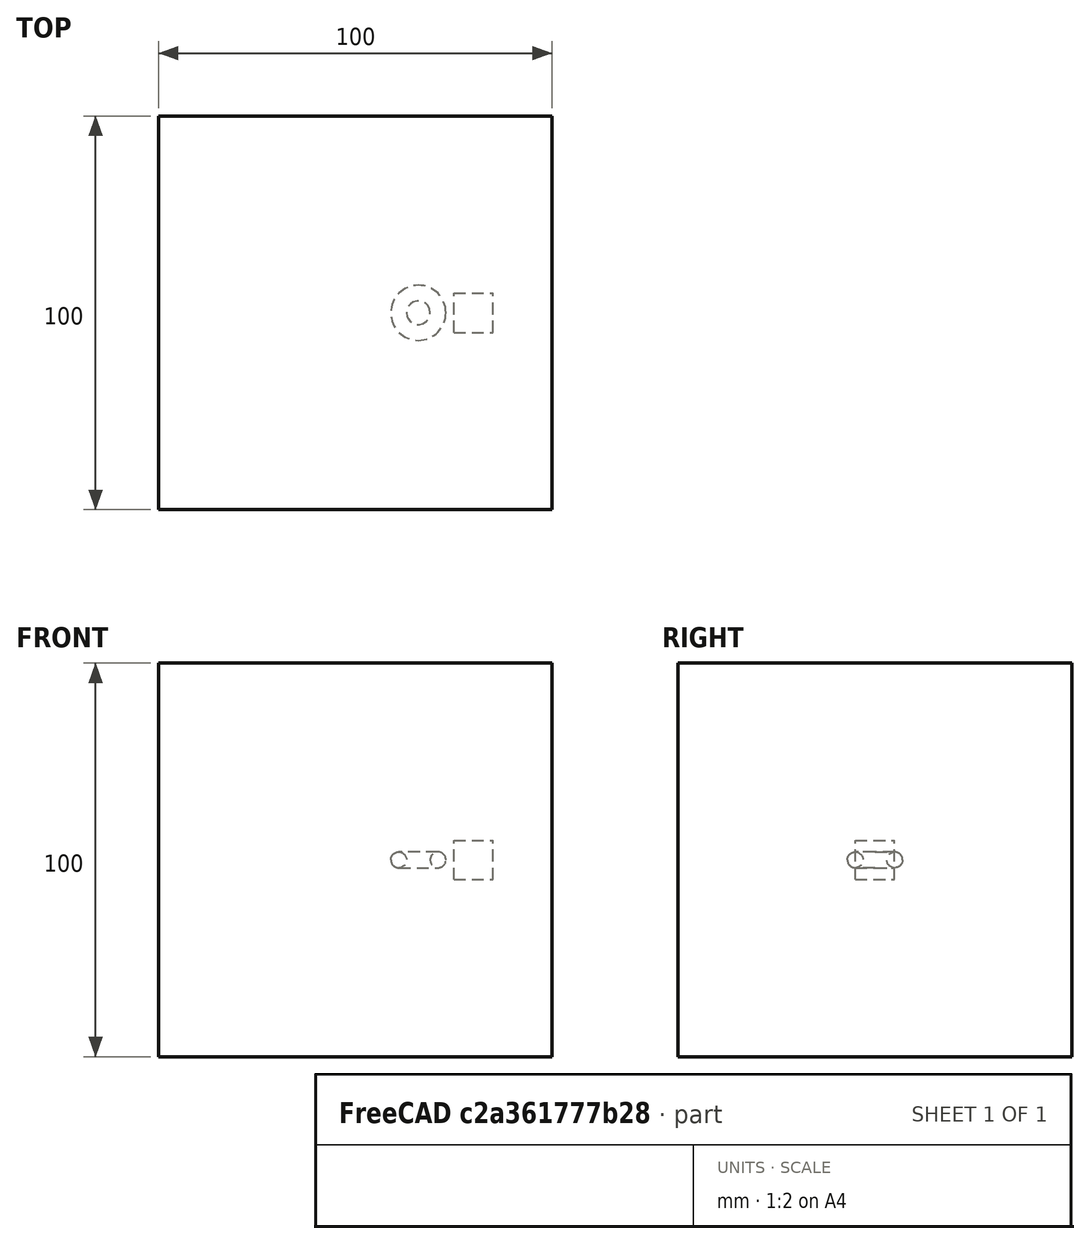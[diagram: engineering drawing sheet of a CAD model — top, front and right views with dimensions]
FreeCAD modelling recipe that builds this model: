
FCSTD DOCUMENT  (FreeCAD 0.20RUnknown)
Label: polarArray-6
License: All rights reserved
objects: App::DocumentObjectGroupPython×1251, App::Part×5, Part::FeaturePython×4
note: 3 computed .brp shape members not serialized (recipe doc carries the construction recipe); baked Part::Feature solids carry a one-line shape summary decoded from their .brp

FEATURE [App::DocumentObjectGroupPython] HALFPI  # scripted group (container) (typed FeaturePython)
  name = HALFPI
  value = pi/2.
FEATURE [App::DocumentObjectGroupPython] PI  # scripted group (container) (typed FeaturePython)
  name = PI
  value = 1.*pi
FEATURE [App::DocumentObjectGroupPython] TWOPI  # scripted group (container) (typed FeaturePython)
  name = TWOPI
  value = 2.*pi
FEATURE [App::DocumentObjectGroupPython] Constants  # scripted group (container) (typed FeaturePython)
  Group = -> [HALFPI,PI,TWOPI]
FEATURE [App::DocumentObjectGroupPython] Variables  # scripted group (container) (typed FeaturePython)
FEATURE [App::DocumentObjectGroupPython] Quantities  # scripted group (container) (typed FeaturePython)
FEATURE [App::DocumentObjectGroupPython] Isotopes  # scripted group (container) (typed FeaturePython)
FEATURE [App::DocumentObjectGroupPython] Elements  # scripted group (container) (typed FeaturePython)
FEATURE [App::DocumentObjectGroupPython] Matrix  # scripted group (container) (typed FeaturePython)
FEATURE [App::DocumentObjectGroupPython] Surfaces  # scripted group (container) (typed FeaturePython)
FEATURE [App::DocumentObjectGroupPython] Opticals  # scripted group (container) (typed FeaturePython)
  Group = -> [Matrix,Surfaces]
FEATURE [App::DocumentObjectGroupPython] G4Isotopes  # scripted group (container) (typed FeaturePython)
FEATURE [App::DocumentObjectGroupPython] H_element  # scripted group (container) (typed FeaturePython)
  Z = 1
  atom_value = 1.008
  formula = H
  name = H_element
FEATURE [App::DocumentObjectGroupPython] He_element  # scripted group (container) (typed FeaturePython)
  Z = 2
  atom_value = 4.0026
  formula = He
  name = He_element
FEATURE [App::DocumentObjectGroupPython] Li_element  # scripted group (container) (typed FeaturePython)
  Z = 3
  atom_value = 6.94
  formula = Li
  name = Li_element
FEATURE [App::DocumentObjectGroupPython] Be_element  # scripted group (container) (typed FeaturePython)
  Z = 4
  atom_value = 9.01218
  formula = Be
  name = Be_element
FEATURE [App::DocumentObjectGroupPython] B_element  # scripted group (container) (typed FeaturePython)
  Z = 5
  atom_value = 10.81
  formula = B
  name = B_element
FEATURE [App::DocumentObjectGroupPython] C_element  # scripted group (container) (typed FeaturePython)
  Z = 6
  atom_value = 12.011
  formula = C
  name = C_element
FEATURE [App::DocumentObjectGroupPython] N_element  # scripted group (container) (typed FeaturePython)
  Z = 7
  atom_value = 14.007
  formula = N
  name = N_element
FEATURE [App::DocumentObjectGroupPython] O_element  # scripted group (container) (typed FeaturePython)
  Z = 8
  atom_value = 15.999
  formula = O
  name = O_element
FEATURE [App::DocumentObjectGroupPython] F_element  # scripted group (container) (typed FeaturePython)
  Z = 9
  atom_value = 18.9984
  formula = F
  name = F_element
FEATURE [App::DocumentObjectGroupPython] Ne_element  # scripted group (container) (typed FeaturePython)
  Z = 10
  atom_value = 20.1797
  formula = Ne
  name = Ne_element
FEATURE [App::DocumentObjectGroupPython] Na_element  # scripted group (container) (typed FeaturePython)
  Z = 11
  atom_value = 22.9898
  formula = Na
  name = Na_element
FEATURE [App::DocumentObjectGroupPython] Mg_element  # scripted group (container) (typed FeaturePython)
  Z = 12
  atom_value = 24.305
  formula = Mg
  name = Mg_element
FEATURE [App::DocumentObjectGroupPython] Al_element  # scripted group (container) (typed FeaturePython)
  Z = 13
  atom_value = 26.9815
  formula = Al
  name = Al_element
FEATURE [App::DocumentObjectGroupPython] Si_element  # scripted group (container) (typed FeaturePython)
  Z = 14
  atom_value = 28.085
  formula = Si
  name = Si_element
FEATURE [App::DocumentObjectGroupPython] P_element  # scripted group (container) (typed FeaturePython)
  Z = 15
  atom_value = 30.9738
  formula = P
  name = P_element
FEATURE [App::DocumentObjectGroupPython] S_element  # scripted group (container) (typed FeaturePython)
  Z = 16
  atom_value = 32.06
  formula = S
  name = S_element
FEATURE [App::DocumentObjectGroupPython] Cl_element  # scripted group (container) (typed FeaturePython)
  Z = 17
  atom_value = 35.45
  formula = Cl
  name = Cl_element
FEATURE [App::DocumentObjectGroupPython] Ar_element  # scripted group (container) (typed FeaturePython)
  Z = 18
  atom_value = 39.95
  formula = Ar
  name = Ar_element
FEATURE [App::DocumentObjectGroupPython] K_element  # scripted group (container) (typed FeaturePython)
  Z = 19
  atom_value = 39.0983
  formula = K
  name = K_element
FEATURE [App::DocumentObjectGroupPython] Ca_element  # scripted group (container) (typed FeaturePython)
  Z = 20
  atom_value = 40.078
  formula = Ca
  name = Ca_element
FEATURE [App::DocumentObjectGroupPython] Sc_element  # scripted group (container) (typed FeaturePython)
  Z = 21
  atom_value = 44.9559
  formula = Sc
  name = Sc_element
FEATURE [App::DocumentObjectGroupPython] Ti_element  # scripted group (container) (typed FeaturePython)
  Z = 22
  atom_value = 47.867
  formula = Ti
  name = Ti_element
FEATURE [App::DocumentObjectGroupPython] V_element  # scripted group (container) (typed FeaturePython)
  Z = 23
  atom_value = 50.9415
  formula = V
  name = V_element
FEATURE [App::DocumentObjectGroupPython] Cr_element  # scripted group (container) (typed FeaturePython)
  Z = 24
  atom_value = 51.9961
  formula = Cr
  name = Cr_element
FEATURE [App::DocumentObjectGroupPython] Mn_element  # scripted group (container) (typed FeaturePython)
  Z = 25
  atom_value = 54.938
  formula = Mn
  name = Mn_element
FEATURE [App::DocumentObjectGroupPython] Fe_element  # scripted group (container) (typed FeaturePython)
  Z = 26
  atom_value = 55.845
  formula = Fe
  name = Fe_element
FEATURE [App::DocumentObjectGroupPython] Co_element  # scripted group (container) (typed FeaturePython)
  Z = 27
  atom_value = 58.9332
  formula = Co
  name = Co_element
FEATURE [App::DocumentObjectGroupPython] Ni_element  # scripted group (container) (typed FeaturePython)
  Z = 28
  atom_value = 58.6934
  formula = Ni
  name = Ni_element
FEATURE [App::DocumentObjectGroupPython] Cu_element  # scripted group (container) (typed FeaturePython)
  Z = 29
  atom_value = 63.546
  formula = Cu
  name = Cu_element
FEATURE [App::DocumentObjectGroupPython] Zn_element  # scripted group (container) (typed FeaturePython)
  Z = 30
  atom_value = 65.38
  formula = Zn
  name = Zn_element
FEATURE [App::DocumentObjectGroupPython] Ga_element  # scripted group (container) (typed FeaturePython)
  Z = 31
  atom_value = 69.723
  formula = Ga
  name = Ga_element
FEATURE [App::DocumentObjectGroupPython] Ge_element  # scripted group (container) (typed FeaturePython)
  Z = 32
  atom_value = 72.63
  formula = Ge
  name = Ge_element
FEATURE [App::DocumentObjectGroupPython] As_element  # scripted group (container) (typed FeaturePython)
  Z = 33
  atom_value = 74.9216
  formula = As
  name = As_element
FEATURE [App::DocumentObjectGroupPython] Se_element  # scripted group (container) (typed FeaturePython)
  Z = 34
  atom_value = 78.971
  formula = Se
  name = Se_element
FEATURE [App::DocumentObjectGroupPython] Br_element  # scripted group (container) (typed FeaturePython)
  Z = 35
  atom_value = 79.904
  formula = Br
  name = Br_element
FEATURE [App::DocumentObjectGroupPython] Kr_element  # scripted group (container) (typed FeaturePython)
  Z = 36
  atom_value = 83.798
  formula = Kr
  name = Kr_element
FEATURE [App::DocumentObjectGroupPython] Rb_element  # scripted group (container) (typed FeaturePython)
  Z = 37
  atom_value = 85.4678
  formula = Rb
  name = Rb_element
FEATURE [App::DocumentObjectGroupPython] Sr_element  # scripted group (container) (typed FeaturePython)
  Z = 38
  atom_value = 87.62
  formula = Sr
  name = Sr_element
FEATURE [App::DocumentObjectGroupPython] Y_element  # scripted group (container) (typed FeaturePython)
  Z = 39
  atom_value = 88.9058
  formula = Y
  name = Y_element
FEATURE [App::DocumentObjectGroupPython] Zr_element  # scripted group (container) (typed FeaturePython)
  Z = 40
  atom_value = 91.224
  formula = Zr
  name = Zr_element
FEATURE [App::DocumentObjectGroupPython] Nb_element  # scripted group (container) (typed FeaturePython)
  Z = 41
  atom_value = 92.9064
  formula = Nb
  name = Nb_element
FEATURE [App::DocumentObjectGroupPython] Mo_element  # scripted group (container) (typed FeaturePython)
  Z = 42
  atom_value = 95.95
  formula = Mo
  name = Mo_element
FEATURE [App::DocumentObjectGroupPython] Tc_element  # scripted group (container) (typed FeaturePython)
  Z = 43
  atom_value = 97
  formula = Tc
  name = Tc_element
FEATURE [App::DocumentObjectGroupPython] Ru_element  # scripted group (container) (typed FeaturePython)
  Z = 44
  atom_value = 101.07
  formula = Ru
  name = Ru_element
FEATURE [App::DocumentObjectGroupPython] Rh_element  # scripted group (container) (typed FeaturePython)
  Z = 45
  atom_value = 102.905
  formula = Rh
  name = Rh_element
FEATURE [App::DocumentObjectGroupPython] Pd_element  # scripted group (container) (typed FeaturePython)
  Z = 46
  atom_value = 106.42
  formula = Pd
  name = Pd_element
FEATURE [App::DocumentObjectGroupPython] Ag_element  # scripted group (container) (typed FeaturePython)
  Z = 47
  atom_value = 107.868
  formula = Ag
  name = Ag_element
FEATURE [App::DocumentObjectGroupPython] Cd_element  # scripted group (container) (typed FeaturePython)
  Z = 48
  atom_value = 112.414
  formula = Cd
  name = Cd_element
FEATURE [App::DocumentObjectGroupPython] In_element  # scripted group (container) (typed FeaturePython)
  Z = 49
  atom_value = 114.818
  formula = In
  name = In_element
FEATURE [App::DocumentObjectGroupPython] Sn_element  # scripted group (container) (typed FeaturePython)
  Z = 50
  atom_value = 118.71
  formula = Sn
  name = Sn_element
FEATURE [App::DocumentObjectGroupPython] Sb_element  # scripted group (container) (typed FeaturePython)
  Z = 51
  atom_value = 121.76
  formula = Sb
  name = Sb_element
FEATURE [App::DocumentObjectGroupPython] Te_element  # scripted group (container) (typed FeaturePython)
  Z = 52
  atom_value = 127.6
  formula = Te
  name = Te_element
FEATURE [App::DocumentObjectGroupPython] I_element  # scripted group (container) (typed FeaturePython)
  Z = 53
  atom_value = 126.904
  formula = I
  name = I_element
FEATURE [App::DocumentObjectGroupPython] Xe_element  # scripted group (container) (typed FeaturePython)
  Z = 54
  atom_value = 131.293
  formula = Xe
  name = Xe_element
FEATURE [App::DocumentObjectGroupPython] Cs_element  # scripted group (container) (typed FeaturePython)
  Z = 55
  atom_value = 132.905
  formula = Cs
  name = Cs_element
FEATURE [App::DocumentObjectGroupPython] Ba_element  # scripted group (container) (typed FeaturePython)
  Z = 56
  atom_value = 137.327
  formula = Ba
  name = Ba_element
FEATURE [App::DocumentObjectGroupPython] La_element  # scripted group (container) (typed FeaturePython)
  Z = 57
  atom_value = 138.905
  formula = La
  name = La_element
FEATURE [App::DocumentObjectGroupPython] Ce_element  # scripted group (container) (typed FeaturePython)
  Z = 58
  atom_value = 140.116
  formula = Ce
  name = Ce_element
FEATURE [App::DocumentObjectGroupPython] Pr_element  # scripted group (container) (typed FeaturePython)
  Z = 59
  atom_value = 140.908
  formula = Pr
  name = Pr_element
FEATURE [App::DocumentObjectGroupPython] Nd_element  # scripted group (container) (typed FeaturePython)
  Z = 60
  atom_value = 144.242
  formula = Nd
  name = Nd_element
FEATURE [App::DocumentObjectGroupPython] Pm_element  # scripted group (container) (typed FeaturePython)
  Z = 61
  atom_value = 145
  formula = Pm
  name = Pm_element
FEATURE [App::DocumentObjectGroupPython] Sm_element  # scripted group (container) (typed FeaturePython)
  Z = 62
  atom_value = 150.36
  formula = Sm
  name = Sm_element
FEATURE [App::DocumentObjectGroupPython] Eu_element  # scripted group (container) (typed FeaturePython)
  Z = 63
  atom_value = 151.964
  formula = Eu
  name = Eu_element
FEATURE [App::DocumentObjectGroupPython] Gd_element  # scripted group (container) (typed FeaturePython)
  Z = 64
  atom_value = 157.25
  formula = Gd
  name = Gd_element
FEATURE [App::DocumentObjectGroupPython] Tb_element  # scripted group (container) (typed FeaturePython)
  Z = 65
  atom_value = 158.925
  formula = Tb
  name = Tb_element
FEATURE [App::DocumentObjectGroupPython] Dy_element  # scripted group (container) (typed FeaturePython)
  Z = 66
  atom_value = 162.5
  formula = Dy
  name = Dy_element
FEATURE [App::DocumentObjectGroupPython] Ho_element  # scripted group (container) (typed FeaturePython)
  Z = 67
  atom_value = 164.93
  formula = Ho
  name = Ho_element
FEATURE [App::DocumentObjectGroupPython] Er_element  # scripted group (container) (typed FeaturePython)
  Z = 68
  atom_value = 167.259
  formula = Er
  name = Er_element
FEATURE [App::DocumentObjectGroupPython] Tm_element  # scripted group (container) (typed FeaturePython)
  Z = 69
  atom_value = 168.934
  formula = Tm
  name = Tm_element
FEATURE [App::DocumentObjectGroupPython] Yb_element  # scripted group (container) (typed FeaturePython)
  Z = 70
  atom_value = 173.045
  formula = Yb
  name = Yb_element
FEATURE [App::DocumentObjectGroupPython] Lu_element  # scripted group (container) (typed FeaturePython)
  Z = 71
  atom_value = 174.967
  formula = Lu
  name = Lu_element
FEATURE [App::DocumentObjectGroupPython] Hf_element  # scripted group (container) (typed FeaturePython)
  Z = 72
  atom_value = 178.49
  formula = Hf
  name = Hf_element
FEATURE [App::DocumentObjectGroupPython] Ta_element  # scripted group (container) (typed FeaturePython)
  Z = 73
  atom_value = 180.948
  formula = Ta
  name = Ta_element
FEATURE [App::DocumentObjectGroupPython] W_element  # scripted group (container) (typed FeaturePython)
  Z = 74
  atom_value = 183.84
  formula = W
  name = W_element
FEATURE [App::DocumentObjectGroupPython] Re_element  # scripted group (container) (typed FeaturePython)
  Z = 75
  atom_value = 186.207
  formula = Re
  name = Re_element
FEATURE [App::DocumentObjectGroupPython] Os_element  # scripted group (container) (typed FeaturePython)
  Z = 76
  atom_value = 190.23
  formula = Os
  name = Os_element
FEATURE [App::DocumentObjectGroupPython] Ir_element  # scripted group (container) (typed FeaturePython)
  Z = 77
  atom_value = 192.217
  formula = Ir
  name = Ir_element
FEATURE [App::DocumentObjectGroupPython] Pt_element  # scripted group (container) (typed FeaturePython)
  Z = 78
  atom_value = 195.084
  formula = Pt
  name = Pt_element
FEATURE [App::DocumentObjectGroupPython] Au_element  # scripted group (container) (typed FeaturePython)
  Z = 79
  atom_value = 196.967
  formula = Au
  name = Au_element
FEATURE [App::DocumentObjectGroupPython] Hg_element  # scripted group (container) (typed FeaturePython)
  Z = 80
  atom_value = 200.592
  formula = Hg
  name = Hg_element
FEATURE [App::DocumentObjectGroupPython] Tl_element  # scripted group (container) (typed FeaturePython)
  Z = 81
  atom_value = 204.38
  formula = Tl
  name = Tl_element
FEATURE [App::DocumentObjectGroupPython] Pb_element  # scripted group (container) (typed FeaturePython)
  Z = 82
  atom_value = 207.2
  formula = Pb
  name = Pb_element
FEATURE [App::DocumentObjectGroupPython] Bi_element  # scripted group (container) (typed FeaturePython)
  Z = 83
  atom_value = 208.98
  formula = Bi
  name = Bi_element
FEATURE [App::DocumentObjectGroupPython] Po_element  # scripted group (container) (typed FeaturePython)
  Z = 84
  atom_value = 209
  formula = Po
  name = Po_element
FEATURE [App::DocumentObjectGroupPython] At_element  # scripted group (container) (typed FeaturePython)
  Z = 85
  atom_value = 210
  formula = At
  name = At_element
FEATURE [App::DocumentObjectGroupPython] Rn_element  # scripted group (container) (typed FeaturePython)
  Z = 86
  atom_value = 222
  formula = Rn
  name = Rn_element
FEATURE [App::DocumentObjectGroupPython] Fr_element  # scripted group (container) (typed FeaturePython)
  Z = 87
  atom_value = 223
  formula = Fr
  name = Fr_element
FEATURE [App::DocumentObjectGroupPython] Ra_element  # scripted group (container) (typed FeaturePython)
  Z = 88
  atom_value = 226
  formula = Ra
  name = Ra_element
FEATURE [App::DocumentObjectGroupPython] Ac_element  # scripted group (container) (typed FeaturePython)
  Z = 89
  atom_value = 227
  formula = Ac
  name = Ac_element
FEATURE [App::DocumentObjectGroupPython] Th_element  # scripted group (container) (typed FeaturePython)
  Z = 90
  atom_value = 232.038
  formula = Th
  name = Th_element
FEATURE [App::DocumentObjectGroupPython] Pa_element  # scripted group (container) (typed FeaturePython)
  Z = 91
  atom_value = 231.036
  formula = Pa
  name = Pa_element
FEATURE [App::DocumentObjectGroupPython] U_element  # scripted group (container) (typed FeaturePython)
  Z = 92
  atom_value = 238.029
  formula = U
  name = U_element
FEATURE [App::DocumentObjectGroupPython] Np_element  # scripted group (container) (typed FeaturePython)
  Z = 93
  atom_value = 237
  formula = Np
  name = Np_element
FEATURE [App::DocumentObjectGroupPython] Pu_element  # scripted group (container) (typed FeaturePython)
  Z = 94
  atom_value = 244
  formula = Pu
  name = Pu_element
FEATURE [App::DocumentObjectGroupPython] Am_element  # scripted group (container) (typed FeaturePython)
  Z = 95
  atom_value = 243
  formula = Am
  name = Am_element
FEATURE [App::DocumentObjectGroupPython] Cm_element  # scripted group (container) (typed FeaturePython)
  Z = 96
  atom_value = 247
  formula = Cm
  name = Cm_element
FEATURE [App::DocumentObjectGroupPython] Bk_element  # scripted group (container) (typed FeaturePython)
  Z = 97
  atom_value = 247
  formula = Bk
  name = Bk_element
FEATURE [App::DocumentObjectGroupPython] Cf_element  # scripted group (container) (typed FeaturePython)
  Z = 98
  atom_value = 251
  formula = Cf
  name = Cf_element
FEATURE [App::DocumentObjectGroupPython] G4Elements  # scripted group (container) (typed FeaturePython)
  Group = -> [H_element,He_element,Li_element,Be_element,B_element,C_element,N_element,O_element,F_element,Ne_element,Na_element,Mg_element,Al_element,Si_element,P_element,S_element,Cl_element,Ar_element,K_element,Ca_element,Sc_element,Ti_element,V_element,Cr_element,Mn_element,Fe_element,Co_element,Ni_element,Cu_element,Zn_element,Ga_element,Ge_element,As_element,Se_element,Br_element,Kr_element,Rb_element,+61 more]
FEATURE [App::DocumentObjectGroupPython] H_element001  label="H_element : 0.101"  # scripted group (container) (typed FeaturePython)
  n = 0.101327
FEATURE [App::DocumentObjectGroupPython] C_element001  label="C_element : 0.775"  # scripted group (container) (typed FeaturePython)
  n = 0.7755
FEATURE [App::DocumentObjectGroupPython] N_element001  label="N_element : 0.035"  # scripted group (container) (typed FeaturePython)
  n = 0.035057
FEATURE [App::DocumentObjectGroupPython] O_element001  label="O_element : 0.052"  # scripted group (container) (typed FeaturePython)
  n = 0.0523159
FEATURE [App::DocumentObjectGroupPython] F_element001  label="F_element : 0.017"  # scripted group (container) (typed FeaturePython)
  n = 0.017422
FEATURE [App::DocumentObjectGroupPython] Ca_element001  label="Ca_element : 0.018"  # scripted group (container) (typed FeaturePython)
  n = 0.018378
FEATURE [App::DocumentObjectGroupPython] G4_A_150_TISSUE  label="G4_A-150_TISSUE"  # scripted group (container) (typed FeaturePython)
  Dunit = g/cm3
  Dvalue = 1.127
  Group = -> [H_element001,C_element001,N_element001,O_element001,F_element001,Ca_element001]
  conduct = 2
  density = 1
  expand = 3
  formula = G4_A-150_TISSUE
  name = G4_A-150_TISSUE
  specific = 4
FEATURE [App::DocumentObjectGroupPython] C_element002  label="C_element : 3"  # scripted group (container) (typed FeaturePython)
  n = 3
  ref = C_element
FEATURE [App::DocumentObjectGroupPython] H_element002  label="H_element : 6"  # scripted group (container) (typed FeaturePython)
  n = 6
  ref = H_element
FEATURE [App::DocumentObjectGroupPython] O_element002  label="O_element : 1"  # scripted group (container) (typed FeaturePython)
  n = 1
  ref = O_element
FEATURE [App::DocumentObjectGroupPython] G4_ACETONE  # scripted group (container) (typed FeaturePython)
  Dunit = g/cm3
  Dvalue = 0.7899
  Group = -> [C_element002,H_element002,O_element002]
  conduct = 2
  density = 1
  expand = 3
  formula = G4_ACETONE
  name = G4_ACETONE
  specific = 4
FEATURE [App::DocumentObjectGroupPython] C_element003  label="C_element : 2"  # scripted group (container) (typed FeaturePython)
  n = 2
  ref = C_element
FEATURE [App::DocumentObjectGroupPython] H_element003  label="H_element : 2"  # scripted group (container) (typed FeaturePython)
  n = 2
  ref = H_element
FEATURE [App::DocumentObjectGroupPython] G4_ACETYLENE  # scripted group (container) (typed FeaturePython)
  Dunit = g/cm3
  Dvalue = 0.0010967
  Group = -> [C_element003,H_element003]
  conduct = 2
  density = 1
  expand = 3
  formula = G4_ACETYLENE
  name = G4_ACETYLENE
  specific = 4
FEATURE [App::DocumentObjectGroupPython] C_element004  label="C_element : 5"  # scripted group (container) (typed FeaturePython)
  n = 5
  ref = C_element
FEATURE [App::DocumentObjectGroupPython] H_element004  label="H_element : 5"  # scripted group (container) (typed FeaturePython)
  n = 5
  ref = H_element
FEATURE [App::DocumentObjectGroupPython] N_element002  label="N_element : 5"  # scripted group (container) (typed FeaturePython)
  n = 5
  ref = N_element
FEATURE [App::DocumentObjectGroupPython] G4_ADENINE  # scripted group (container) (typed FeaturePython)
  Dunit = g/cm3
  Dvalue = 1.6
  Group = -> [C_element004,H_element004,N_element002]
  conduct = 2
  density = 1
  expand = 3
  formula = G4_ADENINE
  name = G4_ADENINE
  specific = 4
FEATURE [App::DocumentObjectGroupPython] H_element005  label="H_element : 0.114"  # scripted group (container) (typed FeaturePython)
  n = 0.114
FEATURE [App::DocumentObjectGroupPython] C_element005  label="C_element : 0.598"  # scripted group (container) (typed FeaturePython)
  n = 0.598
FEATURE [App::DocumentObjectGroupPython] N_element003  label="N_element : 0.007"  # scripted group (container) (typed FeaturePython)
  n = 0.007
FEATURE [App::DocumentObjectGroupPython] O_element003  label="O_element : 0.278"  # scripted group (container) (typed FeaturePython)
  n = 0.278
FEATURE [App::DocumentObjectGroupPython] Na_element001  label="Na_element : 0.001"  # scripted group (container) (typed FeaturePython)
  n = 0.001
FEATURE [App::DocumentObjectGroupPython] S_element001  label="S_element : 0.001"  # scripted group (container) (typed FeaturePython)
  n = 0.001
FEATURE [App::DocumentObjectGroupPython] Cl_element001  label="Cl_element : 0.001"  # scripted group (container) (typed FeaturePython)
  n = 0.001
FEATURE [App::DocumentObjectGroupPython] G4_ADIPOSE_TISSUE_ICRP  # scripted group (container) (typed FeaturePython)
  Dunit = g/cm3
  Dvalue = 0.95
  Group = -> [H_element005,C_element005,N_element003,O_element003,Na_element001,S_element001,Cl_element001]
  conduct = 2
  density = 1
  expand = 3
  formula = G4_ADIPOSE_TISSUE_ICRP
  name = G4_ADIPOSE_TISSUE_ICRP
  specific = 4
FEATURE [App::DocumentObjectGroupPython] C_element006  label="C_element : 0.000"  # scripted group (container) (typed FeaturePython)
  n = 0.000124
FEATURE [App::DocumentObjectGroupPython] N_element004  label="N_element : 0.755"  # scripted group (container) (typed FeaturePython)
  n = 0.755268
FEATURE [App::DocumentObjectGroupPython] O_element004  label="O_element : 0.232"  # scripted group (container) (typed FeaturePython)
  n = 0.231781
FEATURE [App::DocumentObjectGroupPython] Ar_element001  label="Ar_element : 0.013"  # scripted group (container) (typed FeaturePython)
  n = 0.012827
FEATURE [App::DocumentObjectGroupPython] G4_AIR  # scripted group (container) (typed FeaturePython)
  Dunit = g/cm3
  Dvalue = 0.00120479
  Group = -> [C_element006,N_element004,O_element004,Ar_element001]
  conduct = 2
  density = 1
  expand = 3
  formula = G4_AIR
  name = G4_AIR
  specific = 4
FEATURE [App::DocumentObjectGroupPython] C_element007  label="C_element : 006"  # scripted group (container) (typed FeaturePython)
  n = 3
  ref = C_element
FEATURE [App::DocumentObjectGroupPython] H_element006  label="H_element : 7"  # scripted group (container) (typed FeaturePython)
  n = 7
  ref = H_element
FEATURE [App::DocumentObjectGroupPython] N_element005  label="N_element : 1"  # scripted group (container) (typed FeaturePython)
  n = 1
  ref = N_element
FEATURE [App::DocumentObjectGroupPython] O_element005  label="O_element : 2"  # scripted group (container) (typed FeaturePython)
  n = 2
  ref = O_element
FEATURE [App::DocumentObjectGroupPython] G4_ALANINE  # scripted group (container) (typed FeaturePython)
  Dunit = g/cm3
  Dvalue = 1.42
  Group = -> [C_element007,H_element006,N_element005,O_element005]
  conduct = 2
  density = 1
  expand = 3
  formula = G4_ALANINE
  name = G4_ALANINE
  specific = 4
FEATURE [App::DocumentObjectGroupPython] Al_element001  label="Al_element : 2"  # scripted group (container) (typed FeaturePython)
  n = 2
  ref = Al_element
FEATURE [App::DocumentObjectGroupPython] O_element006  label="O_element : 3"  # scripted group (container) (typed FeaturePython)
  n = 3
  ref = O_element
FEATURE [App::DocumentObjectGroupPython] G4_ALUMINUM_OXIDE  # scripted group (container) (typed FeaturePython)
  Dunit = g/cm3
  Dvalue = 3.97
  Group = -> [Al_element001,O_element006]
  conduct = 2
  density = 1
  expand = 3
  formula = G4_ALUMINUM_OXIDE
  name = G4_ALUMINUM_OXIDE
  specific = 4
FEATURE [App::DocumentObjectGroupPython] H_element007  label="H_element : 0.106"  # scripted group (container) (typed FeaturePython)
  n = 0.10593
FEATURE [App::DocumentObjectGroupPython] C_element008  label="C_element : 0.789"  # scripted group (container) (typed FeaturePython)
  n = 0.788974
FEATURE [App::DocumentObjectGroupPython] O_element007  label="O_element : 0.105"  # scripted group (container) (typed FeaturePython)
  n = 0.105096
FEATURE [App::DocumentObjectGroupPython] G4_AMBER  # scripted group (container) (typed FeaturePython)
  Dunit = g/cm3
  Dvalue = 1.1
  Group = -> [H_element007,C_element008,O_element007]
  conduct = 2
  density = 1
  expand = 3
  formula = G4_AMBER
  name = G4_AMBER
  specific = 4
FEATURE [App::DocumentObjectGroupPython] N_element006  label="N_element : 006"  # scripted group (container) (typed FeaturePython)
  n = 1
  ref = N_element
FEATURE [App::DocumentObjectGroupPython] H_element008  label="H_element : 3"  # scripted group (container) (typed FeaturePython)
  n = 3
  ref = H_element
FEATURE [App::DocumentObjectGroupPython] G4_AMMONIA  # scripted group (container) (typed FeaturePython)
  Dunit = g/cm3
  Dvalue = 0.000826019
  Group = -> [N_element006,H_element008]
  conduct = 2
  density = 1
  expand = 3
  formula = G4_AMMONIA
  name = G4_AMMONIA
  specific = 4
FEATURE [App::DocumentObjectGroupPython] C_element009  label="C_element : 6"  # scripted group (container) (typed FeaturePython)
  n = 6
  ref = C_element
FEATURE [App::DocumentObjectGroupPython] H_element009  label="H_element : 008"  # scripted group (container) (typed FeaturePython)
  n = 7
  ref = H_element
FEATURE [App::DocumentObjectGroupPython] N_element007  label="N_element : 007"  # scripted group (container) (typed FeaturePython)
  n = 1
  ref = N_element
FEATURE [App::DocumentObjectGroupPython] G4_ANILINE  # scripted group (container) (typed FeaturePython)
  Dunit = g/cm3
  Dvalue = 1.0235
  Group = -> [C_element009,H_element009,N_element007]
  conduct = 2
  density = 1
  expand = 3
  formula = G4_ANILINE
  name = G4_ANILINE
  specific = 4
FEATURE [App::DocumentObjectGroupPython] C_element010  label="C_element : 14"  # scripted group (container) (typed FeaturePython)
  n = 14
  ref = C_element
FEATURE [App::DocumentObjectGroupPython] H_element010  label="H_element : 10"  # scripted group (container) (typed FeaturePython)
  n = 10
  ref = H_element
FEATURE [App::DocumentObjectGroupPython] G4_ANTHRACENE  # scripted group (container) (typed FeaturePython)
  Dunit = g/cm3
  Dvalue = 1.283
  Group = -> [C_element010,H_element010]
  conduct = 2
  density = 1
  expand = 3
  formula = G4_ANTHRACENE
  name = G4_ANTHRACENE
  specific = 4
FEATURE [App::DocumentObjectGroupPython] H_element011  label="H_element : 0.065"  # scripted group (container) (typed FeaturePython)
  n = 0.0654709
FEATURE [App::DocumentObjectGroupPython] C_element011  label="C_element : 0.537"  # scripted group (container) (typed FeaturePython)
  n = 0.536944
FEATURE [App::DocumentObjectGroupPython] N_element008  label="N_element : 0.021"  # scripted group (container) (typed FeaturePython)
  n = 0.0215
FEATURE [App::DocumentObjectGroupPython] O_element008  label="O_element : 0.032"  # scripted group (container) (typed FeaturePython)
  n = 0.032085
FEATURE [App::DocumentObjectGroupPython] F_element002  label="F_element : 0.167"  # scripted group (container) (typed FeaturePython)
  n = 0.167411
FEATURE [App::DocumentObjectGroupPython] Ca_element002  label="Ca_element : 0.177"  # scripted group (container) (typed FeaturePython)
  n = 0.176589
FEATURE [App::DocumentObjectGroupPython] G4_B_100_BONE  label="G4_B-100_BONE"  # scripted group (container) (typed FeaturePython)
  Dunit = g/cm3
  Dvalue = 1.45
  Group = -> [H_element011,C_element011,N_element008,O_element008,F_element002,Ca_element002]
  conduct = 2
  density = 1
  expand = 3
  formula = G4_B-100_BONE
  name = G4_B-100_BONE
  specific = 4
FEATURE [App::DocumentObjectGroupPython] H_element012  label="H_element : 0.057"  # scripted group (container) (typed FeaturePython)
  n = 0.057441
FEATURE [App::DocumentObjectGroupPython] C_element012  label="C_element : 0.790"  # scripted group (container) (typed FeaturePython)
  n = 0.774591
FEATURE [App::DocumentObjectGroupPython] O_element009  label="O_element : 0.168"  # scripted group (container) (typed FeaturePython)
  n = 0.167968
FEATURE [App::DocumentObjectGroupPython] G4_BAKELITE  # scripted group (container) (typed FeaturePython)
  Dunit = g/cm3
  Dvalue = 1.25
  Group = -> [H_element012,C_element012,O_element009]
  conduct = 2
  density = 1
  expand = 3
  formula = G4_BAKELITE
  name = G4_BAKELITE
  specific = 4
FEATURE [App::DocumentObjectGroupPython] Ba_element001  label="Ba_element : 1"  # scripted group (container) (typed FeaturePython)
  n = 1
  ref = Ba_element
FEATURE [App::DocumentObjectGroupPython] F_element003  label="F_element : 2"  # scripted group (container) (typed FeaturePython)
  n = 2
  ref = F_element
FEATURE [App::DocumentObjectGroupPython] G4_BARIUM_FLUORIDE  # scripted group (container) (typed FeaturePython)
  Dunit = g/cm3
  Dvalue = 4.89
  Group = -> [Ba_element001,F_element003]
  conduct = 2
  density = 1
  expand = 3
  formula = G4_BARIUM_FLUORIDE
  name = G4_BARIUM_FLUORIDE
  specific = 4
FEATURE [App::DocumentObjectGroupPython] Ba_element002  label="Ba_element : 002"  # scripted group (container) (typed FeaturePython)
  n = 1
  ref = Ba_element
FEATURE [App::DocumentObjectGroupPython] S_element002  label="S_element : 1"  # scripted group (container) (typed FeaturePython)
  n = 1
  ref = S_element
FEATURE [App::DocumentObjectGroupPython] O_element010  label="O_element : 4"  # scripted group (container) (typed FeaturePython)
  n = 4
  ref = O_element
FEATURE [App::DocumentObjectGroupPython] G4_BARIUM_SULFATE  # scripted group (container) (typed FeaturePython)
  Dunit = g/cm3
  Dvalue = 4.5
  Group = -> [Ba_element002,S_element002,O_element010]
  conduct = 2
  density = 1
  expand = 3
  formula = G4_BARIUM_SULFATE
  name = G4_BARIUM_SULFATE
  specific = 4
FEATURE [App::DocumentObjectGroupPython] C_element013  label="C_element : 007"  # scripted group (container) (typed FeaturePython)
  n = 6
  ref = C_element
FEATURE [App::DocumentObjectGroupPython] H_element013  label="H_element : 009"  # scripted group (container) (typed FeaturePython)
  n = 6
  ref = H_element
FEATURE [App::DocumentObjectGroupPython] G4_BENZENE  # scripted group (container) (typed FeaturePython)
  Dunit = g/cm3
  Dvalue = 0.87865
  Group = -> [C_element013,H_element013]
  conduct = 2
  density = 1
  expand = 3
  formula = G4_BENZENE
  name = G4_BENZENE
  specific = 4
FEATURE [App::DocumentObjectGroupPython] Be_element001  label="Be_element : 1"  # scripted group (container) (typed FeaturePython)
  n = 1
  ref = Be_element
FEATURE [App::DocumentObjectGroupPython] O_element011  label="O_element : 005"  # scripted group (container) (typed FeaturePython)
  n = 1
  ref = O_element
FEATURE [App::DocumentObjectGroupPython] G4_BERYLLIUM_OXIDE  # scripted group (container) (typed FeaturePython)
  Dunit = g/cm3
  Dvalue = 3.01
  Group = -> [Be_element001,O_element011]
  conduct = 2
  density = 1
  expand = 3
  formula = G4_BERYLLIUM_OXIDE
  name = G4_BERYLLIUM_OXIDE
  specific = 4
FEATURE [App::DocumentObjectGroupPython] Bi_element001  label="Bi_element : 4"  # scripted group (container) (typed FeaturePython)
  n = 4
  ref = Bi_element
FEATURE [App::DocumentObjectGroupPython] Ge_element001  label="Ge_element : 3"  # scripted group (container) (typed FeaturePython)
  n = 3
  ref = Ge_element
FEATURE [App::DocumentObjectGroupPython] O_element012  label="O_element : 12"  # scripted group (container) (typed FeaturePython)
  n = 12
  ref = O_element
FEATURE [App::DocumentObjectGroupPython] G4_BGO  # scripted group (container) (typed FeaturePython)
  Dunit = g/cm3
  Dvalue = 7.13
  Group = -> [Bi_element001,Ge_element001,O_element012]
  conduct = 2
  density = 1
  expand = 3
  formula = G4_BGO
  name = G4_BGO
  specific = 4
FEATURE [App::DocumentObjectGroupPython] H_element014  label="H_element : 0.102"  # scripted group (container) (typed FeaturePython)
  n = 0.102
FEATURE [App::DocumentObjectGroupPython] C_element014  label="C_element : 0.110"  # scripted group (container) (typed FeaturePython)
  n = 0.11
FEATURE [App::DocumentObjectGroupPython] N_element009  label="N_element : 0.033"  # scripted group (container) (typed FeaturePython)
  n = 0.033
FEATURE [App::DocumentObjectGroupPython] O_element013  label="O_element : 0.745"  # scripted group (container) (typed FeaturePython)
  n = 0.745
FEATURE [App::DocumentObjectGroupPython] Na_element002  label="Na_element : 0.002"  # scripted group (container) (typed FeaturePython)
  n = 0.001
FEATURE [App::DocumentObjectGroupPython] P_element001  label="P_element : 0.001"  # scripted group (container) (typed FeaturePython)
  n = 0.001
FEATURE [App::DocumentObjectGroupPython] S_element003  label="S_element : 0.002"  # scripted group (container) (typed FeaturePython)
  n = 0.002
FEATURE [App::DocumentObjectGroupPython] Cl_element002  label="Cl_element : 0.003"  # scripted group (container) (typed FeaturePython)
  n = 0.003
FEATURE [App::DocumentObjectGroupPython] K_element001  label="K_element : 0.002"  # scripted group (container) (typed FeaturePython)
  n = 0.002
FEATURE [App::DocumentObjectGroupPython] Fe_element001  label="Fe_element : 0.001"  # scripted group (container) (typed FeaturePython)
  n = 0.001
FEATURE [App::DocumentObjectGroupPython] G4_BLOOD_ICRP  # scripted group (container) (typed FeaturePython)
  Dunit = g/cm3
  Dvalue = 1.06
  Group = -> [H_element014,C_element014,N_element009,O_element013,Na_element002,P_element001,S_element003,Cl_element002,K_element001,Fe_element001]
  conduct = 2
  density = 1
  expand = 3
  formula = G4_BLOOD_ICRP
  name = G4_BLOOD_ICRP
  specific = 4
FEATURE [App::DocumentObjectGroupPython] H_element015  label="H_element : 0.064"  # scripted group (container) (typed FeaturePython)
  n = 0.064
FEATURE [App::DocumentObjectGroupPython] C_element015  label="C_element : 0.278"  # scripted group (container) (typed FeaturePython)
  n = 0.278
FEATURE [App::DocumentObjectGroupPython] N_element010  label="N_element : 0.027"  # scripted group (container) (typed FeaturePython)
  n = 0.027
FEATURE [App::DocumentObjectGroupPython] O_element014  label="O_element : 0.410"  # scripted group (container) (typed FeaturePython)
  n = 0.41
FEATURE [App::DocumentObjectGroupPython] Mg_element001  label="Mg_element : 0.002"  # scripted group (container) (typed FeaturePython)
  n = 0.002
FEATURE [App::DocumentObjectGroupPython] P_element002  label="P_element : 0.070"  # scripted group (container) (typed FeaturePython)
  n = 0.07
FEATURE [App::DocumentObjectGroupPython] S_element004  label="S_element : 0.003"  # scripted group (container) (typed FeaturePython)
  n = 0.002
FEATURE [App::DocumentObjectGroupPython] Ca_element003  label="Ca_element : 0.147"  # scripted group (container) (typed FeaturePython)
  n = 0.147
FEATURE [App::DocumentObjectGroupPython] G4_BONE_COMPACT_ICRU  # scripted group (container) (typed FeaturePython)
  Dunit = g/cm3
  Dvalue = 1.85
  Group = -> [H_element015,C_element015,N_element010,O_element014,Mg_element001,P_element002,S_element004,Ca_element003]
  conduct = 2
  density = 1
  expand = 3
  formula = G4_BONE_COMPACT_ICRU
  name = G4_BONE_COMPACT_ICRU
  specific = 4
FEATURE [App::DocumentObjectGroupPython] H_element016  label="H_element : 0.034"  # scripted group (container) (typed FeaturePython)
  n = 0.034
FEATURE [App::DocumentObjectGroupPython] C_element016  label="C_element : 0.155"  # scripted group (container) (typed FeaturePython)
  n = 0.155
FEATURE [App::DocumentObjectGroupPython] N_element011  label="N_element : 0.042"  # scripted group (container) (typed FeaturePython)
  n = 0.042
FEATURE [App::DocumentObjectGroupPython] O_element015  label="O_element : 0.435"  # scripted group (container) (typed FeaturePython)
  n = 0.435
FEATURE [App::DocumentObjectGroupPython] Na_element003  label="Na_element : 0.003"  # scripted group (container) (typed FeaturePython)
  n = 0.001
FEATURE [App::DocumentObjectGroupPython] Mg_element002  label="Mg_element : 0.003"  # scripted group (container) (typed FeaturePython)
  n = 0.002
FEATURE [App::DocumentObjectGroupPython] P_element003  label="P_element : 0.103"  # scripted group (container) (typed FeaturePython)
  n = 0.103
FEATURE [App::DocumentObjectGroupPython] S_element005  label="S_element : 0.004"  # scripted group (container) (typed FeaturePython)
  n = 0.003
FEATURE [App::DocumentObjectGroupPython] Ca_element004  label="Ca_element : 0.225"  # scripted group (container) (typed FeaturePython)
  n = 0.225
FEATURE [App::DocumentObjectGroupPython] G4_BONE_CORTICAL_ICRP  # scripted group (container) (typed FeaturePython)
  Dunit = g/cm3
  Dvalue = 1.92
  Group = -> [H_element016,C_element016,N_element011,O_element015,Na_element003,Mg_element002,P_element003,S_element005,Ca_element004]
  conduct = 2
  density = 1
  expand = 3
  formula = G4_BONE_CORTICAL_ICRP
  name = G4_BONE_CORTICAL_ICRP
  specific = 4
FEATURE [App::DocumentObjectGroupPython] B_element001  label="B_element : 4"  # scripted group (container) (typed FeaturePython)
  n = 4
  ref = B_element
FEATURE [App::DocumentObjectGroupPython] C_element017  label="C_element : 1"  # scripted group (container) (typed FeaturePython)
  n = 1
  ref = C_element
FEATURE [App::DocumentObjectGroupPython] G4_BORON_CARBIDE  # scripted group (container) (typed FeaturePython)
  Dunit = g/cm3
  Dvalue = 2.52
  Group = -> [B_element001,C_element017]
  conduct = 2
  density = 1
  expand = 3
  formula = G4_BORON_CARBIDE
  name = G4_BORON_CARBIDE
  specific = 4
FEATURE [App::DocumentObjectGroupPython] B_element002  label="B_element : 2"  # scripted group (container) (typed FeaturePython)
  n = 2
  ref = B_element
FEATURE [App::DocumentObjectGroupPython] O_element016  label="O_element : 006"  # scripted group (container) (typed FeaturePython)
  n = 3
  ref = O_element
FEATURE [App::DocumentObjectGroupPython] G4_BORON_OXIDE  # scripted group (container) (typed FeaturePython)
  Dunit = g/cm3
  Dvalue = 1.812
  Group = -> [B_element002,O_element016]
  conduct = 2
  density = 1
  expand = 3
  formula = G4_BORON_OXIDE
  name = G4_BORON_OXIDE
  specific = 4
FEATURE [App::DocumentObjectGroupPython] H_element017  label="H_element : 0.107"  # scripted group (container) (typed FeaturePython)
  n = 0.107
FEATURE [App::DocumentObjectGroupPython] C_element018  label="C_element : 0.145"  # scripted group (container) (typed FeaturePython)
  n = 0.145
FEATURE [App::DocumentObjectGroupPython] N_element012  label="N_element : 0.022"  # scripted group (container) (typed FeaturePython)
  n = 0.022
FEATURE [App::DocumentObjectGroupPython] O_element017  label="O_element : 0.712"  # scripted group (container) (typed FeaturePython)
  n = 0.712
FEATURE [App::DocumentObjectGroupPython] Na_element004  label="Na_element : 0.004"  # scripted group (container) (typed FeaturePython)
  n = 0.002
FEATURE [App::DocumentObjectGroupPython] P_element004  label="P_element : 0.004"  # scripted group (container) (typed FeaturePython)
  n = 0.004
FEATURE [App::DocumentObjectGroupPython] S_element006  label="S_element : 0.005"  # scripted group (container) (typed FeaturePython)
  n = 0.002
FEATURE [App::DocumentObjectGroupPython] Cl_element003  label="Cl_element : 0.004"  # scripted group (container) (typed FeaturePython)
  n = 0.003
FEATURE [App::DocumentObjectGroupPython] K_element002  label="K_element : 0.003"  # scripted group (container) (typed FeaturePython)
  n = 0.003
FEATURE [App::DocumentObjectGroupPython] G4_BRAIN_ICRP  # scripted group (container) (typed FeaturePython)
  Dunit = g/cm3
  Dvalue = 1.04
  Group = -> [H_element017,C_element018,N_element012,O_element017,Na_element004,P_element004,S_element006,Cl_element003,K_element002]
  conduct = 2
  density = 1
  expand = 3
  formula = G4_BRAIN_ICRP
  name = G4_BRAIN_ICRP
  specific = 4
FEATURE [App::DocumentObjectGroupPython] C_element019  label="C_element : 4"  # scripted group (container) (typed FeaturePython)
  n = 4
  ref = C_element
FEATURE [App::DocumentObjectGroupPython] H_element018  label="H_element : 010"  # scripted group (container) (typed FeaturePython)
  n = 10
  ref = H_element
FEATURE [App::DocumentObjectGroupPython] G4_BUTANE  # scripted group (container) (typed FeaturePython)
  Dunit = g/cm3
  Dvalue = 0.00249343
  Group = -> [C_element019,H_element018]
  conduct = 2
  density = 1
  expand = 3
  formula = G4_BUTANE
  name = G4_BUTANE
  specific = 4
FEATURE [App::DocumentObjectGroupPython] C_element020  label="C_element : 008"  # scripted group (container) (typed FeaturePython)
  n = 4
  ref = C_element
FEATURE [App::DocumentObjectGroupPython] H_element019  label="H_element : 011"  # scripted group (container) (typed FeaturePython)
  n = 10
  ref = H_element
FEATURE [App::DocumentObjectGroupPython] O_element018  label="O_element : 007"  # scripted group (container) (typed FeaturePython)
  n = 1
  ref = O_element
FEATURE [App::DocumentObjectGroupPython] G4_N_BUTYL_ALCOHOL  label="G4_N-BUTYL_ALCOHOL"  # scripted group (container) (typed FeaturePython)
  Dunit = g/cm3
  Dvalue = 0.8098
  Group = -> [C_element020,H_element019,O_element018]
  conduct = 2
  density = 1
  expand = 3
  formula = G4_N-BUTYL_ALCOHOL
  name = G4_N-BUTYL_ALCOHOL
  specific = 4
FEATURE [App::DocumentObjectGroupPython] H_element020  label="H_element : 0.025"  # scripted group (container) (typed FeaturePython)
  n = 0.02468
FEATURE [App::DocumentObjectGroupPython] C_element021  label="C_element : 0.502"  # scripted group (container) (typed FeaturePython)
  n = 0.501611
FEATURE [App::DocumentObjectGroupPython] O_element019  label="O_element : 0.005"  # scripted group (container) (typed FeaturePython)
  n = 0.004527
FEATURE [App::DocumentObjectGroupPython] F_element004  label="F_element : 0.465"  # scripted group (container) (typed FeaturePython)
  n = 0.465209
FEATURE [App::DocumentObjectGroupPython] Si_element001  label="Si_element : 0.004"  # scripted group (container) (typed FeaturePython)
  n = 0.003973
FEATURE [App::DocumentObjectGroupPython] G4_C_552  label="G4_C-552"  # scripted group (container) (typed FeaturePython)
  Dunit = g/cm3
  Dvalue = 1.76
  Group = -> [H_element020,C_element021,O_element019,F_element004,Si_element001]
  conduct = 2
  density = 1
  expand = 3
  formula = G4_C-552
  name = G4_C-552
  specific = 4
FEATURE [App::DocumentObjectGroupPython] Cd_element001  label="Cd_element : 1"  # scripted group (container) (typed FeaturePython)
  n = 1
  ref = Cd_element
FEATURE [App::DocumentObjectGroupPython] Te_element001  label="Te_element : 1"  # scripted group (container) (typed FeaturePython)
  n = 1
  ref = Te_element
FEATURE [App::DocumentObjectGroupPython] G4_CADMIUM_TELLURIDE  # scripted group (container) (typed FeaturePython)
  Dunit = g/cm3
  Dvalue = 6.2
  Group = -> [Cd_element001,Te_element001]
  conduct = 2
  density = 1
  expand = 3
  formula = G4_CADMIUM_TELLURIDE
  name = G4_CADMIUM_TELLURIDE
  specific = 4
FEATURE [App::DocumentObjectGroupPython] Cd_element002  label="Cd_element : 002"  # scripted group (container) (typed FeaturePython)
  n = 1
  ref = Cd_element
FEATURE [App::DocumentObjectGroupPython] W_element001  label="W_element : 1"  # scripted group (container) (typed FeaturePython)
  n = 1
  ref = W_element
FEATURE [App::DocumentObjectGroupPython] O_element020  label="O_element : 008"  # scripted group (container) (typed FeaturePython)
  n = 4
  ref = O_element
FEATURE [App::DocumentObjectGroupPython] G4_CADMIUM_TUNGSTATE  # scripted group (container) (typed FeaturePython)
  Dunit = g/cm3
  Dvalue = 7.9
  Group = -> [Cd_element002,W_element001,O_element020]
  conduct = 2
  density = 1
  expand = 3
  formula = G4_CADMIUM_TUNGSTATE
  name = G4_CADMIUM_TUNGSTATE
  specific = 4
FEATURE [App::DocumentObjectGroupPython] Ca_element005  label="Ca_element : 1"  # scripted group (container) (typed FeaturePython)
  n = 1
  ref = Ca_element
FEATURE [App::DocumentObjectGroupPython] C_element022  label="C_element : 009"  # scripted group (container) (typed FeaturePython)
  n = 1
  ref = C_element
FEATURE [App::DocumentObjectGroupPython] O_element021  label="O_element : 009"  # scripted group (container) (typed FeaturePython)
  n = 3
  ref = O_element
FEATURE [App::DocumentObjectGroupPython] G4_CALCIUM_CARBONATE  # scripted group (container) (typed FeaturePython)
  Dunit = g/cm3
  Dvalue = 2.8
  Group = -> [Ca_element005,C_element022,O_element021]
  conduct = 2
  density = 1
  expand = 3
  formula = G4_CALCIUM_CARBONATE
  name = G4_CALCIUM_CARBONATE
  specific = 4
FEATURE [App::DocumentObjectGroupPython] Ca_element006  label="Ca_element : 002"  # scripted group (container) (typed FeaturePython)
  n = 1
  ref = Ca_element
FEATURE [App::DocumentObjectGroupPython] F_element005  label="F_element : 003"  # scripted group (container) (typed FeaturePython)
  n = 2
  ref = F_element
FEATURE [App::DocumentObjectGroupPython] G4_CALCIUM_FLUORIDE  # scripted group (container) (typed FeaturePython)
  Dunit = g/cm3
  Dvalue = 3.18
  Group = -> [Ca_element006,F_element005]
  conduct = 2
  density = 1
  expand = 3
  formula = G4_CALCIUM_FLUORIDE
  name = G4_CALCIUM_FLUORIDE
  specific = 4
FEATURE [App::DocumentObjectGroupPython] Ca_element007  label="Ca_element : 003"  # scripted group (container) (typed FeaturePython)
  n = 1
  ref = Ca_element
FEATURE [App::DocumentObjectGroupPython] O_element022  label="O_element : 010"  # scripted group (container) (typed FeaturePython)
  n = 1
  ref = O_element
FEATURE [App::DocumentObjectGroupPython] G4_CALCIUM_OXIDE  # scripted group (container) (typed FeaturePython)
  Dunit = g/cm3
  Dvalue = 3.3
  Group = -> [Ca_element007,O_element022]
  conduct = 2
  density = 1
  expand = 3
  formula = G4_CALCIUM_OXIDE
  name = G4_CALCIUM_OXIDE
  specific = 4
FEATURE [App::DocumentObjectGroupPython] Ca_element008  label="Ca_element : 004"  # scripted group (container) (typed FeaturePython)
  n = 1
  ref = Ca_element
FEATURE [App::DocumentObjectGroupPython] S_element007  label="S_element : 002"  # scripted group (container) (typed FeaturePython)
  n = 1
  ref = S_element
FEATURE [App::DocumentObjectGroupPython] O_element023  label="O_element : 011"  # scripted group (container) (typed FeaturePython)
  n = 4
  ref = O_element
FEATURE [App::DocumentObjectGroupPython] G4_CALCIUM_SULFATE  # scripted group (container) (typed FeaturePython)
  Dunit = g/cm3
  Dvalue = 2.96
  Group = -> [Ca_element008,S_element007,O_element023]
  conduct = 2
  density = 1
  expand = 3
  formula = G4_CALCIUM_SULFATE
  name = G4_CALCIUM_SULFATE
  specific = 4
FEATURE [App::DocumentObjectGroupPython] Ca_element009  label="Ca_element : 005"  # scripted group (container) (typed FeaturePython)
  n = 1
  ref = Ca_element
FEATURE [App::DocumentObjectGroupPython] W_element002  label="W_element : 002"  # scripted group (container) (typed FeaturePython)
  n = 1
  ref = W_element
FEATURE [App::DocumentObjectGroupPython] O_element024  label="O_element : 012"  # scripted group (container) (typed FeaturePython)
  n = 4
  ref = O_element
FEATURE [App::DocumentObjectGroupPython] G4_CALCIUM_TUNGSTATE  # scripted group (container) (typed FeaturePython)
  Dunit = g/cm3
  Dvalue = 6.062
  Group = -> [Ca_element009,W_element002,O_element024]
  conduct = 2
  density = 1
  expand = 3
  formula = G4_CALCIUM_TUNGSTATE
  name = G4_CALCIUM_TUNGSTATE
  specific = 4
FEATURE [App::DocumentObjectGroupPython] C_element023  label="C_element : 010"  # scripted group (container) (typed FeaturePython)
  n = 1
  ref = C_element
FEATURE [App::DocumentObjectGroupPython] O_element025  label="O_element : 013"  # scripted group (container) (typed FeaturePython)
  n = 2
  ref = O_element
FEATURE [App::DocumentObjectGroupPython] G4_CARBON_DIOXIDE  # scripted group (container) (typed FeaturePython)
  Dunit = g/cm3
  Dvalue = 0.00184212
  Group = -> [C_element023,O_element025]
  conduct = 2
  density = 1
  expand = 3
  formula = G4_CARBON_DIOXIDE
  name = G4_CARBON_DIOXIDE
  specific = 4
FEATURE [App::DocumentObjectGroupPython] C_element024  label="C_element : 011"  # scripted group (container) (typed FeaturePython)
  n = 1
  ref = C_element
FEATURE [App::DocumentObjectGroupPython] Cl_element004  label="Cl_element : 4"  # scripted group (container) (typed FeaturePython)
  n = 4
  ref = Cl_element
FEATURE [App::DocumentObjectGroupPython] G4_CARBON_TETRACHLORIDE  # scripted group (container) (typed FeaturePython)
  Dunit = g/cm3
  Dvalue = 1.594
  Group = -> [C_element024,Cl_element004]
  conduct = 2
  density = 1
  expand = 3
  formula = G4_CARBON_TETRACHLORIDE
  name = G4_CARBON_TETRACHLORIDE
  specific = 4
FEATURE [App::DocumentObjectGroupPython] C_element025  label="C_element : 012"  # scripted group (container) (typed FeaturePython)
  n = 6
  ref = C_element
FEATURE [App::DocumentObjectGroupPython] H_element021  label="H_element : 012"  # scripted group (container) (typed FeaturePython)
  n = 10
  ref = H_element
FEATURE [App::DocumentObjectGroupPython] O_element026  label="O_element : 5"  # scripted group (container) (typed FeaturePython)
  n = 5
  ref = O_element
FEATURE [App::DocumentObjectGroupPython] G4_CELLULOSE_CELLOPHANE  # scripted group (container) (typed FeaturePython)
  Dunit = g/cm3
  Dvalue = 1.42
  Group = -> [C_element025,H_element021,O_element026]
  conduct = 2
  density = 1
  expand = 3
  formula = G4_CELLULOSE_CELLOPHANE
  name = G4_CELLULOSE_CELLOPHANE
  specific = 4
FEATURE [App::DocumentObjectGroupPython] H_element022  label="H_element : 0.067"  # scripted group (container) (typed FeaturePython)
  n = 0.067125
FEATURE [App::DocumentObjectGroupPython] C_element026  label="C_element : 0.545"  # scripted group (container) (typed FeaturePython)
  n = 0.545403
FEATURE [App::DocumentObjectGroupPython] O_element027  label="O_element : 0.387"  # scripted group (container) (typed FeaturePython)
  n = 0.387472
FEATURE [App::DocumentObjectGroupPython] G4_CELLULOSE_BUTYRATE  # scripted group (container) (typed FeaturePython)
  Dunit = g/cm3
  Dvalue = 1.2
  Group = -> [H_element022,C_element026,O_element027]
  conduct = 2
  density = 1
  expand = 3
  formula = G4_CELLULOSE_BUTYRATE
  name = G4_CELLULOSE_BUTYRATE
  specific = 4
FEATURE [App::DocumentObjectGroupPython] H_element023  label="H_element : 0.029"  # scripted group (container) (typed FeaturePython)
  n = 0.029216
FEATURE [App::DocumentObjectGroupPython] C_element027  label="C_element : 0.271"  # scripted group (container) (typed FeaturePython)
  n = 0.271296
FEATURE [App::DocumentObjectGroupPython] N_element013  label="N_element : 0.121"  # scripted group (container) (typed FeaturePython)
  n = 0.121276
FEATURE [App::DocumentObjectGroupPython] O_element028  label="O_element : 0.578"  # scripted group (container) (typed FeaturePython)
  n = 0.578212
FEATURE [App::DocumentObjectGroupPython] G4_CELLULOSE_NITRATE  # scripted group (container) (typed FeaturePython)
  Dunit = g/cm3
  Dvalue = 1.49
  Group = -> [H_element023,C_element027,N_element013,O_element028]
  conduct = 2
  density = 1
  expand = 3
  formula = G4_CELLULOSE_NITRATE
  name = G4_CELLULOSE_NITRATE
  specific = 4
FEATURE [App::DocumentObjectGroupPython] H_element024  label="H_element : 0.108"  # scripted group (container) (typed FeaturePython)
  n = 0.107596
FEATURE [App::DocumentObjectGroupPython] N_element014  label="N_element : 0.001"  # scripted group (container) (typed FeaturePython)
  n = 0.0008
FEATURE [App::DocumentObjectGroupPython] O_element029  label="O_element : 0.875"  # scripted group (container) (typed FeaturePython)
  n = 0.874976
FEATURE [App::DocumentObjectGroupPython] S_element008  label="S_element : 0.015"  # scripted group (container) (typed FeaturePython)
  n = 0.014627
FEATURE [App::DocumentObjectGroupPython] Ce_element001  label="Ce_element : 0.002"  # scripted group (container) (typed FeaturePython)
  n = 0.002001
FEATURE [App::DocumentObjectGroupPython] G4_CERIC_SULFATE  # scripted group (container) (typed FeaturePython)
  Dunit = g/cm3
  Dvalue = 1.03
  Group = -> [H_element024,N_element014,O_element029,S_element008,Ce_element001]
  conduct = 2
  density = 1
  expand = 3
  formula = G4_CERIC_SULFATE
  name = G4_CERIC_SULFATE
  specific = 4
FEATURE [App::DocumentObjectGroupPython] Cs_element001  label="Cs_element : 1"  # scripted group (container) (typed FeaturePython)
  n = 1
  ref = Cs_element
FEATURE [App::DocumentObjectGroupPython] F_element006  label="F_element : 1"  # scripted group (container) (typed FeaturePython)
  n = 1
  ref = F_element
FEATURE [App::DocumentObjectGroupPython] G4_CESIUM_FLUORIDE  # scripted group (container) (typed FeaturePython)
  Dunit = g/cm3
  Dvalue = 4.115
  Group = -> [Cs_element001,F_element006]
  conduct = 2
  density = 1
  expand = 3
  formula = G4_CESIUM_FLUORIDE
  name = G4_CESIUM_FLUORIDE
  specific = 4
FEATURE [App::DocumentObjectGroupPython] Cs_element002  label="Cs_element : 002"  # scripted group (container) (typed FeaturePython)
  n = 1
  ref = Cs_element
FEATURE [App::DocumentObjectGroupPython] I_element001  label="I_element : 1"  # scripted group (container) (typed FeaturePython)
  n = 1
  ref = I_element
FEATURE [App::DocumentObjectGroupPython] G4_CESIUM_IODIDE  # scripted group (container) (typed FeaturePython)
  Dunit = g/cm3
  Dvalue = 4.51
  Group = -> [Cs_element002,I_element001]
  conduct = 2
  density = 1
  expand = 3
  formula = G4_CESIUM_IODIDE
  name = G4_CESIUM_IODIDE
  specific = 4
FEATURE [App::DocumentObjectGroupPython] C_element028  label="C_element : 013"  # scripted group (container) (typed FeaturePython)
  n = 6
  ref = C_element
FEATURE [App::DocumentObjectGroupPython] H_element025  label="H_element : 013"  # scripted group (container) (typed FeaturePython)
  n = 5
  ref = H_element
FEATURE [App::DocumentObjectGroupPython] Cl_element005  label="Cl_element : 1"  # scripted group (container) (typed FeaturePython)
  n = 1
  ref = Cl_element
FEATURE [App::DocumentObjectGroupPython] G4_CHLOROBENZENE  # scripted group (container) (typed FeaturePython)
  Dunit = g/cm3
  Dvalue = 1.1058
  Group = -> [C_element028,H_element025,Cl_element005]
  conduct = 2
  density = 1
  expand = 3
  formula = G4_CHLOROBENZENE
  name = G4_CHLOROBENZENE
  specific = 4
FEATURE [App::DocumentObjectGroupPython] C_element029  label="C_element : 014"  # scripted group (container) (typed FeaturePython)
  n = 1
  ref = C_element
FEATURE [App::DocumentObjectGroupPython] H_element026  label="H_element : 1"  # scripted group (container) (typed FeaturePython)
  n = 1
  ref = H_element
FEATURE [App::DocumentObjectGroupPython] Cl_element006  label="Cl_element : 3"  # scripted group (container) (typed FeaturePython)
  n = 3
  ref = Cl_element
FEATURE [App::DocumentObjectGroupPython] G4_CHLOROFORM  # scripted group (container) (typed FeaturePython)
  Dunit = g/cm3
  Dvalue = 1.4832
  Group = -> [C_element029,H_element026,Cl_element006]
  conduct = 2
  density = 1
  expand = 3
  formula = G4_CHLOROFORM
  name = G4_CHLOROFORM
  specific = 4
FEATURE [App::DocumentObjectGroupPython] H_element027  label="H_element : 0.010"  # scripted group (container) (typed FeaturePython)
  n = 0.01
FEATURE [App::DocumentObjectGroupPython] C_element030  label="C_element : 0.001"  # scripted group (container) (typed FeaturePython)
  n = 0.001
FEATURE [App::DocumentObjectGroupPython] O_element030  label="O_element : 0.529"  # scripted group (container) (typed FeaturePython)
  n = 0.529107
FEATURE [App::DocumentObjectGroupPython] Na_element005  label="Na_element : 0.016"  # scripted group (container) (typed FeaturePython)
  n = 0.016
FEATURE [App::DocumentObjectGroupPython] Mg_element003  label="Mg_element : 0.004"  # scripted group (container) (typed FeaturePython)
  n = 0.002
FEATURE [App::DocumentObjectGroupPython] Al_element002  label="Al_element : 0.034"  # scripted group (container) (typed FeaturePython)
  n = 0.033872
FEATURE [App::DocumentObjectGroupPython] Si_element002  label="Si_element : 0.337"  # scripted group (container) (typed FeaturePython)
  n = 0.337021
FEATURE [App::DocumentObjectGroupPython] K_element003  label="K_element : 0.013"  # scripted group (container) (typed FeaturePython)
  n = 0.013
FEATURE [App::DocumentObjectGroupPython] Ca_element010  label="Ca_element : 0.044"  # scripted group (container) (typed FeaturePython)
  n = 0.044
FEATURE [App::DocumentObjectGroupPython] Fe_element002  label="Fe_element : 0.014"  # scripted group (container) (typed FeaturePython)
  n = 0.014
FEATURE [App::DocumentObjectGroupPython] G4_CONCRETE  # scripted group (container) (typed FeaturePython)
  Dunit = g/cm3
  Dvalue = 2.3
  Group = -> [H_element027,C_element030,O_element030,Na_element005,Mg_element003,Al_element002,Si_element002,K_element003,Ca_element010,Fe_element002]
  conduct = 2
  density = 1
  expand = 3
  formula = G4_CONCRETE
  name = G4_CONCRETE
  specific = 4
FEATURE [App::DocumentObjectGroupPython] C_element031  label="C_element : 015"  # scripted group (container) (typed FeaturePython)
  n = 6
  ref = C_element
FEATURE [App::DocumentObjectGroupPython] H_element028  label="H_element : 12"  # scripted group (container) (typed FeaturePython)
  n = 12
  ref = H_element
FEATURE [App::DocumentObjectGroupPython] G4_CYCLOHEXANE  # scripted group (container) (typed FeaturePython)
  Dunit = g/cm3
  Dvalue = 0.779
  Group = -> [C_element031,H_element028]
  conduct = 2
  density = 1
  expand = 3
  formula = G4_CYCLOHEXANE
  name = G4_CYCLOHEXANE
  specific = 4
FEATURE [App::DocumentObjectGroupPython] C_element032  label="C_element : 016"  # scripted group (container) (typed FeaturePython)
  n = 6
  ref = C_element
FEATURE [App::DocumentObjectGroupPython] H_element029  label="H_element : 4"  # scripted group (container) (typed FeaturePython)
  n = 4
  ref = H_element
FEATURE [App::DocumentObjectGroupPython] Cl_element007  label="Cl_element : 2"  # scripted group (container) (typed FeaturePython)
  n = 2
  ref = Cl_element
FEATURE [App::DocumentObjectGroupPython] G4_1_2_DICHLOROBENZENE  label="G4_1.2-DICHLOROBENZENE"  # scripted group (container) (typed FeaturePython)
  Dunit = g/cm3
  Dvalue = 1.3048
  Group = -> [C_element032,H_element029,Cl_element007]
  conduct = 2
  density = 1
  expand = 3
  formula = G4_1.2-DICHLOROBENZENE
  name = G4_1.2-DICHLOROBENZENE
  specific = 4
FEATURE [App::DocumentObjectGroupPython] C_element033  label="C_element : 017"  # scripted group (container) (typed FeaturePython)
  n = 4
  ref = C_element
FEATURE [App::DocumentObjectGroupPython] H_element030  label="H_element : 8"  # scripted group (container) (typed FeaturePython)
  n = 8
  ref = H_element
FEATURE [App::DocumentObjectGroupPython] O_element031  label="O_element : 014"  # scripted group (container) (typed FeaturePython)
  n = 1
  ref = O_element
FEATURE [App::DocumentObjectGroupPython] Cl_element008  label="Cl_element : 005"  # scripted group (container) (typed FeaturePython)
  n = 2
  ref = Cl_element
FEATURE [App::DocumentObjectGroupPython] G4_DICHLORODIETHYL_ETHER  # scripted group (container) (typed FeaturePython)
  Dunit = g/cm3
  Dvalue = 1.2199
  Group = -> [C_element033,H_element030,O_element031,Cl_element008]
  conduct = 2
  density = 1
  expand = 3
  formula = G4_DICHLORODIETHYL_ETHER
  name = G4_DICHLORODIETHYL_ETHER
  specific = 4
FEATURE [App::DocumentObjectGroupPython] C_element034  label="C_element : 018"  # scripted group (container) (typed FeaturePython)
  n = 2
  ref = C_element
FEATURE [App::DocumentObjectGroupPython] H_element031  label="H_element : 014"  # scripted group (container) (typed FeaturePython)
  n = 4
  ref = H_element
FEATURE [App::DocumentObjectGroupPython] Cl_element009  label="Cl_element : 006"  # scripted group (container) (typed FeaturePython)
  n = 2
  ref = Cl_element
FEATURE [App::DocumentObjectGroupPython] G4_1_2_DICHLOROETHANE  label="G4_1.2-DICHLOROETHANE"  # scripted group (container) (typed FeaturePython)
  Dunit = g/cm3
  Dvalue = 1.2351
  Group = -> [C_element034,H_element031,Cl_element009]
  conduct = 2
  density = 1
  expand = 3
  formula = G4_1.2-DICHLOROETHANE
  name = G4_1.2-DICHLOROETHANE
  specific = 4
FEATURE [App::DocumentObjectGroupPython] C_element035  label="C_element : 019"  # scripted group (container) (typed FeaturePython)
  n = 4
  ref = C_element
FEATURE [App::DocumentObjectGroupPython] H_element032  label="H_element : 015"  # scripted group (container) (typed FeaturePython)
  n = 10
  ref = H_element
FEATURE [App::DocumentObjectGroupPython] O_element032  label="O_element : 015"  # scripted group (container) (typed FeaturePython)
  n = 1
  ref = O_element
FEATURE [App::DocumentObjectGroupPython] G4_DIETHYL_ETHER  # scripted group (container) (typed FeaturePython)
  Dunit = g/cm3
  Dvalue = 0.71378
  Group = -> [C_element035,H_element032,O_element032]
  conduct = 2
  density = 1
  expand = 3
  formula = G4_DIETHYL_ETHER
  name = G4_DIETHYL_ETHER
  specific = 4
FEATURE [App::DocumentObjectGroupPython] C_element036  label="C_element : 020"  # scripted group (container) (typed FeaturePython)
  n = 3
  ref = C_element
FEATURE [App::DocumentObjectGroupPython] H_element033  label="H_element : 016"  # scripted group (container) (typed FeaturePython)
  n = 7
  ref = H_element
FEATURE [App::DocumentObjectGroupPython] N_element015  label="N_element : 008"  # scripted group (container) (typed FeaturePython)
  n = 1
  ref = N_element
FEATURE [App::DocumentObjectGroupPython] O_element033  label="O_element : 016"  # scripted group (container) (typed FeaturePython)
  n = 1
  ref = O_element
FEATURE [App::DocumentObjectGroupPython] G4_N_N_DIMETHYL_FORMAMIDE  label="G4_N.N-DIMETHYL_FORMAMIDE"  # scripted group (container) (typed FeaturePython)
  Dunit = g/cm3
  Dvalue = 0.9487
  Group = -> [C_element036,H_element033,N_element015,O_element033]
  conduct = 2
  density = 1
  expand = 3
  formula = G4_N.N-DIMETHYL_FORMAMIDE
  name = G4_N.N-DIMETHYL_FORMAMIDE
  specific = 4
FEATURE [App::DocumentObjectGroupPython] C_element037  label="C_element : 021"  # scripted group (container) (typed FeaturePython)
  n = 2
  ref = C_element
FEATURE [App::DocumentObjectGroupPython] H_element034  label="H_element : 017"  # scripted group (container) (typed FeaturePython)
  n = 6
  ref = H_element
FEATURE [App::DocumentObjectGroupPython] O_element034  label="O_element : 017"  # scripted group (container) (typed FeaturePython)
  n = 1
  ref = O_element
FEATURE [App::DocumentObjectGroupPython] S_element009  label="S_element : 003"  # scripted group (container) (typed FeaturePython)
  n = 1
  ref = S_element
FEATURE [App::DocumentObjectGroupPython] G4_DIMETHYL_SULFOXIDE  # scripted group (container) (typed FeaturePython)
  Dunit = g/cm3
  Dvalue = 1.1014
  Group = -> [C_element037,H_element034,O_element034,S_element009]
  conduct = 2
  density = 1
  expand = 3
  formula = G4_DIMETHYL_SULFOXIDE
  name = G4_DIMETHYL_SULFOXIDE
  specific = 4
FEATURE [App::DocumentObjectGroupPython] C_element038  label="C_element : 022"  # scripted group (container) (typed FeaturePython)
  n = 2
  ref = C_element
FEATURE [App::DocumentObjectGroupPython] H_element035  label="H_element : 018"  # scripted group (container) (typed FeaturePython)
  n = 6
  ref = H_element
FEATURE [App::DocumentObjectGroupPython] G4_ETHANE  # scripted group (container) (typed FeaturePython)
  Dunit = g/cm3
  Dvalue = 0.00125324
  Group = -> [C_element038,H_element035]
  conduct = 2
  density = 1
  expand = 3
  formula = G4_ETHANE
  name = G4_ETHANE
  specific = 4
FEATURE [App::DocumentObjectGroupPython] C_element039  label="C_element : 023"  # scripted group (container) (typed FeaturePython)
  n = 2
  ref = C_element
FEATURE [App::DocumentObjectGroupPython] H_element036  label="H_element : 019"  # scripted group (container) (typed FeaturePython)
  n = 6
  ref = H_element
FEATURE [App::DocumentObjectGroupPython] O_element035  label="O_element : 018"  # scripted group (container) (typed FeaturePython)
  n = 1
  ref = O_element
FEATURE [App::DocumentObjectGroupPython] G4_ETHYL_ALCOHOL  # scripted group (container) (typed FeaturePython)
  Dunit = g/cm3
  Dvalue = 0.7893
  Group = -> [C_element039,H_element036,O_element035]
  conduct = 2
  density = 1
  expand = 3
  formula = G4_ETHYL_ALCOHOL
  name = G4_ETHYL_ALCOHOL
  specific = 4
FEATURE [App::DocumentObjectGroupPython] H_element037  label="H_element : 0.090"  # scripted group (container) (typed FeaturePython)
  n = 0.090027
FEATURE [App::DocumentObjectGroupPython] C_element040  label="C_element : 0.585"  # scripted group (container) (typed FeaturePython)
  n = 0.585182
FEATURE [App::DocumentObjectGroupPython] O_element036  label="O_element : 0.325"  # scripted group (container) (typed FeaturePython)
  n = 0.324791
FEATURE [App::DocumentObjectGroupPython] G4_ETHYL_CELLULOSE  # scripted group (container) (typed FeaturePython)
  Dunit = g/cm3
  Dvalue = 1.13
  Group = -> [H_element037,C_element040,O_element036]
  conduct = 2
  density = 1
  expand = 3
  formula = G4_ETHYL_CELLULOSE
  name = G4_ETHYL_CELLULOSE
  specific = 4
FEATURE [App::DocumentObjectGroupPython] C_element041  label="C_element : 024"  # scripted group (container) (typed FeaturePython)
  n = 2
  ref = C_element
FEATURE [App::DocumentObjectGroupPython] H_element038  label="H_element : 020"  # scripted group (container) (typed FeaturePython)
  n = 4
  ref = H_element
FEATURE [App::DocumentObjectGroupPython] G4_ETHYLENE  # scripted group (container) (typed FeaturePython)
  Dunit = g/cm3
  Dvalue = 0.00117497
  Group = -> [C_element041,H_element038]
  conduct = 2
  density = 1
  expand = 3
  formula = G4_ETHYLENE
  name = G4_ETHYLENE
  specific = 4
FEATURE [App::DocumentObjectGroupPython] H_element039  label="H_element : 0.096"  # scripted group (container) (typed FeaturePython)
  n = 0.096
FEATURE [App::DocumentObjectGroupPython] C_element042  label="C_element : 0.195"  # scripted group (container) (typed FeaturePython)
  n = 0.195
FEATURE [App::DocumentObjectGroupPython] N_element016  label="N_element : 0.057"  # scripted group (container) (typed FeaturePython)
  n = 0.057
FEATURE [App::DocumentObjectGroupPython] O_element037  label="O_element : 0.646"  # scripted group (container) (typed FeaturePython)
  n = 0.646
FEATURE [App::DocumentObjectGroupPython] Na_element006  label="Na_element : 0.017"  # scripted group (container) (typed FeaturePython)
  n = 0.001
FEATURE [App::DocumentObjectGroupPython] P_element005  label="P_element : 0.104"  # scripted group (container) (typed FeaturePython)
  n = 0.001
FEATURE [App::DocumentObjectGroupPython] S_element010  label="S_element : 0.016"  # scripted group (container) (typed FeaturePython)
  n = 0.003
FEATURE [App::DocumentObjectGroupPython] Cl_element010  label="Cl_element : 0.005"  # scripted group (container) (typed FeaturePython)
  n = 0.001
FEATURE [App::DocumentObjectGroupPython] G4_EYE_LENS_ICRP  # scripted group (container) (typed FeaturePython)
  Dunit = g/cm3
  Dvalue = 1.07
  Group = -> [H_element039,C_element042,N_element016,O_element037,Na_element006,P_element005,S_element010,Cl_element010]
  conduct = 2
  density = 1
  expand = 3
  formula = G4_EYE_LENS_ICRP
  name = G4_EYE_LENS_ICRP
  specific = 4
FEATURE [App::DocumentObjectGroupPython] Fe_element003  label="Fe_element : 2"  # scripted group (container) (typed FeaturePython)
  n = 2
  ref = Fe_element
FEATURE [App::DocumentObjectGroupPython] O_element038  label="O_element : 019"  # scripted group (container) (typed FeaturePython)
  n = 3
  ref = O_element
FEATURE [App::DocumentObjectGroupPython] G4_FERRIC_OXIDE  # scripted group (container) (typed FeaturePython)
  Dunit = g/cm3
  Dvalue = 5.2
  Group = -> [Fe_element003,O_element038]
  conduct = 2
  density = 1
  expand = 3
  formula = G4_FERRIC_OXIDE
  name = G4_FERRIC_OXIDE
  specific = 4
FEATURE [App::DocumentObjectGroupPython] Fe_element004  label="Fe_element : 1"  # scripted group (container) (typed FeaturePython)
  n = 1
  ref = Fe_element
FEATURE [App::DocumentObjectGroupPython] B_element003  label="B_element : 1"  # scripted group (container) (typed FeaturePython)
  n = 1
  ref = B_element
FEATURE [App::DocumentObjectGroupPython] G4_FERROBORIDE  # scripted group (container) (typed FeaturePython)
  Dunit = g/cm3
  Dvalue = 7.15
  Group = -> [Fe_element004,B_element003]
  conduct = 2
  density = 1
  expand = 3
  formula = G4_FERROBORIDE
  name = G4_FERROBORIDE
  specific = 4
FEATURE [App::DocumentObjectGroupPython] Fe_element005  label="Fe_element : 003"  # scripted group (container) (typed FeaturePython)
  n = 1
  ref = Fe_element
FEATURE [App::DocumentObjectGroupPython] O_element039  label="O_element : 020"  # scripted group (container) (typed FeaturePython)
  n = 1
  ref = O_element
FEATURE [App::DocumentObjectGroupPython] G4_FERROUS_OXIDE  # scripted group (container) (typed FeaturePython)
  Dunit = g/cm3
  Dvalue = 5.7
  Group = -> [Fe_element005,O_element039]
  conduct = 2
  density = 1
  expand = 3
  formula = G4_FERROUS_OXIDE
  name = G4_FERROUS_OXIDE
  specific = 4
FEATURE [App::DocumentObjectGroupPython] H_element040  label="H_element : 0.115"  # scripted group (container) (typed FeaturePython)
  n = 0.108259
FEATURE [App::DocumentObjectGroupPython] N_element017  label="N_element : 0.000"  # scripted group (container) (typed FeaturePython)
  n = 2.7e-05
FEATURE [App::DocumentObjectGroupPython] O_element040  label="O_element : 0.879"  # scripted group (container) (typed FeaturePython)
  n = 0.878636
FEATURE [App::DocumentObjectGroupPython] Na_element007  label="Na_element : 0.000"  # scripted group (container) (typed FeaturePython)
  n = 2.2e-05
FEATURE [App::DocumentObjectGroupPython] S_element011  label="S_element : 0.013"  # scripted group (container) (typed FeaturePython)
  n = 0.012968
FEATURE [App::DocumentObjectGroupPython] Cl_element011  label="Cl_element : 0.000"  # scripted group (container) (typed FeaturePython)
  n = 3.4e-05
FEATURE [App::DocumentObjectGroupPython] Fe_element006  label="Fe_element : 0.000"  # scripted group (container) (typed FeaturePython)
  n = 5.4e-05
FEATURE [App::DocumentObjectGroupPython] G4_FERROUS_SULFATE  # scripted group (container) (typed FeaturePython)
  Dunit = g/cm3
  Dvalue = 1.024
  Group = -> [H_element040,N_element017,O_element040,Na_element007,S_element011,Cl_element011,Fe_element006]
  conduct = 2
  density = 1
  expand = 3
  formula = G4_FERROUS_SULFATE
  name = G4_FERROUS_SULFATE
  specific = 4
FEATURE [App::DocumentObjectGroupPython] C_element043  label="C_element : 0.099"  # scripted group (container) (typed FeaturePython)
  n = 0.099335
FEATURE [App::DocumentObjectGroupPython] F_element007  label="F_element : 0.314"  # scripted group (container) (typed FeaturePython)
  n = 0.314247
FEATURE [App::DocumentObjectGroupPython] Cl_element012  label="Cl_element : 0.586"  # scripted group (container) (typed FeaturePython)
  n = 0.586418
FEATURE [App::DocumentObjectGroupPython] G4_FREON_12  label="G4_FREON-12"  # scripted group (container) (typed FeaturePython)
  Dunit = g/cm3
  Dvalue = 1.12
  Group = -> [C_element043,F_element007,Cl_element012]
  conduct = 2
  density = 1
  expand = 3
  formula = G4_FREON-12
  name = G4_FREON-12
  specific = 4
FEATURE [App::DocumentObjectGroupPython] C_element044  label="C_element : 0.057"  # scripted group (container) (typed FeaturePython)
  n = 0.057245
FEATURE [App::DocumentObjectGroupPython] F_element008  label="F_element : 0.181"  # scripted group (container) (typed FeaturePython)
  n = 0.181096
FEATURE [App::DocumentObjectGroupPython] Br_element001  label="Br_element : 0.762"  # scripted group (container) (typed FeaturePython)
  n = 0.761659
FEATURE [App::DocumentObjectGroupPython] G4_FREON_12B2  label="G4_FREON-12B2"  # scripted group (container) (typed FeaturePython)
  Dunit = g/cm3
  Dvalue = 1.8
  Group = -> [C_element044,F_element008,Br_element001]
  conduct = 2
  density = 1
  expand = 3
  formula = G4_FREON-12B2
  name = G4_FREON-12B2
  specific = 4
FEATURE [App::DocumentObjectGroupPython] C_element045  label="C_element : 0.115"  # scripted group (container) (typed FeaturePython)
  n = 0.114983
FEATURE [App::DocumentObjectGroupPython] F_element009  label="F_element : 0.546"  # scripted group (container) (typed FeaturePython)
  n = 0.545621
FEATURE [App::DocumentObjectGroupPython] Cl_element013  label="Cl_element : 0.339"  # scripted group (container) (typed FeaturePython)
  n = 0.339396
FEATURE [App::DocumentObjectGroupPython] G4_FREON_13  label="G4_FREON-13"  # scripted group (container) (typed FeaturePython)
  Dunit = g/cm3
  Dvalue = 0.95
  Group = -> [C_element045,F_element009,Cl_element013]
  conduct = 2
  density = 1
  expand = 3
  formula = G4_FREON-13
  name = G4_FREON-13
  specific = 4
FEATURE [App::DocumentObjectGroupPython] C_element046  label="C_element : 025"  # scripted group (container) (typed FeaturePython)
  n = 1
  ref = C_element
FEATURE [App::DocumentObjectGroupPython] F_element010  label="F_element : 3"  # scripted group (container) (typed FeaturePython)
  n = 3
  ref = F_element
FEATURE [App::DocumentObjectGroupPython] Br_element002  label="Br_element : 1"  # scripted group (container) (typed FeaturePython)
  n = 1
  ref = Br_element
FEATURE [App::DocumentObjectGroupPython] G4_FREON_13B1  label="G4_FREON-13B1"  # scripted group (container) (typed FeaturePython)
  Dunit = g/cm3
  Dvalue = 1.5
  Group = -> [C_element046,F_element010,Br_element002]
  conduct = 2
  density = 1
  expand = 3
  formula = G4_FREON-13B1
  name = G4_FREON-13B1
  specific = 4
FEATURE [App::DocumentObjectGroupPython] C_element047  label="C_element : 0.061"  # scripted group (container) (typed FeaturePython)
  n = 0.061309
FEATURE [App::DocumentObjectGroupPython] F_element011  label="F_element : 0.291"  # scripted group (container) (typed FeaturePython)
  n = 0.290924
FEATURE [App::DocumentObjectGroupPython] I_element002  label="I_element : 0.648"  # scripted group (container) (typed FeaturePython)
  n = 0.647767
FEATURE [App::DocumentObjectGroupPython] G4_FREON_13I1  label="G4_FREON-13I1"  # scripted group (container) (typed FeaturePython)
  Dunit = g/cm3
  Dvalue = 1.8
  Group = -> [C_element047,F_element011,I_element002]
  conduct = 2
  density = 1
  expand = 3
  formula = G4_FREON-13I1
  name = G4_FREON-13I1
  specific = 4
FEATURE [App::DocumentObjectGroupPython] Gd_element001  label="Gd_element : 2"  # scripted group (container) (typed FeaturePython)
  n = 2
  ref = Gd_element
FEATURE [App::DocumentObjectGroupPython] O_element041  label="O_element : 021"  # scripted group (container) (typed FeaturePython)
  n = 2
  ref = O_element
FEATURE [App::DocumentObjectGroupPython] S_element012  label="S_element : 004"  # scripted group (container) (typed FeaturePython)
  n = 1
  ref = S_element
FEATURE [App::DocumentObjectGroupPython] G4_GADOLINIUM_OXYSULFIDE  # scripted group (container) (typed FeaturePython)
  Dunit = g/cm3
  Dvalue = 7.44
  Group = -> [Gd_element001,O_element041,S_element012]
  conduct = 2
  density = 1
  expand = 3
  formula = G4_GADOLINIUM_OXYSULFIDE
  name = G4_GADOLINIUM_OXYSULFIDE
  specific = 4
FEATURE [App::DocumentObjectGroupPython] Ga_element001  label="Ga_element : 1"  # scripted group (container) (typed FeaturePython)
  n = 1
  ref = Ga_element
FEATURE [App::DocumentObjectGroupPython] As_element001  label="As_element : 1"  # scripted group (container) (typed FeaturePython)
  n = 1
  ref = As_element
FEATURE [App::DocumentObjectGroupPython] G4_GALLIUM_ARSENIDE  # scripted group (container) (typed FeaturePython)
  Dunit = g/cm3
  Dvalue = 5.31
  Group = -> [Ga_element001,As_element001]
  conduct = 2
  density = 1
  expand = 3
  formula = G4_GALLIUM_ARSENIDE
  name = G4_GALLIUM_ARSENIDE
  specific = 4
FEATURE [App::DocumentObjectGroupPython] H_element041  label="H_element : 0.081"  # scripted group (container) (typed FeaturePython)
  n = 0.08118
FEATURE [App::DocumentObjectGroupPython] C_element048  label="C_element : 0.416"  # scripted group (container) (typed FeaturePython)
  n = 0.41606
FEATURE [App::DocumentObjectGroupPython] N_element018  label="N_element : 0.111"  # scripted group (container) (typed FeaturePython)
  n = 0.11124
FEATURE [App::DocumentObjectGroupPython] O_element042  label="O_element : 0.381"  # scripted group (container) (typed FeaturePython)
  n = 0.38064
FEATURE [App::DocumentObjectGroupPython] S_element013  label="S_element : 0.011"  # scripted group (container) (typed FeaturePython)
  n = 0.01088
FEATURE [App::DocumentObjectGroupPython] G4_GEL_PHOTO_EMULSION  # scripted group (container) (typed FeaturePython)
  Dunit = g/cm3
  Dvalue = 1.2914
  Group = -> [H_element041,C_element048,N_element018,O_element042,S_element013]
  conduct = 2
  density = 1
  expand = 3
  formula = G4_GEL_PHOTO_EMULSION
  name = G4_GEL_PHOTO_EMULSION
  specific = 4
FEATURE [App::DocumentObjectGroupPython] B_element004  label="B_element : 0.040"  # scripted group (container) (typed FeaturePython)
  n = 0.0400639
FEATURE [App::DocumentObjectGroupPython] O_element043  label="O_element : 0.540"  # scripted group (container) (typed FeaturePython)
  n = 0.539561
FEATURE [App::DocumentObjectGroupPython] Na_element008  label="Na_element : 0.028"  # scripted group (container) (typed FeaturePython)
  n = 0.0281909
FEATURE [App::DocumentObjectGroupPython] Al_element003  label="Al_element : 0.012"  # scripted group (container) (typed FeaturePython)
  n = 0.011644
FEATURE [App::DocumentObjectGroupPython] Si_element003  label="Si_element : 0.377"  # scripted group (container) (typed FeaturePython)
  n = 0.377219
FEATURE [App::DocumentObjectGroupPython] K_element004  label="K_element : 0.014"  # scripted group (container) (typed FeaturePython)
  n = 0.00332099
FEATURE [App::DocumentObjectGroupPython] G4_Pyrex_Glass  # scripted group (container) (typed FeaturePython)
  Dunit = g/cm3
  Dvalue = 2.23
  Group = -> [B_element004,O_element043,Na_element008,Al_element003,Si_element003,K_element004]
  conduct = 2
  density = 1
  expand = 3
  formula = G4_Pyrex_Glass
  name = G4_Pyrex_Glass
  specific = 4
FEATURE [App::DocumentObjectGroupPython] O_element044  label="O_element : 0.156"  # scripted group (container) (typed FeaturePython)
  n = 0.156453
FEATURE [App::DocumentObjectGroupPython] Si_element004  label="Si_element : 0.081"  # scripted group (container) (typed FeaturePython)
  n = 0.080866
FEATURE [App::DocumentObjectGroupPython] Ti_element001  label="Ti_element : 0.008"  # scripted group (container) (typed FeaturePython)
  n = 0.008092
FEATURE [App::DocumentObjectGroupPython] As_element002  label="As_element : 0.003"  # scripted group (container) (typed FeaturePython)
  n = 0.002651
FEATURE [App::DocumentObjectGroupPython] Pb_element001  label="Pb_element : 0.752"  # scripted group (container) (typed FeaturePython)
  n = 0.751938
FEATURE [App::DocumentObjectGroupPython] G4_GLASS_LEAD  # scripted group (container) (typed FeaturePython)
  Dunit = g/cm3
  Dvalue = 6.22
  Group = -> [O_element044,Si_element004,Ti_element001,As_element002,Pb_element001]
  conduct = 2
  density = 1
  expand = 3
  formula = G4_GLASS_LEAD
  name = G4_GLASS_LEAD
  specific = 4
FEATURE [App::DocumentObjectGroupPython] O_element045  label="O_element : 0.460"  # scripted group (container) (typed FeaturePython)
  n = 0.4598
FEATURE [App::DocumentObjectGroupPython] Na_element009  label="Na_element : 0.096"  # scripted group (container) (typed FeaturePython)
  n = 0.0964411
FEATURE [App::DocumentObjectGroupPython] Si_element005  label="Si_element : 0.378"  # scripted group (container) (typed FeaturePython)
  n = 0.336553
FEATURE [App::DocumentObjectGroupPython] Ca_element011  label="Ca_element : 0.107"  # scripted group (container) (typed FeaturePython)
  n = 0.107205
FEATURE [App::DocumentObjectGroupPython] G4_GLASS_PLATE  # scripted group (container) (typed FeaturePython)
  Dunit = g/cm3
  Dvalue = 2.4
  Group = -> [O_element045,Na_element009,Si_element005,Ca_element011]
  conduct = 2
  density = 1
  expand = 3
  formula = G4_GLASS_PLATE
  name = G4_GLASS_PLATE
  specific = 4
FEATURE [App::DocumentObjectGroupPython] C_element049  label="C_element : 026"  # scripted group (container) (typed FeaturePython)
  n = 5
  ref = C_element
FEATURE [App::DocumentObjectGroupPython] H_element042  label="H_element : 021"  # scripted group (container) (typed FeaturePython)
  n = 10
  ref = H_element
FEATURE [App::DocumentObjectGroupPython] N_element019  label="N_element : 2"  # scripted group (container) (typed FeaturePython)
  n = 2
  ref = N_element
FEATURE [App::DocumentObjectGroupPython] O_element046  label="O_element : 022"  # scripted group (container) (typed FeaturePython)
  n = 3
  ref = O_element
FEATURE [App::DocumentObjectGroupPython] G4_GLUTAMINE  # scripted group (container) (typed FeaturePython)
  Dunit = g/cm3
  Dvalue = 1.46
  Group = -> [C_element049,H_element042,N_element019,O_element046]
  conduct = 2
  density = 1
  expand = 3
  formula = G4_GLUTAMINE
  name = G4_GLUTAMINE
  specific = 4
FEATURE [App::DocumentObjectGroupPython] C_element050  label="C_element : 027"  # scripted group (container) (typed FeaturePython)
  n = 3
  ref = C_element
FEATURE [App::DocumentObjectGroupPython] H_element043  label="H_element : 022"  # scripted group (container) (typed FeaturePython)
  n = 8
  ref = H_element
FEATURE [App::DocumentObjectGroupPython] O_element047  label="O_element : 023"  # scripted group (container) (typed FeaturePython)
  n = 3
  ref = O_element
FEATURE [App::DocumentObjectGroupPython] G4_GLYCEROL  # scripted group (container) (typed FeaturePython)
  Dunit = g/cm3
  Dvalue = 1.2613
  Group = -> [C_element050,H_element043,O_element047]
  conduct = 2
  density = 1
  expand = 3
  formula = G4_GLYCEROL
  name = G4_GLYCEROL
  specific = 4
FEATURE [App::DocumentObjectGroupPython] C_element051  label="C_element : 028"  # scripted group (container) (typed FeaturePython)
  n = 5
  ref = C_element
FEATURE [App::DocumentObjectGroupPython] H_element044  label="H_element : 023"  # scripted group (container) (typed FeaturePython)
  n = 5
  ref = H_element
FEATURE [App::DocumentObjectGroupPython] N_element020  label="N_element : 009"  # scripted group (container) (typed FeaturePython)
  n = 5
  ref = N_element
FEATURE [App::DocumentObjectGroupPython] O_element048  label="O_element : 024"  # scripted group (container) (typed FeaturePython)
  n = 1
  ref = O_element
FEATURE [App::DocumentObjectGroupPython] G4_GUANINE  # scripted group (container) (typed FeaturePython)
  Dunit = g/cm3
  Dvalue = 2.2
  Group = -> [C_element051,H_element044,N_element020,O_element048]
  conduct = 2
  density = 1
  expand = 3
  formula = G4_GUANINE
  name = G4_GUANINE
  specific = 4
FEATURE [App::DocumentObjectGroupPython] Ca_element012  label="Ca_element : 006"  # scripted group (container) (typed FeaturePython)
  n = 1
  ref = Ca_element
FEATURE [App::DocumentObjectGroupPython] S_element014  label="S_element : 005"  # scripted group (container) (typed FeaturePython)
  n = 1
  ref = S_element
FEATURE [App::DocumentObjectGroupPython] O_element049  label="O_element : 6"  # scripted group (container) (typed FeaturePython)
  n = 6
  ref = O_element
FEATURE [App::DocumentObjectGroupPython] H_element045  label="H_element : 024"  # scripted group (container) (typed FeaturePython)
  n = 4
  ref = H_element
FEATURE [App::DocumentObjectGroupPython] G4_GYPSUM  # scripted group (container) (typed FeaturePython)
  Dunit = g/cm3
  Dvalue = 2.32
  Group = -> [Ca_element012,S_element014,O_element049,H_element045]
  conduct = 2
  density = 1
  expand = 3
  formula = G4_GYPSUM
  name = G4_GYPSUM
  specific = 4
FEATURE [App::DocumentObjectGroupPython] C_element052  label="C_element : 7"  # scripted group (container) (typed FeaturePython)
  n = 7
  ref = C_element
FEATURE [App::DocumentObjectGroupPython] H_element046  label="H_element : 16"  # scripted group (container) (typed FeaturePython)
  n = 16
  ref = H_element
FEATURE [App::DocumentObjectGroupPython] G4_N_HEPTANE  label="G4_N-HEPTANE"  # scripted group (container) (typed FeaturePython)
  Dunit = g/cm3
  Dvalue = 0.68376
  Group = -> [C_element052,H_element046]
  conduct = 2
  density = 1
  expand = 3
  formula = G4_N-HEPTANE
  name = G4_N-HEPTANE
  specific = 4
FEATURE [App::DocumentObjectGroupPython] C_element053  label="C_element : 029"  # scripted group (container) (typed FeaturePython)
  n = 6
  ref = C_element
FEATURE [App::DocumentObjectGroupPython] H_element047  label="H_element : 14"  # scripted group (container) (typed FeaturePython)
  n = 14
  ref = H_element
FEATURE [App::DocumentObjectGroupPython] G4_N_HEXANE  label="G4_N-HEXANE"  # scripted group (container) (typed FeaturePython)
  Dunit = g/cm3
  Dvalue = 0.6603
  Group = -> [C_element053,H_element047]
  conduct = 2
  density = 1
  expand = 3
  formula = G4_N-HEXANE
  name = G4_N-HEXANE
  specific = 4
FEATURE [App::DocumentObjectGroupPython] C_element054  label="C_element : 22"  # scripted group (container) (typed FeaturePython)
  n = 22
  ref = C_element
FEATURE [App::DocumentObjectGroupPython] H_element048  label="H_element : 025"  # scripted group (container) (typed FeaturePython)
  n = 10
  ref = H_element
FEATURE [App::DocumentObjectGroupPython] N_element021  label="N_element : 010"  # scripted group (container) (typed FeaturePython)
  n = 2
  ref = N_element
FEATURE [App::DocumentObjectGroupPython] O_element050  label="O_element : 025"  # scripted group (container) (typed FeaturePython)
  n = 5
  ref = O_element
FEATURE [App::DocumentObjectGroupPython] G4_KAPTON  # scripted group (container) (typed FeaturePython)
  Dunit = g/cm3
  Dvalue = 1.42
  Group = -> [C_element054,H_element048,N_element021,O_element050]
  conduct = 2
  density = 1
  expand = 3
  formula = G4_KAPTON
  name = G4_KAPTON
  specific = 4
FEATURE [App::DocumentObjectGroupPython] La_element001  label="La_element : 1"  # scripted group (container) (typed FeaturePython)
  n = 1
  ref = La_element
FEATURE [App::DocumentObjectGroupPython] Br_element003  label="Br_element : 002"  # scripted group (container) (typed FeaturePython)
  n = 1
  ref = Br_element
FEATURE [App::DocumentObjectGroupPython] O_element051  label="O_element : 026"  # scripted group (container) (typed FeaturePython)
  n = 1
  ref = O_element
FEATURE [App::DocumentObjectGroupPython] G4_LANTHANUM_OXYBROMIDE  # scripted group (container) (typed FeaturePython)
  Dunit = g/cm3
  Dvalue = 6.28
  Group = -> [La_element001,Br_element003,O_element051]
  conduct = 2
  density = 1
  expand = 3
  formula = G4_LANTHANUM_OXYBROMIDE
  name = G4_LANTHANUM_OXYBROMIDE
  specific = 4
FEATURE [App::DocumentObjectGroupPython] La_element002  label="La_element : 2"  # scripted group (container) (typed FeaturePython)
  n = 2
  ref = La_element
FEATURE [App::DocumentObjectGroupPython] O_element052  label="O_element : 027"  # scripted group (container) (typed FeaturePython)
  n = 2
  ref = O_element
FEATURE [App::DocumentObjectGroupPython] S_element015  label="S_element : 006"  # scripted group (container) (typed FeaturePython)
  n = 1
  ref = S_element
FEATURE [App::DocumentObjectGroupPython] G4_LANTHANUM_OXYSULFIDE  # scripted group (container) (typed FeaturePython)
  Dunit = g/cm3
  Dvalue = 5.86
  Group = -> [La_element002,O_element052,S_element015]
  conduct = 2
  density = 1
  expand = 3
  formula = G4_LANTHANUM_OXYSULFIDE
  name = G4_LANTHANUM_OXYSULFIDE
  specific = 4
FEATURE [App::DocumentObjectGroupPython] O_element053  label="O_element : 0.072"  # scripted group (container) (typed FeaturePython)
  n = 0.071682
FEATURE [App::DocumentObjectGroupPython] Pb_element002  label="Pb_element : 0.928"  # scripted group (container) (typed FeaturePython)
  n = 0.928318
FEATURE [App::DocumentObjectGroupPython] G4_LEAD_OXIDE  # scripted group (container) (typed FeaturePython)
  Dunit = g/cm3
  Dvalue = 9.53
  Group = -> [O_element053,Pb_element002]
  conduct = 2
  density = 1
  expand = 3
  formula = G4_LEAD_OXIDE
  name = G4_LEAD_OXIDE
  specific = 4
FEATURE [App::DocumentObjectGroupPython] Li_element001  label="Li_element : 1"  # scripted group (container) (typed FeaturePython)
  n = 1
  ref = Li_element
FEATURE [App::DocumentObjectGroupPython] N_element022  label="N_element : 011"  # scripted group (container) (typed FeaturePython)
  n = 1
  ref = N_element
FEATURE [App::DocumentObjectGroupPython] H_element049  label="H_element : 026"  # scripted group (container) (typed FeaturePython)
  n = 2
  ref = H_element
FEATURE [App::DocumentObjectGroupPython] G4_LITHIUM_AMIDE  # scripted group (container) (typed FeaturePython)
  Dunit = g/cm3
  Dvalue = 1.178
  Group = -> [Li_element001,N_element022,H_element049]
  conduct = 2
  density = 1
  expand = 3
  formula = G4_LITHIUM_AMIDE
  name = G4_LITHIUM_AMIDE
  specific = 4
FEATURE [App::DocumentObjectGroupPython] Li_element002  label="Li_element : 2"  # scripted group (container) (typed FeaturePython)
  n = 2
  ref = Li_element
FEATURE [App::DocumentObjectGroupPython] C_element055  label="C_element : 030"  # scripted group (container) (typed FeaturePython)
  n = 1
  ref = C_element
FEATURE [App::DocumentObjectGroupPython] O_element054  label="O_element : 028"  # scripted group (container) (typed FeaturePython)
  n = 3
  ref = O_element
FEATURE [App::DocumentObjectGroupPython] G4_LITHIUM_CARBONATE  # scripted group (container) (typed FeaturePython)
  Dunit = g/cm3
  Dvalue = 2.11
  Group = -> [Li_element002,C_element055,O_element054]
  conduct = 2
  density = 1
  expand = 3
  formula = G4_LITHIUM_CARBONATE
  name = G4_LITHIUM_CARBONATE
  specific = 4
FEATURE [App::DocumentObjectGroupPython] Li_element003  label="Li_element : 003"  # scripted group (container) (typed FeaturePython)
  n = 1
  ref = Li_element
FEATURE [App::DocumentObjectGroupPython] F_element012  label="F_element : 004"  # scripted group (container) (typed FeaturePython)
  n = 1
  ref = F_element
FEATURE [App::DocumentObjectGroupPython] G4_LITHIUM_FLUORIDE  # scripted group (container) (typed FeaturePython)
  Dunit = g/cm3
  Dvalue = 2.635
  Group = -> [Li_element003,F_element012]
  conduct = 2
  density = 1
  expand = 3
  formula = G4_LITHIUM_FLUORIDE
  name = G4_LITHIUM_FLUORIDE
  specific = 4
FEATURE [App::DocumentObjectGroupPython] Li_element004  label="Li_element : 004"  # scripted group (container) (typed FeaturePython)
  n = 1
  ref = Li_element
FEATURE [App::DocumentObjectGroupPython] H_element050  label="H_element : 027"  # scripted group (container) (typed FeaturePython)
  n = 1
  ref = H_element
FEATURE [App::DocumentObjectGroupPython] G4_LITHIUM_HYDRIDE  # scripted group (container) (typed FeaturePython)
  Dunit = g/cm3
  Dvalue = 0.82
  Group = -> [Li_element004,H_element050]
  conduct = 2
  density = 1
  expand = 3
  formula = G4_LITHIUM_HYDRIDE
  name = G4_LITHIUM_HYDRIDE
  specific = 4
FEATURE [App::DocumentObjectGroupPython] Li_element005  label="Li_element : 005"  # scripted group (container) (typed FeaturePython)
  n = 1
  ref = Li_element
FEATURE [App::DocumentObjectGroupPython] I_element003  label="I_element : 002"  # scripted group (container) (typed FeaturePython)
  n = 1
  ref = I_element
FEATURE [App::DocumentObjectGroupPython] G4_LITHIUM_IODIDE  # scripted group (container) (typed FeaturePython)
  Dunit = g/cm3
  Dvalue = 3.494
  Group = -> [Li_element005,I_element003]
  conduct = 2
  density = 1
  expand = 3
  formula = G4_LITHIUM_IODIDE
  name = G4_LITHIUM_IODIDE
  specific = 4
FEATURE [App::DocumentObjectGroupPython] Li_element006  label="Li_element : 006"  # scripted group (container) (typed FeaturePython)
  n = 2
  ref = Li_element
FEATURE [App::DocumentObjectGroupPython] O_element055  label="O_element : 029"  # scripted group (container) (typed FeaturePython)
  n = 1
  ref = O_element
FEATURE [App::DocumentObjectGroupPython] G4_LITHIUM_OXIDE  # scripted group (container) (typed FeaturePython)
  Dunit = g/cm3
  Dvalue = 2.013
  Group = -> [Li_element006,O_element055]
  conduct = 2
  density = 1
  expand = 3
  formula = G4_LITHIUM_OXIDE
  name = G4_LITHIUM_OXIDE
  specific = 4
FEATURE [App::DocumentObjectGroupPython] Li_element007  label="Li_element : 007"  # scripted group (container) (typed FeaturePython)
  n = 2
  ref = Li_element
FEATURE [App::DocumentObjectGroupPython] B_element005  label="B_element : 005"  # scripted group (container) (typed FeaturePython)
  n = 4
  ref = B_element
FEATURE [App::DocumentObjectGroupPython] O_element056  label="O_element : 7"  # scripted group (container) (typed FeaturePython)
  n = 7
  ref = O_element
FEATURE [App::DocumentObjectGroupPython] G4_LITHIUM_TETRABORATE  # scripted group (container) (typed FeaturePython)
  Dunit = g/cm3
  Dvalue = 2.44
  Group = -> [Li_element007,B_element005,O_element056]
  conduct = 2
  density = 1
  expand = 3
  formula = G4_LITHIUM_TETRABORATE
  name = G4_LITHIUM_TETRABORATE
  specific = 4
FEATURE [App::DocumentObjectGroupPython] H_element051  label="H_element : 0.105"  # scripted group (container) (typed FeaturePython)
  n = 0.105
FEATURE [App::DocumentObjectGroupPython] C_element056  label="C_element : 0.083"  # scripted group (container) (typed FeaturePython)
  n = 0.083
FEATURE [App::DocumentObjectGroupPython] N_element023  label="N_element : 0.023"  # scripted group (container) (typed FeaturePython)
  n = 0.023
FEATURE [App::DocumentObjectGroupPython] O_element057  label="O_element : 0.779"  # scripted group (container) (typed FeaturePython)
  n = 0.779
FEATURE [App::DocumentObjectGroupPython] Na_element010  label="Na_element : 0.097"  # scripted group (container) (typed FeaturePython)
  n = 0.002
FEATURE [App::DocumentObjectGroupPython] P_element006  label="P_element : 0.105"  # scripted group (container) (typed FeaturePython)
  n = 0.001
FEATURE [App::DocumentObjectGroupPython] S_element016  label="S_element : 0.017"  # scripted group (container) (typed FeaturePython)
  n = 0.002
FEATURE [App::DocumentObjectGroupPython] Cl_element014  label="Cl_element : 0.587"  # scripted group (container) (typed FeaturePython)
  n = 0.003
FEATURE [App::DocumentObjectGroupPython] K_element005  label="K_element : 0.015"  # scripted group (container) (typed FeaturePython)
  n = 0.002
FEATURE [App::DocumentObjectGroupPython] G4_LUNG_ICRP  # scripted group (container) (typed FeaturePython)
  Dunit = g/cm3
  Dvalue = 1.04
  Group = -> [H_element051,C_element056,N_element023,O_element057,Na_element010,P_element006,S_element016,Cl_element014,K_element005]
  conduct = 2
  density = 1
  expand = 3
  formula = G4_LUNG_ICRP
  name = G4_LUNG_ICRP
  specific = 4
FEATURE [App::DocumentObjectGroupPython] H_element052  label="H_element : 0.116"  # scripted group (container) (typed FeaturePython)
  n = 0.114318
FEATURE [App::DocumentObjectGroupPython] C_element057  label="C_element : 0.656"  # scripted group (container) (typed FeaturePython)
  n = 0.655824
FEATURE [App::DocumentObjectGroupPython] O_element058  label="O_element : 0.092"  # scripted group (container) (typed FeaturePython)
  n = 0.0921831
FEATURE [App::DocumentObjectGroupPython] Mg_element004  label="Mg_element : 0.135"  # scripted group (container) (typed FeaturePython)
  n = 0.134792
FEATURE [App::DocumentObjectGroupPython] Ca_element013  label="Ca_element : 0.003"  # scripted group (container) (typed FeaturePython)
  n = 0.002883
FEATURE [App::DocumentObjectGroupPython] G4_M3_WAX  # scripted group (container) (typed FeaturePython)
  Dunit = g/cm3
  Dvalue = 1.05
  Group = -> [H_element052,C_element057,O_element058,Mg_element004,Ca_element013]
  conduct = 2
  density = 1
  expand = 3
  formula = G4_M3_WAX
  name = G4_M3_WAX
  specific = 4
FEATURE [App::DocumentObjectGroupPython] Mg_element005  label="Mg_element : 1"  # scripted group (container) (typed FeaturePython)
  n = 1
  ref = Mg_element
FEATURE [App::DocumentObjectGroupPython] C_element058  label="C_element : 031"  # scripted group (container) (typed FeaturePython)
  n = 1
  ref = C_element
FEATURE [App::DocumentObjectGroupPython] O_element059  label="O_element : 030"  # scripted group (container) (typed FeaturePython)
  n = 3
  ref = O_element
FEATURE [App::DocumentObjectGroupPython] G4_MAGNESIUM_CARBONATE  # scripted group (container) (typed FeaturePython)
  Dunit = g/cm3
  Dvalue = 2.958
  Group = -> [Mg_element005,C_element058,O_element059]
  conduct = 2
  density = 1
  expand = 3
  formula = G4_MAGNESIUM_CARBONATE
  name = G4_MAGNESIUM_CARBONATE
  specific = 4
FEATURE [App::DocumentObjectGroupPython] Mg_element006  label="Mg_element : 002"  # scripted group (container) (typed FeaturePython)
  n = 1
  ref = Mg_element
FEATURE [App::DocumentObjectGroupPython] F_element013  label="F_element : 005"  # scripted group (container) (typed FeaturePython)
  n = 2
  ref = F_element
FEATURE [App::DocumentObjectGroupPython] G4_MAGNESIUM_FLUORIDE  # scripted group (container) (typed FeaturePython)
  Dunit = g/cm3
  Dvalue = 3
  Group = -> [Mg_element006,F_element013]
  conduct = 2
  density = 1
  expand = 3
  formula = G4_MAGNESIUM_FLUORIDE
  name = G4_MAGNESIUM_FLUORIDE
  specific = 4
FEATURE [App::DocumentObjectGroupPython] Mg_element007  label="Mg_element : 003"  # scripted group (container) (typed FeaturePython)
  n = 1
  ref = Mg_element
FEATURE [App::DocumentObjectGroupPython] O_element060  label="O_element : 031"  # scripted group (container) (typed FeaturePython)
  n = 1
  ref = O_element
FEATURE [App::DocumentObjectGroupPython] G4_MAGNESIUM_OXIDE  # scripted group (container) (typed FeaturePython)
  Dunit = g/cm3
  Dvalue = 3.58
  Group = -> [Mg_element007,O_element060]
  conduct = 2
  density = 1
  expand = 3
  formula = G4_MAGNESIUM_OXIDE
  name = G4_MAGNESIUM_OXIDE
  specific = 4
FEATURE [App::DocumentObjectGroupPython] Mg_element008  label="Mg_element : 004"  # scripted group (container) (typed FeaturePython)
  n = 1
  ref = Mg_element
FEATURE [App::DocumentObjectGroupPython] B_element006  label="B_element : 006"  # scripted group (container) (typed FeaturePython)
  n = 4
  ref = B_element
FEATURE [App::DocumentObjectGroupPython] O_element061  label="O_element : 032"  # scripted group (container) (typed FeaturePython)
  n = 7
  ref = O_element
FEATURE [App::DocumentObjectGroupPython] G4_MAGNESIUM_TETRABORATE  # scripted group (container) (typed FeaturePython)
  Dunit = g/cm3
  Dvalue = 2.53
  Group = -> [Mg_element008,B_element006,O_element061]
  conduct = 2
  density = 1
  expand = 3
  formula = G4_MAGNESIUM_TETRABORATE
  name = G4_MAGNESIUM_TETRABORATE
  specific = 4
FEATURE [App::DocumentObjectGroupPython] Hg_element001  label="Hg_element : 1"  # scripted group (container) (typed FeaturePython)
  n = 1
  ref = Hg_element
FEATURE [App::DocumentObjectGroupPython] I_element004  label="I_element : 2"  # scripted group (container) (typed FeaturePython)
  n = 2
  ref = I_element
FEATURE [App::DocumentObjectGroupPython] G4_MERCURIC_IODIDE  # scripted group (container) (typed FeaturePython)
  Dunit = g/cm3
  Dvalue = 6.36
  Group = -> [Hg_element001,I_element004]
  conduct = 2
  density = 1
  expand = 3
  formula = G4_MERCURIC_IODIDE
  name = G4_MERCURIC_IODIDE
  specific = 4
FEATURE [App::DocumentObjectGroupPython] C_element059  label="C_element : 032"  # scripted group (container) (typed FeaturePython)
  n = 1
  ref = C_element
FEATURE [App::DocumentObjectGroupPython] H_element053  label="H_element : 028"  # scripted group (container) (typed FeaturePython)
  n = 4
  ref = H_element
FEATURE [App::DocumentObjectGroupPython] G4_METHANE  # scripted group (container) (typed FeaturePython)
  Dunit = g/cm3
  Dvalue = 0.000667151
  Group = -> [C_element059,H_element053]
  conduct = 2
  density = 1
  expand = 3
  formula = G4_METHANE
  name = G4_METHANE
  specific = 4
FEATURE [App::DocumentObjectGroupPython] C_element060  label="C_element : 033"  # scripted group (container) (typed FeaturePython)
  n = 1
  ref = C_element
FEATURE [App::DocumentObjectGroupPython] H_element054  label="H_element : 029"  # scripted group (container) (typed FeaturePython)
  n = 4
  ref = H_element
FEATURE [App::DocumentObjectGroupPython] O_element062  label="O_element : 033"  # scripted group (container) (typed FeaturePython)
  n = 1
  ref = O_element
FEATURE [App::DocumentObjectGroupPython] G4_METHANOL  # scripted group (container) (typed FeaturePython)
  Dunit = g/cm3
  Dvalue = 0.7914
  Group = -> [C_element060,H_element054,O_element062]
  conduct = 2
  density = 1
  expand = 3
  formula = G4_METHANOL
  name = G4_METHANOL
  specific = 4
FEATURE [App::DocumentObjectGroupPython] H_element055  label="H_element : 0.134"  # scripted group (container) (typed FeaturePython)
  n = 0.13404
FEATURE [App::DocumentObjectGroupPython] C_element061  label="C_element : 0.778"  # scripted group (container) (typed FeaturePython)
  n = 0.77796
FEATURE [App::DocumentObjectGroupPython] O_element063  label="O_element : 0.035"  # scripted group (container) (typed FeaturePython)
  n = 0.03502
FEATURE [App::DocumentObjectGroupPython] Mg_element009  label="Mg_element : 0.039"  # scripted group (container) (typed FeaturePython)
  n = 0.038594
FEATURE [App::DocumentObjectGroupPython] Ti_element002  label="Ti_element : 0.014"  # scripted group (container) (typed FeaturePython)
  n = 0.014386
FEATURE [App::DocumentObjectGroupPython] G4_MIX_D_WAX  # scripted group (container) (typed FeaturePython)
  Dunit = g/cm3
  Dvalue = 0.99
  Group = -> [H_element055,C_element061,O_element063,Mg_element009,Ti_element002]
  conduct = 2
  density = 1
  expand = 3
  formula = G4_MIX_D_WAX
  name = G4_MIX_D_WAX
  specific = 4
FEATURE [App::DocumentObjectGroupPython] H_element056  label="H_element : 0.135"  # scripted group (container) (typed FeaturePython)
  n = 0.081192
FEATURE [App::DocumentObjectGroupPython] C_element062  label="C_element : 0.583"  # scripted group (container) (typed FeaturePython)
  n = 0.583442
FEATURE [App::DocumentObjectGroupPython] N_element024  label="N_element : 0.018"  # scripted group (container) (typed FeaturePython)
  n = 0.017798
FEATURE [App::DocumentObjectGroupPython] O_element064  label="O_element : 0.186"  # scripted group (container) (typed FeaturePython)
  n = 0.186381
FEATURE [App::DocumentObjectGroupPython] Mg_element010  label="Mg_element : 0.130"  # scripted group (container) (typed FeaturePython)
  n = 0.130287
FEATURE [App::DocumentObjectGroupPython] Cl_element015  label="Cl_element : 0.588"  # scripted group (container) (typed FeaturePython)
  n = 0.0009
FEATURE [App::DocumentObjectGroupPython] G4_MS20_TISSUE  # scripted group (container) (typed FeaturePython)
  Dunit = g/cm3
  Dvalue = 1
  Group = -> [H_element056,C_element062,N_element024,O_element064,Mg_element010,Cl_element015]
  conduct = 2
  density = 1
  expand = 3
  formula = G4_MS20_TISSUE
  name = G4_MS20_TISSUE
  specific = 4
FEATURE [App::DocumentObjectGroupPython] H_element057  label="H_element : 0.136"  # scripted group (container) (typed FeaturePython)
  n = 0.102
FEATURE [App::DocumentObjectGroupPython] C_element063  label="C_element : 0.143"  # scripted group (container) (typed FeaturePython)
  n = 0.143
FEATURE [App::DocumentObjectGroupPython] N_element025  label="N_element : 0.034"  # scripted group (container) (typed FeaturePython)
  n = 0.034
FEATURE [App::DocumentObjectGroupPython] O_element065  label="O_element : 0.710"  # scripted group (container) (typed FeaturePython)
  n = 0.71
FEATURE [App::DocumentObjectGroupPython] Na_element011  label="Na_element : 0.098"  # scripted group (container) (typed FeaturePython)
  n = 0.001
FEATURE [App::DocumentObjectGroupPython] P_element007  label="P_element : 0.002"  # scripted group (container) (typed FeaturePython)
  n = 0.002
FEATURE [App::DocumentObjectGroupPython] S_element017  label="S_element : 0.018"  # scripted group (container) (typed FeaturePython)
  n = 0.003
FEATURE [App::DocumentObjectGroupPython] Cl_element016  label="Cl_element : 0.589"  # scripted group (container) (typed FeaturePython)
  n = 0.001
FEATURE [App::DocumentObjectGroupPython] K_element006  label="K_element : 0.004"  # scripted group (container) (typed FeaturePython)
  n = 0.004
FEATURE [App::DocumentObjectGroupPython] G4_MUSCLE_SKELETAL_ICRP  # scripted group (container) (typed FeaturePython)
  Dunit = g/cm3
  Dvalue = 1.05
  Group = -> [H_element057,C_element063,N_element025,O_element065,Na_element011,P_element007,S_element017,Cl_element016,K_element006]
  conduct = 2
  density = 1
  expand = 3
  formula = G4_MUSCLE_SKELETAL_ICRP
  name = G4_MUSCLE_SKELETAL_ICRP
  specific = 4
FEATURE [App::DocumentObjectGroupPython] H_element058  label="H_element : 0.137"  # scripted group (container) (typed FeaturePython)
  n = 0.102102
FEATURE [App::DocumentObjectGroupPython] C_element064  label="C_element : 0.123"  # scripted group (container) (typed FeaturePython)
  n = 0.123123
FEATURE [App::DocumentObjectGroupPython] N_element026  label="N_element : 0.756"  # scripted group (container) (typed FeaturePython)
  n = 0.035035
FEATURE [App::DocumentObjectGroupPython] O_element066  label="O_element : 0.730"  # scripted group (container) (typed FeaturePython)
  n = 0.72973
FEATURE [App::DocumentObjectGroupPython] Na_element012  label="Na_element : 0.099"  # scripted group (container) (typed FeaturePython)
  n = 0.001001
FEATURE [App::DocumentObjectGroupPython] P_element008  label="P_element : 0.106"  # scripted group (container) (typed FeaturePython)
  n = 0.002002
FEATURE [App::DocumentObjectGroupPython] S_element018  label="S_element : 0.019"  # scripted group (container) (typed FeaturePython)
  n = 0.004004
FEATURE [App::DocumentObjectGroupPython] K_element007  label="K_element : 0.016"  # scripted group (container) (typed FeaturePython)
  n = 0.003003
FEATURE [App::DocumentObjectGroupPython] G4_MUSCLE_STRIATED_ICRU  # scripted group (container) (typed FeaturePython)
  Dunit = g/cm3
  Dvalue = 1.04
  Group = -> [H_element058,C_element064,N_element026,O_element066,Na_element012,P_element008,S_element018,K_element007]
  conduct = 2
  density = 1
  expand = 3
  formula = G4_MUSCLE_STRIATED_ICRU
  name = G4_MUSCLE_STRIATED_ICRU
  specific = 4
FEATURE [App::DocumentObjectGroupPython] H_element059  label="H_element : 0.098"  # scripted group (container) (typed FeaturePython)
  n = 0.0982341
FEATURE [App::DocumentObjectGroupPython] C_element065  label="C_element : 0.156"  # scripted group (container) (typed FeaturePython)
  n = 0.156214
FEATURE [App::DocumentObjectGroupPython] N_element027  label="N_element : 0.757"  # scripted group (container) (typed FeaturePython)
  n = 0.035451
FEATURE [App::DocumentObjectGroupPython] O_element067  label="O_element : 0.880"  # scripted group (container) (typed FeaturePython)
  n = 0.710101
FEATURE [App::DocumentObjectGroupPython] G4_MUSCLE_WITH_SUCROSE  # scripted group (container) (typed FeaturePython)
  Dunit = g/cm3
  Dvalue = 1.11
  Group = -> [H_element059,C_element065,N_element027,O_element067]
  conduct = 2
  density = 1
  expand = 3
  formula = G4_MUSCLE_WITH_SUCROSE
  name = G4_MUSCLE_WITH_SUCROSE
  specific = 4
FEATURE [App::DocumentObjectGroupPython] H_element060  label="H_element : 0.138"  # scripted group (container) (typed FeaturePython)
  n = 0.101969
FEATURE [App::DocumentObjectGroupPython] C_element066  label="C_element : 0.120"  # scripted group (container) (typed FeaturePython)
  n = 0.120058
FEATURE [App::DocumentObjectGroupPython] N_element028  label="N_element : 0.758"  # scripted group (container) (typed FeaturePython)
  n = 0.035451
FEATURE [App::DocumentObjectGroupPython] O_element068  label="O_element : 0.743"  # scripted group (container) (typed FeaturePython)
  n = 0.742522
FEATURE [App::DocumentObjectGroupPython] G4_MUSCLE_WITHOUT_SUCROSE  # scripted group (container) (typed FeaturePython)
  Dunit = g/cm3
  Dvalue = 1.07
  Group = -> [H_element060,C_element066,N_element028,O_element068]
  conduct = 2
  density = 1
  expand = 3
  formula = G4_MUSCLE_WITHOUT_SUCROSE
  name = G4_MUSCLE_WITHOUT_SUCROSE
  specific = 4
FEATURE [App::DocumentObjectGroupPython] C_element067  label="C_element : 10"  # scripted group (container) (typed FeaturePython)
  n = 10
  ref = C_element
FEATURE [App::DocumentObjectGroupPython] H_element061  label="H_element : 030"  # scripted group (container) (typed FeaturePython)
  n = 8
  ref = H_element
FEATURE [App::DocumentObjectGroupPython] G4_NAPHTHALENE  # scripted group (container) (typed FeaturePython)
  Dunit = g/cm3
  Dvalue = 1.145
  Group = -> [C_element067,H_element061]
  conduct = 2
  density = 1
  expand = 3
  formula = G4_NAPHTHALENE
  name = G4_NAPHTHALENE
  specific = 4
FEATURE [App::DocumentObjectGroupPython] C_element068  label="C_element : 034"  # scripted group (container) (typed FeaturePython)
  n = 6
  ref = C_element
FEATURE [App::DocumentObjectGroupPython] H_element062  label="H_element : 031"  # scripted group (container) (typed FeaturePython)
  n = 5
  ref = H_element
FEATURE [App::DocumentObjectGroupPython] N_element029  label="N_element : 012"  # scripted group (container) (typed FeaturePython)
  n = 1
  ref = N_element
FEATURE [App::DocumentObjectGroupPython] O_element069  label="O_element : 034"  # scripted group (container) (typed FeaturePython)
  n = 2
  ref = O_element
FEATURE [App::DocumentObjectGroupPython] G4_NITROBENZENE  # scripted group (container) (typed FeaturePython)
  Dunit = g/cm3
  Dvalue = 1.19867
  Group = -> [C_element068,H_element062,N_element029,O_element069]
  conduct = 2
  density = 1
  expand = 3
  formula = G4_NITROBENZENE
  name = G4_NITROBENZENE
  specific = 4
FEATURE [App::DocumentObjectGroupPython] N_element030  label="N_element : 013"  # scripted group (container) (typed FeaturePython)
  n = 2
  ref = N_element
FEATURE [App::DocumentObjectGroupPython] O_element070  label="O_element : 035"  # scripted group (container) (typed FeaturePython)
  n = 1
  ref = O_element
FEATURE [App::DocumentObjectGroupPython] G4_NITROUS_OXIDE  # scripted group (container) (typed FeaturePython)
  Dunit = g/cm3
  Dvalue = 0.00183094
  Group = -> [N_element030,O_element070]
  conduct = 2
  density = 1
  expand = 3
  formula = G4_NITROUS_OXIDE
  name = G4_NITROUS_OXIDE
  specific = 4
FEATURE [App::DocumentObjectGroupPython] H_element063  label="H_element : 0.104"  # scripted group (container) (typed FeaturePython)
  n = 0.103509
FEATURE [App::DocumentObjectGroupPython] C_element069  label="C_element : 0.648"  # scripted group (container) (typed FeaturePython)
  n = 0.648416
FEATURE [App::DocumentObjectGroupPython] N_element031  label="N_element : 0.100"  # scripted group (container) (typed FeaturePython)
  n = 0.0995361
FEATURE [App::DocumentObjectGroupPython] O_element071  label="O_element : 0.149"  # scripted group (container) (typed FeaturePython)
  n = 0.148539
FEATURE [App::DocumentObjectGroupPython] G4_NYLON_8062  label="G4_NYLON-8062"  # scripted group (container) (typed FeaturePython)
  Dunit = g/cm3
  Dvalue = 1.08
  Group = -> [H_element063,C_element069,N_element031,O_element071]
  conduct = 2
  density = 1
  expand = 3
  formula = G4_NYLON-8062
  name = G4_NYLON-8062
  specific = 4
FEATURE [App::DocumentObjectGroupPython] C_element070  label="C_element : 035"  # scripted group (container) (typed FeaturePython)
  n = 6
  ref = C_element
FEATURE [App::DocumentObjectGroupPython] H_element064  label="H_element : 11"  # scripted group (container) (typed FeaturePython)
  n = 11
  ref = H_element
FEATURE [App::DocumentObjectGroupPython] N_element032  label="N_element : 014"  # scripted group (container) (typed FeaturePython)
  n = 1
  ref = N_element
FEATURE [App::DocumentObjectGroupPython] O_element072  label="O_element : 036"  # scripted group (container) (typed FeaturePython)
  n = 1
  ref = O_element
FEATURE [App::DocumentObjectGroupPython] G4_NYLON_6_6  label="G4_NYLON-6-6"  # scripted group (container) (typed FeaturePython)
  Dunit = g/cm3
  Dvalue = 1.14
  Group = -> [C_element070,H_element064,N_element032,O_element072]
  conduct = 2
  density = 1
  expand = 3
  formula = G4_NYLON-6-6
  name = G4_NYLON-6-6
  specific = 4
FEATURE [App::DocumentObjectGroupPython] H_element065  label="H_element : 0.139"  # scripted group (container) (typed FeaturePython)
  n = 0.107062
FEATURE [App::DocumentObjectGroupPython] C_element071  label="C_element : 0.680"  # scripted group (container) (typed FeaturePython)
  n = 0.680449
FEATURE [App::DocumentObjectGroupPython] N_element033  label="N_element : 0.099"  # scripted group (container) (typed FeaturePython)
  n = 0.099189
FEATURE [App::DocumentObjectGroupPython] O_element073  label="O_element : 0.113"  # scripted group (container) (typed FeaturePython)
  n = 0.1133
FEATURE [App::DocumentObjectGroupPython] G4_NYLON_6_10  label="G4_NYLON-6-10"  # scripted group (container) (typed FeaturePython)
  Dunit = g/cm3
  Dvalue = 1.14
  Group = -> [H_element065,C_element071,N_element033,O_element073]
  conduct = 2
  density = 1
  expand = 3
  formula = G4_NYLON-6-10
  name = G4_NYLON-6-10
  specific = 4
FEATURE [App::DocumentObjectGroupPython] H_element066  label="H_element : 0.140"  # scripted group (container) (typed FeaturePython)
  n = 0.115476
FEATURE [App::DocumentObjectGroupPython] C_element072  label="C_element : 0.721"  # scripted group (container) (typed FeaturePython)
  n = 0.720818
FEATURE [App::DocumentObjectGroupPython] N_element034  label="N_element : 0.076"  # scripted group (container) (typed FeaturePython)
  n = 0.0764169
FEATURE [App::DocumentObjectGroupPython] O_element074  label="O_element : 0.087"  # scripted group (container) (typed FeaturePython)
  n = 0.0872889
FEATURE [App::DocumentObjectGroupPython] G4_NYLON_11_RILSAN  label="G4_NYLON-11_RILSAN"  # scripted group (container) (typed FeaturePython)
  Dunit = g/cm3
  Dvalue = 1.425
  Group = -> [H_element066,C_element072,N_element034,O_element074]
  conduct = 2
  density = 1
  expand = 3
  formula = G4_NYLON-11_RILSAN
  name = G4_NYLON-11_RILSAN
  specific = 4
FEATURE [App::DocumentObjectGroupPython] C_element073  label="C_element : 8"  # scripted group (container) (typed FeaturePython)
  n = 8
  ref = C_element
FEATURE [App::DocumentObjectGroupPython] H_element067  label="H_element : 18"  # scripted group (container) (typed FeaturePython)
  n = 18
  ref = H_element
FEATURE [App::DocumentObjectGroupPython] G4_OCTANE  # scripted group (container) (typed FeaturePython)
  Dunit = g/cm3
  Dvalue = 0.7026
  Group = -> [C_element073,H_element067]
  conduct = 2
  density = 1
  expand = 3
  formula = G4_OCTANE
  name = G4_OCTANE
  specific = 4
FEATURE [App::DocumentObjectGroupPython] C_element074  label="C_element : 25"  # scripted group (container) (typed FeaturePython)
  n = 25
  ref = C_element
FEATURE [App::DocumentObjectGroupPython] H_element068  label="H_element : 52"  # scripted group (container) (typed FeaturePython)
  n = 52
  ref = H_element
FEATURE [App::DocumentObjectGroupPython] G4_PARAFFIN  # scripted group (container) (typed FeaturePython)
  Dunit = g/cm3
  Dvalue = 0.93
  Group = -> [C_element074,H_element068]
  conduct = 2
  density = 1
  expand = 3
  formula = G4_PARAFFIN
  name = G4_PARAFFIN
  specific = 4
FEATURE [App::DocumentObjectGroupPython] C_element075  label="C_element : 036"  # scripted group (container) (typed FeaturePython)
  n = 5
  ref = C_element
FEATURE [App::DocumentObjectGroupPython] H_element069  label="H_element : 032"  # scripted group (container) (typed FeaturePython)
  n = 12
  ref = H_element
FEATURE [App::DocumentObjectGroupPython] G4_N_PENTANE  label="G4_N-PENTANE"  # scripted group (container) (typed FeaturePython)
  Dunit = g/cm3
  Dvalue = 0.6262
  Group = -> [C_element075,H_element069]
  conduct = 2
  density = 1
  expand = 3
  formula = G4_N-PENTANE
  name = G4_N-PENTANE
  specific = 4
FEATURE [App::DocumentObjectGroupPython] H_element070  label="H_element : 0.014"  # scripted group (container) (typed FeaturePython)
  n = 0.0141
FEATURE [App::DocumentObjectGroupPython] C_element076  label="C_element : 0.072"  # scripted group (container) (typed FeaturePython)
  n = 0.072261
FEATURE [App::DocumentObjectGroupPython] N_element035  label="N_element : 0.019"  # scripted group (container) (typed FeaturePython)
  n = 0.01932
FEATURE [App::DocumentObjectGroupPython] O_element075  label="O_element : 0.066"  # scripted group (container) (typed FeaturePython)
  n = 0.066101
FEATURE [App::DocumentObjectGroupPython] S_element019  label="S_element : 0.020"  # scripted group (container) (typed FeaturePython)
  n = 0.00189
FEATURE [App::DocumentObjectGroupPython] Br_element004  label="Br_element : 0.349"  # scripted group (container) (typed FeaturePython)
  n = 0.349103
FEATURE [App::DocumentObjectGroupPython] Ag_element001  label="Ag_element : 0.474"  # scripted group (container) (typed FeaturePython)
  n = 0.474105
FEATURE [App::DocumentObjectGroupPython] I_element005  label="I_element : 0.003"  # scripted group (container) (typed FeaturePython)
  n = 0.00312
FEATURE [App::DocumentObjectGroupPython] G4_PHOTO_EMULSION  # scripted group (container) (typed FeaturePython)
  Dunit = g/cm3
  Dvalue = 3.815
  Group = -> [H_element070,C_element076,N_element035,O_element075,S_element019,Br_element004,Ag_element001,I_element005]
  conduct = 2
  density = 1
  expand = 3
  formula = G4_PHOTO_EMULSION
  name = G4_PHOTO_EMULSION
  specific = 4
FEATURE [App::DocumentObjectGroupPython] C_element077  label="C_element : 9"  # scripted group (container) (typed FeaturePython)
  n = 9
  ref = C_element
FEATURE [App::DocumentObjectGroupPython] H_element071  label="H_element : 033"  # scripted group (container) (typed FeaturePython)
  n = 10
  ref = H_element
FEATURE [App::DocumentObjectGroupPython] G4_PLASTIC_SC_VINYLTOLUENE  # scripted group (container) (typed FeaturePython)
  Dunit = g/cm3
  Dvalue = 1.032
  Group = -> [C_element077,H_element071]
  conduct = 2
  density = 1
  expand = 3
  formula = G4_PLASTIC_SC_VINYLTOLUENE
  name = G4_PLASTIC_SC_VINYLTOLUENE
  specific = 4
FEATURE [App::DocumentObjectGroupPython] Pu_element001  label="Pu_element : 1"  # scripted group (container) (typed FeaturePython)
  n = 1
  ref = Pu_element
FEATURE [App::DocumentObjectGroupPython] O_element076  label="O_element : 037"  # scripted group (container) (typed FeaturePython)
  n = 2
  ref = O_element
FEATURE [App::DocumentObjectGroupPython] G4_PLUTONIUM_DIOXIDE  # scripted group (container) (typed FeaturePython)
  Dunit = g/cm3
  Dvalue = 11.46
  Group = -> [Pu_element001,O_element076]
  conduct = 2
  density = 1
  expand = 3
  formula = G4_PLUTONIUM_DIOXIDE
  name = G4_PLUTONIUM_DIOXIDE
  specific = 4
FEATURE [App::DocumentObjectGroupPython] C_element078  label="C_element : 037"  # scripted group (container) (typed FeaturePython)
  n = 3
  ref = C_element
FEATURE [App::DocumentObjectGroupPython] H_element072  label="H_element : 034"  # scripted group (container) (typed FeaturePython)
  n = 3
  ref = H_element
FEATURE [App::DocumentObjectGroupPython] N_element036  label="N_element : 015"  # scripted group (container) (typed FeaturePython)
  n = 1
  ref = N_element
FEATURE [App::DocumentObjectGroupPython] G4_POLYACRYLONITRILE  # scripted group (container) (typed FeaturePython)
  Dunit = g/cm3
  Dvalue = 1.17
  Group = -> [C_element078,H_element072,N_element036]
  conduct = 2
  density = 1
  expand = 3
  formula = G4_POLYACRYLONITRILE
  name = G4_POLYACRYLONITRILE
  specific = 4
FEATURE [App::DocumentObjectGroupPython] C_element079  label="C_element : 16"  # scripted group (container) (typed FeaturePython)
  n = 16
  ref = C_element
FEATURE [App::DocumentObjectGroupPython] H_element073  label="H_element : 035"  # scripted group (container) (typed FeaturePython)
  n = 14
  ref = H_element
FEATURE [App::DocumentObjectGroupPython] O_element077  label="O_element : 038"  # scripted group (container) (typed FeaturePython)
  n = 3
  ref = O_element
FEATURE [App::DocumentObjectGroupPython] G4_POLYCARBONATE  # scripted group (container) (typed FeaturePython)
  Dunit = g/cm3
  Dvalue = 1.2
  Group = -> [C_element079,H_element073,O_element077]
  conduct = 2
  density = 1
  expand = 3
  formula = G4_POLYCARBONATE
  name = G4_POLYCARBONATE
  specific = 4
FEATURE [App::DocumentObjectGroupPython] C_element080  label="C_element : 038"  # scripted group (container) (typed FeaturePython)
  n = 8
  ref = C_element
FEATURE [App::DocumentObjectGroupPython] H_element074  label="H_element : 036"  # scripted group (container) (typed FeaturePython)
  n = 7
  ref = H_element
FEATURE [App::DocumentObjectGroupPython] Cl_element017  label="Cl_element : 007"  # scripted group (container) (typed FeaturePython)
  n = 1
  ref = Cl_element
FEATURE [App::DocumentObjectGroupPython] G4_POLYCHLOROSTYRENE  # scripted group (container) (typed FeaturePython)
  Dunit = g/cm3
  Dvalue = 1.3
  Group = -> [C_element080,H_element074,Cl_element017]
  conduct = 2
  density = 1
  expand = 3
  formula = G4_POLYCHLOROSTYRENE
  name = G4_POLYCHLOROSTYRENE
  specific = 4
FEATURE [App::DocumentObjectGroupPython] C_element081  label="C_element : 039"  # scripted group (container) (typed FeaturePython)
  n = 1
  ref = C_element
FEATURE [App::DocumentObjectGroupPython] H_element075  label="H_element : 037"  # scripted group (container) (typed FeaturePython)
  n = 2
  ref = H_element
FEATURE [App::DocumentObjectGroupPython] G4_POLYETHYLENE  # scripted group (container) (typed FeaturePython)
  Dunit = g/cm3
  Dvalue = 0.94
  Group = -> [C_element081,H_element075]
  conduct = 2
  density = 1
  expand = 3
  formula = G4_POLYETHYLENE
  name = G4_POLYETHYLENE
  specific = 4
FEATURE [App::DocumentObjectGroupPython] C_element082  label="C_element : 040"  # scripted group (container) (typed FeaturePython)
  n = 10
  ref = C_element
FEATURE [App::DocumentObjectGroupPython] H_element076  label="H_element : 038"  # scripted group (container) (typed FeaturePython)
  n = 8
  ref = H_element
FEATURE [App::DocumentObjectGroupPython] O_element078  label="O_element : 039"  # scripted group (container) (typed FeaturePython)
  n = 4
  ref = O_element
FEATURE [App::DocumentObjectGroupPython] G4_MYLAR  # scripted group (container) (typed FeaturePython)
  Dunit = g/cm3
  Dvalue = 1.4
  Group = -> [C_element082,H_element076,O_element078]
  conduct = 2
  density = 1
  expand = 3
  formula = G4_MYLAR
  name = G4_MYLAR
  specific = 4
FEATURE [App::DocumentObjectGroupPython] C_element083  label="C_element : 041"  # scripted group (container) (typed FeaturePython)
  n = 5
  ref = C_element
FEATURE [App::DocumentObjectGroupPython] H_element077  label="H_element : 039"  # scripted group (container) (typed FeaturePython)
  n = 8
  ref = H_element
FEATURE [App::DocumentObjectGroupPython] O_element079  label="O_element : 040"  # scripted group (container) (typed FeaturePython)
  n = 2
  ref = O_element
FEATURE [App::DocumentObjectGroupPython] G4_PLEXIGLASS  # scripted group (container) (typed FeaturePython)
  Dunit = g/cm3
  Dvalue = 1.19
  Group = -> [C_element083,H_element077,O_element079]
  conduct = 2
  density = 1
  expand = 3
  formula = G4_PLEXIGLASS
  name = G4_PLEXIGLASS
  specific = 4
FEATURE [App::DocumentObjectGroupPython] C_element084  label="C_element : 042"  # scripted group (container) (typed FeaturePython)
  n = 1
  ref = C_element
FEATURE [App::DocumentObjectGroupPython] H_element078  label="H_element : 040"  # scripted group (container) (typed FeaturePython)
  n = 2
  ref = H_element
FEATURE [App::DocumentObjectGroupPython] O_element080  label="O_element : 041"  # scripted group (container) (typed FeaturePython)
  n = 1
  ref = O_element
FEATURE [App::DocumentObjectGroupPython] G4_POLYOXYMETHYLENE  # scripted group (container) (typed FeaturePython)
  Dunit = g/cm3
  Dvalue = 1.425
  Group = -> [C_element084,H_element078,O_element080]
  conduct = 2
  density = 1
  expand = 3
  formula = G4_POLYOXYMETHYLENE
  name = G4_POLYOXYMETHYLENE
  specific = 4
FEATURE [App::DocumentObjectGroupPython] C_element085  label="C_element : 043"  # scripted group (container) (typed FeaturePython)
  n = 2
  ref = C_element
FEATURE [App::DocumentObjectGroupPython] H_element079  label="H_element : 041"  # scripted group (container) (typed FeaturePython)
  n = 4
  ref = H_element
FEATURE [App::DocumentObjectGroupPython] G4_POLYPROPYLENE  # scripted group (container) (typed FeaturePython)
  Dunit = g/cm3
  Dvalue = 0.9
  Group = -> [C_element085,H_element079]
  conduct = 2
  density = 1
  expand = 3
  formula = G4_POLYPROPYLENE
  name = G4_POLYPROPYLENE
  specific = 4
FEATURE [App::DocumentObjectGroupPython] C_element086  label="C_element : 044"  # scripted group (container) (typed FeaturePython)
  n = 8
  ref = C_element
FEATURE [App::DocumentObjectGroupPython] H_element080  label="H_element : 042"  # scripted group (container) (typed FeaturePython)
  n = 8
  ref = H_element
FEATURE [App::DocumentObjectGroupPython] G4_POLYSTYRENE  # scripted group (container) (typed FeaturePython)
  Dunit = g/cm3
  Dvalue = 1.06
  Group = -> [C_element086,H_element080]
  conduct = 2
  density = 1
  expand = 3
  formula = G4_POLYSTYRENE
  name = G4_POLYSTYRENE
  specific = 4
FEATURE [App::DocumentObjectGroupPython] C_element087  label="C_element : 045"  # scripted group (container) (typed FeaturePython)
  n = 2
  ref = C_element
FEATURE [App::DocumentObjectGroupPython] F_element014  label="F_element : 4"  # scripted group (container) (typed FeaturePython)
  n = 4
  ref = F_element
FEATURE [App::DocumentObjectGroupPython] G4_TEFLON  # scripted group (container) (typed FeaturePython)
  Dunit = g/cm3
  Dvalue = 2.2
  Group = -> [C_element087,F_element014]
  conduct = 2
  density = 1
  expand = 3
  formula = G4_TEFLON
  name = G4_TEFLON
  specific = 4
FEATURE [App::DocumentObjectGroupPython] C_element088  label="C_element : 046"  # scripted group (container) (typed FeaturePython)
  n = 2
  ref = C_element
FEATURE [App::DocumentObjectGroupPython] F_element015  label="F_element : 006"  # scripted group (container) (typed FeaturePython)
  n = 3
  ref = F_element
FEATURE [App::DocumentObjectGroupPython] Cl_element018  label="Cl_element : 008"  # scripted group (container) (typed FeaturePython)
  n = 1
  ref = Cl_element
FEATURE [App::DocumentObjectGroupPython] G4_POLYTRIFLUOROCHLOROETHYLENE  # scripted group (container) (typed FeaturePython)
  Dunit = g/cm3
  Dvalue = 2.1
  Group = -> [C_element088,F_element015,Cl_element018]
  conduct = 2
  density = 1
  expand = 3
  formula = G4_POLYTRIFLUOROCHLOROETHYLENE
  name = G4_POLYTRIFLUOROCHLOROETHYLENE
  specific = 4
FEATURE [App::DocumentObjectGroupPython] C_element089  label="C_element : 047"  # scripted group (container) (typed FeaturePython)
  n = 4
  ref = C_element
FEATURE [App::DocumentObjectGroupPython] H_element081  label="H_element : 043"  # scripted group (container) (typed FeaturePython)
  n = 6
  ref = H_element
FEATURE [App::DocumentObjectGroupPython] O_element081  label="O_element : 042"  # scripted group (container) (typed FeaturePython)
  n = 2
  ref = O_element
FEATURE [App::DocumentObjectGroupPython] G4_POLYVINYL_ACETATE  # scripted group (container) (typed FeaturePython)
  Dunit = g/cm3
  Dvalue = 1.19
  Group = -> [C_element089,H_element081,O_element081]
  conduct = 2
  density = 1
  expand = 3
  formula = G4_POLYVINYL_ACETATE
  name = G4_POLYVINYL_ACETATE
  specific = 4
FEATURE [App::DocumentObjectGroupPython] C_element090  label="C_element : 048"  # scripted group (container) (typed FeaturePython)
  n = 2
  ref = C_element
FEATURE [App::DocumentObjectGroupPython] H_element082  label="H_element : 044"  # scripted group (container) (typed FeaturePython)
  n = 4
  ref = H_element
FEATURE [App::DocumentObjectGroupPython] O_element082  label="O_element : 043"  # scripted group (container) (typed FeaturePython)
  n = 1
  ref = O_element
FEATURE [App::DocumentObjectGroupPython] G4_POLYVINYL_ALCOHOL  # scripted group (container) (typed FeaturePython)
  Dunit = g/cm3
  Dvalue = 1.3
  Group = -> [C_element090,H_element082,O_element082]
  conduct = 2
  density = 1
  expand = 3
  formula = G4_POLYVINYL_ALCOHOL
  name = G4_POLYVINYL_ALCOHOL
  specific = 4
FEATURE [App::DocumentObjectGroupPython] C_element091  label="C_element : 049"  # scripted group (container) (typed FeaturePython)
  n = 8
  ref = C_element
FEATURE [App::DocumentObjectGroupPython] H_element083  label="H_element : 045"  # scripted group (container) (typed FeaturePython)
  n = 14
  ref = H_element
FEATURE [App::DocumentObjectGroupPython] O_element083  label="O_element : 044"  # scripted group (container) (typed FeaturePython)
  n = 2
  ref = O_element
FEATURE [App::DocumentObjectGroupPython] G4_POLYVINYL_BUTYRAL  # scripted group (container) (typed FeaturePython)
  Dunit = g/cm3
  Dvalue = 1.12
  Group = -> [C_element091,H_element083,O_element083]
  conduct = 2
  density = 1
  expand = 3
  formula = G4_POLYVINYL_BUTYRAL
  name = G4_POLYVINYL_BUTYRAL
  specific = 4
FEATURE [App::DocumentObjectGroupPython] C_element092  label="C_element : 050"  # scripted group (container) (typed FeaturePython)
  n = 2
  ref = C_element
FEATURE [App::DocumentObjectGroupPython] H_element084  label="H_element : 046"  # scripted group (container) (typed FeaturePython)
  n = 3
  ref = H_element
FEATURE [App::DocumentObjectGroupPython] Cl_element019  label="Cl_element : 009"  # scripted group (container) (typed FeaturePython)
  n = 1
  ref = Cl_element
FEATURE [App::DocumentObjectGroupPython] G4_POLYVINYL_CHLORIDE  # scripted group (container) (typed FeaturePython)
  Dunit = g/cm3
  Dvalue = 1.3
  Group = -> [C_element092,H_element084,Cl_element019]
  conduct = 2
  density = 1
  expand = 3
  formula = G4_POLYVINYL_CHLORIDE
  name = G4_POLYVINYL_CHLORIDE
  specific = 4
FEATURE [App::DocumentObjectGroupPython] C_element093  label="C_element : 051"  # scripted group (container) (typed FeaturePython)
  n = 2
  ref = C_element
FEATURE [App::DocumentObjectGroupPython] H_element085  label="H_element : 047"  # scripted group (container) (typed FeaturePython)
  n = 2
  ref = H_element
FEATURE [App::DocumentObjectGroupPython] Cl_element020  label="Cl_element : 010"  # scripted group (container) (typed FeaturePython)
  n = 2
  ref = Cl_element
FEATURE [App::DocumentObjectGroupPython] G4_POLYVINYLIDENE_CHLORIDE  # scripted group (container) (typed FeaturePython)
  Dunit = g/cm3
  Dvalue = 1.7
  Group = -> [C_element093,H_element085,Cl_element020]
  conduct = 2
  density = 1
  expand = 3
  formula = G4_POLYVINYLIDENE_CHLORIDE
  name = G4_POLYVINYLIDENE_CHLORIDE
  specific = 4
FEATURE [App::DocumentObjectGroupPython] C_element094  label="C_element : 052"  # scripted group (container) (typed FeaturePython)
  n = 2
  ref = C_element
FEATURE [App::DocumentObjectGroupPython] H_element086  label="H_element : 048"  # scripted group (container) (typed FeaturePython)
  n = 2
  ref = H_element
FEATURE [App::DocumentObjectGroupPython] F_element016  label="F_element : 007"  # scripted group (container) (typed FeaturePython)
  n = 2
  ref = F_element
FEATURE [App::DocumentObjectGroupPython] G4_POLYVINYLIDENE_FLUORIDE  # scripted group (container) (typed FeaturePython)
  Dunit = g/cm3
  Dvalue = 1.76
  Group = -> [C_element094,H_element086,F_element016]
  conduct = 2
  density = 1
  expand = 3
  formula = G4_POLYVINYLIDENE_FLUORIDE
  name = G4_POLYVINYLIDENE_FLUORIDE
  specific = 4
FEATURE [App::DocumentObjectGroupPython] C_element095  label="C_element : 053"  # scripted group (container) (typed FeaturePython)
  n = 6
  ref = C_element
FEATURE [App::DocumentObjectGroupPython] H_element087  label="H_element : 9"  # scripted group (container) (typed FeaturePython)
  n = 9
  ref = H_element
FEATURE [App::DocumentObjectGroupPython] N_element037  label="N_element : 016"  # scripted group (container) (typed FeaturePython)
  n = 1
  ref = N_element
FEATURE [App::DocumentObjectGroupPython] O_element084  label="O_element : 045"  # scripted group (container) (typed FeaturePython)
  n = 1
  ref = O_element
FEATURE [App::DocumentObjectGroupPython] G4_POLYVINYL_PYRROLIDONE  # scripted group (container) (typed FeaturePython)
  Dunit = g/cm3
  Dvalue = 1.25
  Group = -> [C_element095,H_element087,N_element037,O_element084]
  conduct = 2
  density = 1
  expand = 3
  formula = G4_POLYVINYL_PYRROLIDONE
  name = G4_POLYVINYL_PYRROLIDONE
  specific = 4
FEATURE [App::DocumentObjectGroupPython] K_element008  label="K_element : 1"  # scripted group (container) (typed FeaturePython)
  n = 1
  ref = K_element
FEATURE [App::DocumentObjectGroupPython] I_element006  label="I_element : 003"  # scripted group (container) (typed FeaturePython)
  n = 1
  ref = I_element
FEATURE [App::DocumentObjectGroupPython] G4_POTASSIUM_IODIDE  # scripted group (container) (typed FeaturePython)
  Dunit = g/cm3
  Dvalue = 3.13
  Group = -> [K_element008,I_element006]
  conduct = 2
  density = 1
  expand = 3
  formula = G4_POTASSIUM_IODIDE
  name = G4_POTASSIUM_IODIDE
  specific = 4
FEATURE [App::DocumentObjectGroupPython] K_element009  label="K_element : 2"  # scripted group (container) (typed FeaturePython)
  n = 2
  ref = K_element
FEATURE [App::DocumentObjectGroupPython] O_element085  label="O_element : 046"  # scripted group (container) (typed FeaturePython)
  n = 1
  ref = O_element
FEATURE [App::DocumentObjectGroupPython] G4_POTASSIUM_OXIDE  # scripted group (container) (typed FeaturePython)
  Dunit = g/cm3
  Dvalue = 2.32
  Group = -> [K_element009,O_element085]
  conduct = 2
  density = 1
  expand = 3
  formula = G4_POTASSIUM_OXIDE
  name = G4_POTASSIUM_OXIDE
  specific = 4
FEATURE [App::DocumentObjectGroupPython] C_element096  label="C_element : 054"  # scripted group (container) (typed FeaturePython)
  n = 3
  ref = C_element
FEATURE [App::DocumentObjectGroupPython] H_element088  label="H_element : 049"  # scripted group (container) (typed FeaturePython)
  n = 8
  ref = H_element
FEATURE [App::DocumentObjectGroupPython] G4_PROPANE  # scripted group (container) (typed FeaturePython)
  Dunit = g/cm3
  Dvalue = 0.00187939
  Group = -> [C_element096,H_element088]
  conduct = 2
  density = 1
  expand = 3
  formula = G4_PROPANE
  name = G4_PROPANE
  specific = 4
FEATURE [App::DocumentObjectGroupPython] C_element097  label="C_element : 055"  # scripted group (container) (typed FeaturePython)
  n = 3
  ref = C_element
FEATURE [App::DocumentObjectGroupPython] H_element089  label="H_element : 050"  # scripted group (container) (typed FeaturePython)
  n = 8
  ref = H_element
FEATURE [App::DocumentObjectGroupPython] G4_lPROPANE  # scripted group (container) (typed FeaturePython)
  Dunit = g/cm3
  Dvalue = 0.43
  Group = -> [C_element097,H_element089]
  conduct = 2
  density = 1
  expand = 3
  formula = G4_lPROPANE
  name = G4_lPROPANE
  specific = 4
FEATURE [App::DocumentObjectGroupPython] C_element098  label="C_element : 056"  # scripted group (container) (typed FeaturePython)
  n = 3
  ref = C_element
FEATURE [App::DocumentObjectGroupPython] H_element090  label="H_element : 051"  # scripted group (container) (typed FeaturePython)
  n = 8
  ref = H_element
FEATURE [App::DocumentObjectGroupPython] O_element086  label="O_element : 047"  # scripted group (container) (typed FeaturePython)
  n = 1
  ref = O_element
FEATURE [App::DocumentObjectGroupPython] G4_N_PROPYL_ALCOHOL  label="G4_N-PROPYL_ALCOHOL"  # scripted group (container) (typed FeaturePython)
  Dunit = g/cm3
  Dvalue = 0.8035
  Group = -> [C_element098,H_element090,O_element086]
  conduct = 2
  density = 1
  expand = 3
  formula = G4_N-PROPYL_ALCOHOL
  name = G4_N-PROPYL_ALCOHOL
  specific = 4
FEATURE [App::DocumentObjectGroupPython] C_element099  label="C_element : 057"  # scripted group (container) (typed FeaturePython)
  n = 5
  ref = C_element
FEATURE [App::DocumentObjectGroupPython] H_element091  label="H_element : 052"  # scripted group (container) (typed FeaturePython)
  n = 5
  ref = H_element
FEATURE [App::DocumentObjectGroupPython] N_element038  label="N_element : 017"  # scripted group (container) (typed FeaturePython)
  n = 1
  ref = N_element
FEATURE [App::DocumentObjectGroupPython] G4_PYRIDINE  # scripted group (container) (typed FeaturePython)
  Dunit = g/cm3
  Dvalue = 0.9819
  Group = -> [C_element099,H_element091,N_element038]
  conduct = 2
  density = 1
  expand = 3
  formula = G4_PYRIDINE
  name = G4_PYRIDINE
  specific = 4
FEATURE [App::DocumentObjectGroupPython] H_element092  label="H_element : 0.144"  # scripted group (container) (typed FeaturePython)
  n = 0.143711
FEATURE [App::DocumentObjectGroupPython] C_element100  label="C_element : 0.856"  # scripted group (container) (typed FeaturePython)
  n = 0.856289
FEATURE [App::DocumentObjectGroupPython] G4_RUBBER_BUTYL  # scripted group (container) (typed FeaturePython)
  Dunit = g/cm3
  Dvalue = 0.92
  Group = -> [H_element092,C_element100]
  conduct = 2
  density = 1
  expand = 3
  formula = G4_RUBBER_BUTYL
  name = G4_RUBBER_BUTYL
  specific = 4
FEATURE [App::DocumentObjectGroupPython] H_element093  label="H_element : 0.118"  # scripted group (container) (typed FeaturePython)
  n = 0.118371
FEATURE [App::DocumentObjectGroupPython] C_element101  label="C_element : 0.882"  # scripted group (container) (typed FeaturePython)
  n = 0.881629
FEATURE [App::DocumentObjectGroupPython] G4_RUBBER_NATURAL  # scripted group (container) (typed FeaturePython)
  Dunit = g/cm3
  Dvalue = 0.92
  Group = -> [H_element093,C_element101]
  conduct = 2
  density = 1
  expand = 3
  formula = G4_RUBBER_NATURAL
  name = G4_RUBBER_NATURAL
  specific = 4
FEATURE [App::DocumentObjectGroupPython] H_element094  label="H_element : 0.145"  # scripted group (container) (typed FeaturePython)
  n = 0.05692
FEATURE [App::DocumentObjectGroupPython] C_element102  label="C_element : 0.543"  # scripted group (container) (typed FeaturePython)
  n = 0.542646
FEATURE [App::DocumentObjectGroupPython] Cl_element021  label="Cl_element : 0.400"  # scripted group (container) (typed FeaturePython)
  n = 0.400434
FEATURE [App::DocumentObjectGroupPython] G4_RUBBER_NEOPRENE  # scripted group (container) (typed FeaturePython)
  Dunit = g/cm3
  Dvalue = 1.23
  Group = -> [H_element094,C_element102,Cl_element021]
  conduct = 2
  density = 1
  expand = 3
  formula = G4_RUBBER_NEOPRENE
  name = G4_RUBBER_NEOPRENE
  specific = 4
FEATURE [App::DocumentObjectGroupPython] Si_element006  label="Si_element : 1"  # scripted group (container) (typed FeaturePython)
  n = 1
  ref = Si_element
FEATURE [App::DocumentObjectGroupPython] O_element087  label="O_element : 048"  # scripted group (container) (typed FeaturePython)
  n = 2
  ref = O_element
FEATURE [App::DocumentObjectGroupPython] G4_SILICON_DIOXIDE  # scripted group (container) (typed FeaturePython)
  Dunit = g/cm3
  Dvalue = 2.32
  Group = -> [Si_element006,O_element087]
  conduct = 2
  density = 1
  expand = 3
  formula = G4_SILICON_DIOXIDE
  name = G4_SILICON_DIOXIDE
  specific = 4
FEATURE [App::DocumentObjectGroupPython] Ag_element002  label="Ag_element : 1"  # scripted group (container) (typed FeaturePython)
  n = 1
  ref = Ag_element
FEATURE [App::DocumentObjectGroupPython] Br_element005  label="Br_element : 003"  # scripted group (container) (typed FeaturePython)
  n = 1
  ref = Br_element
FEATURE [App::DocumentObjectGroupPython] G4_SILVER_BROMIDE  # scripted group (container) (typed FeaturePython)
  Dunit = g/cm3
  Dvalue = 6.473
  Group = -> [Ag_element002,Br_element005]
  conduct = 2
  density = 1
  expand = 3
  formula = G4_SILVER_BROMIDE
  name = G4_SILVER_BROMIDE
  specific = 4
FEATURE [App::DocumentObjectGroupPython] Ag_element003  label="Ag_element : 002"  # scripted group (container) (typed FeaturePython)
  n = 1
  ref = Ag_element
FEATURE [App::DocumentObjectGroupPython] Cl_element022  label="Cl_element : 011"  # scripted group (container) (typed FeaturePython)
  n = 1
  ref = Cl_element
FEATURE [App::DocumentObjectGroupPython] G4_SILVER_CHLORIDE  # scripted group (container) (typed FeaturePython)
  Dunit = g/cm3
  Dvalue = 5.56
  Group = -> [Ag_element003,Cl_element022]
  conduct = 2
  density = 1
  expand = 3
  formula = G4_SILVER_CHLORIDE
  name = G4_SILVER_CHLORIDE
  specific = 4
FEATURE [App::DocumentObjectGroupPython] Br_element006  label="Br_element : 0.423"  # scripted group (container) (typed FeaturePython)
  n = 0.422895
FEATURE [App::DocumentObjectGroupPython] Ag_element004  label="Ag_element : 0.574"  # scripted group (container) (typed FeaturePython)
  n = 0.573748
FEATURE [App::DocumentObjectGroupPython] I_element007  label="I_element : 0.649"  # scripted group (container) (typed FeaturePython)
  n = 0.003357
FEATURE [App::DocumentObjectGroupPython] G4_SILVER_HALIDES  # scripted group (container) (typed FeaturePython)
  Dunit = g/cm3
  Dvalue = 6.47
  Group = -> [Br_element006,Ag_element004,I_element007]
  conduct = 2
  density = 1
  expand = 3
  formula = G4_SILVER_HALIDES
  name = G4_SILVER_HALIDES
  specific = 4
FEATURE [App::DocumentObjectGroupPython] Ag_element005  label="Ag_element : 003"  # scripted group (container) (typed FeaturePython)
  n = 1
  ref = Ag_element
FEATURE [App::DocumentObjectGroupPython] I_element008  label="I_element : 004"  # scripted group (container) (typed FeaturePython)
  n = 1
  ref = I_element
FEATURE [App::DocumentObjectGroupPython] G4_SILVER_IODIDE  # scripted group (container) (typed FeaturePython)
  Dunit = g/cm3
  Dvalue = 6.01
  Group = -> [Ag_element005,I_element008]
  conduct = 2
  density = 1
  expand = 3
  formula = G4_SILVER_IODIDE
  name = G4_SILVER_IODIDE
  specific = 4
FEATURE [App::DocumentObjectGroupPython] H_element095  label="H_element : 0.100"  # scripted group (container) (typed FeaturePython)
  n = 0.1
FEATURE [App::DocumentObjectGroupPython] C_element103  label="C_element : 0.204"  # scripted group (container) (typed FeaturePython)
  n = 0.204
FEATURE [App::DocumentObjectGroupPython] N_element039  label="N_element : 0.759"  # scripted group (container) (typed FeaturePython)
  n = 0.042
FEATURE [App::DocumentObjectGroupPython] O_element088  label="O_element : 0.645"  # scripted group (container) (typed FeaturePython)
  n = 0.645
FEATURE [App::DocumentObjectGroupPython] Na_element013  label="Na_element : 0.100"  # scripted group (container) (typed FeaturePython)
  n = 0.002
FEATURE [App::DocumentObjectGroupPython] P_element009  label="P_element : 0.107"  # scripted group (container) (typed FeaturePython)
  n = 0.001
FEATURE [App::DocumentObjectGroupPython] S_element020  label="S_element : 0.021"  # scripted group (container) (typed FeaturePython)
  n = 0.002
FEATURE [App::DocumentObjectGroupPython] Cl_element023  label="Cl_element : 0.590"  # scripted group (container) (typed FeaturePython)
  n = 0.003
FEATURE [App::DocumentObjectGroupPython] K_element010  label="K_element : 0.001"  # scripted group (container) (typed FeaturePython)
  n = 0.001
FEATURE [App::DocumentObjectGroupPython] G4_SKIN_ICRP  # scripted group (container) (typed FeaturePython)
  Dunit = g/cm3
  Dvalue = 1.09
  Group = -> [H_element095,C_element103,N_element039,O_element088,Na_element013,P_element009,S_element020,Cl_element023,K_element010]
  conduct = 2
  density = 1
  expand = 3
  formula = G4_SKIN_ICRP
  name = G4_SKIN_ICRP
  specific = 4
FEATURE [App::DocumentObjectGroupPython] Na_element014  label="Na_element : 2"  # scripted group (container) (typed FeaturePython)
  n = 2
  ref = Na_element
FEATURE [App::DocumentObjectGroupPython] C_element104  label="C_element : 058"  # scripted group (container) (typed FeaturePython)
  n = 1
  ref = C_element
FEATURE [App::DocumentObjectGroupPython] O_element089  label="O_element : 049"  # scripted group (container) (typed FeaturePython)
  n = 3
  ref = O_element
FEATURE [App::DocumentObjectGroupPython] G4_SODIUM_CARBONATE  # scripted group (container) (typed FeaturePython)
  Dunit = g/cm3
  Dvalue = 2.532
  Group = -> [Na_element014,C_element104,O_element089]
  conduct = 2
  density = 1
  expand = 3
  formula = G4_SODIUM_CARBONATE
  name = G4_SODIUM_CARBONATE
  specific = 4
FEATURE [App::DocumentObjectGroupPython] Na_element015  label="Na_element : 1"  # scripted group (container) (typed FeaturePython)
  n = 1
  ref = Na_element
FEATURE [App::DocumentObjectGroupPython] I_element009  label="I_element : 005"  # scripted group (container) (typed FeaturePython)
  n = 1
  ref = I_element
FEATURE [App::DocumentObjectGroupPython] G4_SODIUM_IODIDE  # scripted group (container) (typed FeaturePython)
  Dunit = g/cm3
  Dvalue = 3.667
  Group = -> [Na_element015,I_element009]
  conduct = 2
  density = 1
  expand = 3
  formula = G4_SODIUM_IODIDE
  name = G4_SODIUM_IODIDE
  specific = 4
FEATURE [App::DocumentObjectGroupPython] Na_element016  label="Na_element : 003"  # scripted group (container) (typed FeaturePython)
  n = 2
  ref = Na_element
FEATURE [App::DocumentObjectGroupPython] O_element090  label="O_element : 050"  # scripted group (container) (typed FeaturePython)
  n = 1
  ref = O_element
FEATURE [App::DocumentObjectGroupPython] G4_SODIUM_MONOXIDE  # scripted group (container) (typed FeaturePython)
  Dunit = g/cm3
  Dvalue = 2.27
  Group = -> [Na_element016,O_element090]
  conduct = 2
  density = 1
  expand = 3
  formula = G4_SODIUM_MONOXIDE
  name = G4_SODIUM_MONOXIDE
  specific = 4
FEATURE [App::DocumentObjectGroupPython] Na_element017  label="Na_element : 004"  # scripted group (container) (typed FeaturePython)
  n = 1
  ref = Na_element
FEATURE [App::DocumentObjectGroupPython] N_element040  label="N_element : 018"  # scripted group (container) (typed FeaturePython)
  n = 1
  ref = N_element
FEATURE [App::DocumentObjectGroupPython] O_element091  label="O_element : 051"  # scripted group (container) (typed FeaturePython)
  n = 3
  ref = O_element
FEATURE [App::DocumentObjectGroupPython] G4_SODIUM_NITRATE  # scripted group (container) (typed FeaturePython)
  Dunit = g/cm3
  Dvalue = 2.261
  Group = -> [Na_element017,N_element040,O_element091]
  conduct = 2
  density = 1
  expand = 3
  formula = G4_SODIUM_NITRATE
  name = G4_SODIUM_NITRATE
  specific = 4
FEATURE [App::DocumentObjectGroupPython] C_element105  label="C_element : 059"  # scripted group (container) (typed FeaturePython)
  n = 14
  ref = C_element
FEATURE [App::DocumentObjectGroupPython] H_element096  label="H_element : 053"  # scripted group (container) (typed FeaturePython)
  n = 12
  ref = H_element
FEATURE [App::DocumentObjectGroupPython] G4_STILBENE  # scripted group (container) (typed FeaturePython)
  Dunit = g/cm3
  Dvalue = 0.9707
  Group = -> [C_element105,H_element096]
  conduct = 2
  density = 1
  expand = 3
  formula = G4_STILBENE
  name = G4_STILBENE
  specific = 4
FEATURE [App::DocumentObjectGroupPython] C_element106  label="C_element : 12"  # scripted group (container) (typed FeaturePython)
  n = 12
  ref = C_element
FEATURE [App::DocumentObjectGroupPython] H_element097  label="H_element : 22"  # scripted group (container) (typed FeaturePython)
  n = 22
  ref = H_element
FEATURE [App::DocumentObjectGroupPython] O_element092  label="O_element : 11"  # scripted group (container) (typed FeaturePython)
  n = 11
  ref = O_element
FEATURE [App::DocumentObjectGroupPython] G4_SUCROSE  # scripted group (container) (typed FeaturePython)
  Dunit = g/cm3
  Dvalue = 1.5805
  Group = -> [C_element106,H_element097,O_element092]
  conduct = 2
  density = 1
  expand = 3
  formula = G4_SUCROSE
  name = G4_SUCROSE
  specific = 4
FEATURE [App::DocumentObjectGroupPython] C_element107  label="C_element : 18"  # scripted group (container) (typed FeaturePython)
  n = 18
  ref = C_element
FEATURE [App::DocumentObjectGroupPython] H_element098  label="H_element : 054"  # scripted group (container) (typed FeaturePython)
  n = 14
  ref = H_element
FEATURE [App::DocumentObjectGroupPython] G4_TERPHENYL  # scripted group (container) (typed FeaturePython)
  Dunit = g/cm3
  Dvalue = 1.24
  Group = -> [C_element107,H_element098]
  conduct = 2
  density = 1
  expand = 3
  formula = G4_TERPHENYL
  name = G4_TERPHENYL
  specific = 4
FEATURE [App::DocumentObjectGroupPython] H_element099  label="H_element : 0.146"  # scripted group (container) (typed FeaturePython)
  n = 0.106
FEATURE [App::DocumentObjectGroupPython] C_element108  label="C_element : 0.883"  # scripted group (container) (typed FeaturePython)
  n = 0.099
FEATURE [App::DocumentObjectGroupPython] N_element041  label="N_element : 0.020"  # scripted group (container) (typed FeaturePython)
  n = 0.02
FEATURE [App::DocumentObjectGroupPython] O_element093  label="O_element : 0.766"  # scripted group (container) (typed FeaturePython)
  n = 0.766
FEATURE [App::DocumentObjectGroupPython] Na_element018  label="Na_element : 0.101"  # scripted group (container) (typed FeaturePython)
  n = 0.002
FEATURE [App::DocumentObjectGroupPython] P_element010  label="P_element : 0.108"  # scripted group (container) (typed FeaturePython)
  n = 0.001
FEATURE [App::DocumentObjectGroupPython] S_element021  label="S_element : 0.022"  # scripted group (container) (typed FeaturePython)
  n = 0.002
FEATURE [App::DocumentObjectGroupPython] Cl_element024  label="Cl_element : 0.002"  # scripted group (container) (typed FeaturePython)
  n = 0.002
FEATURE [App::DocumentObjectGroupPython] K_element011  label="K_element : 0.017"  # scripted group (container) (typed FeaturePython)
  n = 0.002
FEATURE [App::DocumentObjectGroupPython] G4_TESTIS_ICRP  # scripted group (container) (typed FeaturePython)
  Dunit = g/cm3
  Dvalue = 1.04
  Group = -> [H_element099,C_element108,N_element041,O_element093,Na_element018,P_element010,S_element021,Cl_element024,K_element011]
  conduct = 2
  density = 1
  expand = 3
  formula = G4_TESTIS_ICRP
  name = G4_TESTIS_ICRP
  specific = 4
FEATURE [App::DocumentObjectGroupPython] C_element109  label="C_element : 060"  # scripted group (container) (typed FeaturePython)
  n = 2
  ref = C_element
FEATURE [App::DocumentObjectGroupPython] Cl_element025  label="Cl_element : 012"  # scripted group (container) (typed FeaturePython)
  n = 4
  ref = Cl_element
FEATURE [App::DocumentObjectGroupPython] G4_TETRACHLOROETHYLENE  # scripted group (container) (typed FeaturePython)
  Dunit = g/cm3
  Dvalue = 1.625
  Group = -> [C_element109,Cl_element025]
  conduct = 2
  density = 1
  expand = 3
  formula = G4_TETRACHLOROETHYLENE
  name = G4_TETRACHLOROETHYLENE
  specific = 4
FEATURE [App::DocumentObjectGroupPython] Tl_element001  label="Tl_element : 1"  # scripted group (container) (typed FeaturePython)
  n = 1
  ref = Tl_element
FEATURE [App::DocumentObjectGroupPython] Cl_element026  label="Cl_element : 013"  # scripted group (container) (typed FeaturePython)
  n = 1
  ref = Cl_element
FEATURE [App::DocumentObjectGroupPython] G4_THALLIUM_CHLORIDE  # scripted group (container) (typed FeaturePython)
  Dunit = g/cm3
  Dvalue = 7.004
  Group = -> [Tl_element001,Cl_element026]
  conduct = 2
  density = 1
  expand = 3
  formula = G4_THALLIUM_CHLORIDE
  name = G4_THALLIUM_CHLORIDE
  specific = 4
FEATURE [App::DocumentObjectGroupPython] H_element100  label="H_element : 0.147"  # scripted group (container) (typed FeaturePython)
  n = 0.105
FEATURE [App::DocumentObjectGroupPython] C_element110  label="C_element : 0.256"  # scripted group (container) (typed FeaturePython)
  n = 0.256
FEATURE [App::DocumentObjectGroupPython] N_element042  label="N_element : 0.760"  # scripted group (container) (typed FeaturePython)
  n = 0.027
FEATURE [App::DocumentObjectGroupPython] O_element094  label="O_element : 0.602"  # scripted group (container) (typed FeaturePython)
  n = 0.602
FEATURE [App::DocumentObjectGroupPython] Na_element019  label="Na_element : 0.102"  # scripted group (container) (typed FeaturePython)
  n = 0.001
FEATURE [App::DocumentObjectGroupPython] P_element011  label="P_element : 0.109"  # scripted group (container) (typed FeaturePython)
  n = 0.002
FEATURE [App::DocumentObjectGroupPython] S_element022  label="S_element : 0.023"  # scripted group (container) (typed FeaturePython)
  n = 0.003
FEATURE [App::DocumentObjectGroupPython] Cl_element027  label="Cl_element : 0.591"  # scripted group (container) (typed FeaturePython)
  n = 0.002
FEATURE [App::DocumentObjectGroupPython] K_element012  label="K_element : 0.018"  # scripted group (container) (typed FeaturePython)
  n = 0.002
FEATURE [App::DocumentObjectGroupPython] G4_TISSUE_SOFT_ICRP  # scripted group (container) (typed FeaturePython)
  Dunit = g/cm3
  Dvalue = 1.03
  Group = -> [H_element100,C_element110,N_element042,O_element094,Na_element019,P_element011,S_element022,Cl_element027,K_element012]
  conduct = 2
  density = 1
  expand = 3
  formula = G4_TISSUE_SOFT_ICRP
  name = G4_TISSUE_SOFT_ICRP
  specific = 4
FEATURE [App::DocumentObjectGroupPython] H_element101  label="H_element : 0.148"  # scripted group (container) (typed FeaturePython)
  n = 0.101
FEATURE [App::DocumentObjectGroupPython] C_element111  label="C_element : 0.111"  # scripted group (container) (typed FeaturePython)
  n = 0.111
FEATURE [App::DocumentObjectGroupPython] N_element043  label="N_element : 0.026"  # scripted group (container) (typed FeaturePython)
  n = 0.026
FEATURE [App::DocumentObjectGroupPython] O_element095  label="O_element : 0.762"  # scripted group (container) (typed FeaturePython)
  n = 0.762
FEATURE [App::DocumentObjectGroupPython] G4_TISSUE_SOFT_ICRU_4  label="G4_TISSUE_SOFT_ICRU-4"  # scripted group (container) (typed FeaturePython)
  Dunit = g/cm3
  Dvalue = 1
  Group = -> [H_element101,C_element111,N_element043,O_element095]
  conduct = 2
  density = 1
  expand = 3
  formula = G4_TISSUE_SOFT_ICRU-4
  name = G4_TISSUE_SOFT_ICRU-4
  specific = 4
FEATURE [App::DocumentObjectGroupPython] H_element102  label="H_element : 0.149"  # scripted group (container) (typed FeaturePython)
  n = 0.101869
FEATURE [App::DocumentObjectGroupPython] C_element112  label="C_element : 0.456"  # scripted group (container) (typed FeaturePython)
  n = 0.456179
FEATURE [App::DocumentObjectGroupPython] N_element044  label="N_element : 0.761"  # scripted group (container) (typed FeaturePython)
  n = 0.035172
FEATURE [App::DocumentObjectGroupPython] O_element096  label="O_element : 0.407"  # scripted group (container) (typed FeaturePython)
  n = 0.40678
FEATURE [App::DocumentObjectGroupPython] G4_TISSUE_METHANE  label="G4_TISSUE-METHANE"  # scripted group (container) (typed FeaturePython)
  Dunit = g/cm3
  Dvalue = 0.00106409
  Group = -> [H_element102,C_element112,N_element044,O_element096]
  conduct = 2
  density = 1
  expand = 3
  formula = G4_TISSUE-METHANE
  name = G4_TISSUE-METHANE
  specific = 4
FEATURE [App::DocumentObjectGroupPython] H_element103  label="H_element : 0.103"  # scripted group (container) (typed FeaturePython)
  n = 0.102672
FEATURE [App::DocumentObjectGroupPython] C_element113  label="C_element : 0.569"  # scripted group (container) (typed FeaturePython)
  n = 0.56894
FEATURE [App::DocumentObjectGroupPython] N_element045  label="N_element : 0.762"  # scripted group (container) (typed FeaturePython)
  n = 0.035022
FEATURE [App::DocumentObjectGroupPython] O_element097  label="O_element : 0.293"  # scripted group (container) (typed FeaturePython)
  n = 0.293366
FEATURE [App::DocumentObjectGroupPython] G4_TISSUE_PROPANE  label="G4_TISSUE-PROPANE"  # scripted group (container) (typed FeaturePython)
  Dunit = g/cm3
  Dvalue = 0.00182628
  Group = -> [H_element103,C_element113,N_element045,O_element097]
  conduct = 2
  density = 1
  expand = 3
  formula = G4_TISSUE-PROPANE
  name = G4_TISSUE-PROPANE
  specific = 4
FEATURE [App::DocumentObjectGroupPython] Ti_element003  label="Ti_element : 1"  # scripted group (container) (typed FeaturePython)
  n = 1
  ref = Ti_element
FEATURE [App::DocumentObjectGroupPython] O_element098  label="O_element : 052"  # scripted group (container) (typed FeaturePython)
  n = 2
  ref = O_element
FEATURE [App::DocumentObjectGroupPython] G4_TITANIUM_DIOXIDE  # scripted group (container) (typed FeaturePython)
  Dunit = g/cm3
  Dvalue = 4.26
  Group = -> [Ti_element003,O_element098]
  conduct = 2
  density = 1
  expand = 3
  formula = G4_TITANIUM_DIOXIDE
  name = G4_TITANIUM_DIOXIDE
  specific = 4
FEATURE [App::DocumentObjectGroupPython] C_element114  label="C_element : 061"  # scripted group (container) (typed FeaturePython)
  n = 7
  ref = C_element
FEATURE [App::DocumentObjectGroupPython] H_element104  label="H_element : 055"  # scripted group (container) (typed FeaturePython)
  n = 8
  ref = H_element
FEATURE [App::DocumentObjectGroupPython] G4_TOLUENE  # scripted group (container) (typed FeaturePython)
  Dunit = g/cm3
  Dvalue = 0.8669
  Group = -> [C_element114,H_element104]
  conduct = 2
  density = 1
  expand = 3
  formula = G4_TOLUENE
  name = G4_TOLUENE
  specific = 4
FEATURE [App::DocumentObjectGroupPython] C_element115  label="C_element : 062"  # scripted group (container) (typed FeaturePython)
  n = 2
  ref = C_element
FEATURE [App::DocumentObjectGroupPython] H_element105  label="H_element : 056"  # scripted group (container) (typed FeaturePython)
  n = 1
  ref = H_element
FEATURE [App::DocumentObjectGroupPython] Cl_element028  label="Cl_element : 014"  # scripted group (container) (typed FeaturePython)
  n = 3
  ref = Cl_element
FEATURE [App::DocumentObjectGroupPython] G4_TRICHLOROETHYLENE  # scripted group (container) (typed FeaturePython)
  Dunit = g/cm3
  Dvalue = 1.46
  Group = -> [C_element115,H_element105,Cl_element028]
  conduct = 2
  density = 1
  expand = 3
  formula = G4_TRICHLOROETHYLENE
  name = G4_TRICHLOROETHYLENE
  specific = 4
FEATURE [App::DocumentObjectGroupPython] C_element116  label="C_element : 063"  # scripted group (container) (typed FeaturePython)
  n = 6
  ref = C_element
FEATURE [App::DocumentObjectGroupPython] H_element106  label="H_element : 15"  # scripted group (container) (typed FeaturePython)
  n = 15
  ref = H_element
FEATURE [App::DocumentObjectGroupPython] O_element099  label="O_element : 053"  # scripted group (container) (typed FeaturePython)
  n = 4
  ref = O_element
FEATURE [App::DocumentObjectGroupPython] P_element012  label="P_element : 1"  # scripted group (container) (typed FeaturePython)
  n = 1
  ref = P_element
FEATURE [App::DocumentObjectGroupPython] G4_TRIETHYL_PHOSPHATE  # scripted group (container) (typed FeaturePython)
  Dunit = g/cm3
  Dvalue = 1.07
  Group = -> [C_element116,H_element106,O_element099,P_element012]
  conduct = 2
  density = 1
  expand = 3
  formula = G4_TRIETHYL_PHOSPHATE
  name = G4_TRIETHYL_PHOSPHATE
  specific = 4
FEATURE [App::DocumentObjectGroupPython] W_element003  label="W_element : 003"  # scripted group (container) (typed FeaturePython)
  n = 1
  ref = W_element
FEATURE [App::DocumentObjectGroupPython] F_element017  label="F_element : 6"  # scripted group (container) (typed FeaturePython)
  n = 6
  ref = F_element
FEATURE [App::DocumentObjectGroupPython] G4_TUNGSTEN_HEXAFLUORIDE  # scripted group (container) (typed FeaturePython)
  Dunit = g/cm3
  Dvalue = 2.4
  Group = -> [W_element003,F_element017]
  conduct = 2
  density = 1
  expand = 3
  formula = G4_TUNGSTEN_HEXAFLUORIDE
  name = G4_TUNGSTEN_HEXAFLUORIDE
  specific = 4
FEATURE [App::DocumentObjectGroupPython] U_element001  label="U_element : 1"  # scripted group (container) (typed FeaturePython)
  n = 1
  ref = U_element
FEATURE [App::DocumentObjectGroupPython] C_element117  label="C_element : 064"  # scripted group (container) (typed FeaturePython)
  n = 2
  ref = C_element
FEATURE [App::DocumentObjectGroupPython] G4_URANIUM_DICARBIDE  # scripted group (container) (typed FeaturePython)
  Dunit = g/cm3
  Dvalue = 11.28
  Group = -> [U_element001,C_element117]
  conduct = 2
  density = 1
  expand = 3
  formula = G4_URANIUM_DICARBIDE
  name = G4_URANIUM_DICARBIDE
  specific = 4
FEATURE [App::DocumentObjectGroupPython] U_element002  label="U_element : 002"  # scripted group (container) (typed FeaturePython)
  n = 1
  ref = U_element
FEATURE [App::DocumentObjectGroupPython] C_element118  label="C_element : 065"  # scripted group (container) (typed FeaturePython)
  n = 1
  ref = C_element
FEATURE [App::DocumentObjectGroupPython] G4_URANIUM_MONOCARBIDE  # scripted group (container) (typed FeaturePython)
  Dunit = g/cm3
  Dvalue = 13.63
  Group = -> [U_element002,C_element118]
  conduct = 2
  density = 1
  expand = 3
  formula = G4_URANIUM_MONOCARBIDE
  name = G4_URANIUM_MONOCARBIDE
  specific = 4
FEATURE [App::DocumentObjectGroupPython] U_element003  label="U_element : 003"  # scripted group (container) (typed FeaturePython)
  n = 1
  ref = U_element
FEATURE [App::DocumentObjectGroupPython] O_element100  label="O_element : 054"  # scripted group (container) (typed FeaturePython)
  n = 2
  ref = O_element
FEATURE [App::DocumentObjectGroupPython] G4_URANIUM_OXIDE  # scripted group (container) (typed FeaturePython)
  Dunit = g/cm3
  Dvalue = 10.96
  Group = -> [U_element003,O_element100]
  conduct = 2
  density = 1
  expand = 3
  formula = G4_URANIUM_OXIDE
  name = G4_URANIUM_OXIDE
  specific = 4
FEATURE [App::DocumentObjectGroupPython] C_element119  label="C_element : 066"  # scripted group (container) (typed FeaturePython)
  n = 1
  ref = C_element
FEATURE [App::DocumentObjectGroupPython] H_element107  label="H_element : 057"  # scripted group (container) (typed FeaturePython)
  n = 4
  ref = H_element
FEATURE [App::DocumentObjectGroupPython] N_element046  label="N_element : 019"  # scripted group (container) (typed FeaturePython)
  n = 2
  ref = N_element
FEATURE [App::DocumentObjectGroupPython] O_element101  label="O_element : 055"  # scripted group (container) (typed FeaturePython)
  n = 1
  ref = O_element
FEATURE [App::DocumentObjectGroupPython] G4_UREA  # scripted group (container) (typed FeaturePython)
  Dunit = g/cm3
  Dvalue = 1.323
  Group = -> [C_element119,H_element107,N_element046,O_element101]
  conduct = 2
  density = 1
  expand = 3
  formula = G4_UREA
  name = G4_UREA
  specific = 4
FEATURE [App::DocumentObjectGroupPython] C_element120  label="C_element : 067"  # scripted group (container) (typed FeaturePython)
  n = 5
  ref = C_element
FEATURE [App::DocumentObjectGroupPython] H_element108  label="H_element : 058"  # scripted group (container) (typed FeaturePython)
  n = 11
  ref = H_element
FEATURE [App::DocumentObjectGroupPython] N_element047  label="N_element : 020"  # scripted group (container) (typed FeaturePython)
  n = 1
  ref = N_element
FEATURE [App::DocumentObjectGroupPython] O_element102  label="O_element : 056"  # scripted group (container) (typed FeaturePython)
  n = 2
  ref = O_element
FEATURE [App::DocumentObjectGroupPython] G4_VALINE  # scripted group (container) (typed FeaturePython)
  Dunit = g/cm3
  Dvalue = 1.23
  Group = -> [C_element120,H_element108,N_element047,O_element102]
  conduct = 2
  density = 1
  expand = 3
  formula = G4_VALINE
  name = G4_VALINE
  specific = 4
FEATURE [App::DocumentObjectGroupPython] H_element109  label="H_element : 0.009"  # scripted group (container) (typed FeaturePython)
  n = 0.009417
FEATURE [App::DocumentObjectGroupPython] C_element121  label="C_element : 0.281"  # scripted group (container) (typed FeaturePython)
  n = 0.280555
FEATURE [App::DocumentObjectGroupPython] F_element018  label="F_element : 0.710"  # scripted group (container) (typed FeaturePython)
  n = 0.710028
FEATURE [App::DocumentObjectGroupPython] G4_VITON  # scripted group (container) (typed FeaturePython)
  Dunit = g/cm3
  Dvalue = 1.8
  Group = -> [H_element109,C_element121,F_element018]
  conduct = 2
  density = 1
  expand = 3
  formula = G4_VITON
  name = G4_VITON
  specific = 4
FEATURE [App::DocumentObjectGroupPython] H_element110  label="H_element : 059"  # scripted group (container) (typed FeaturePython)
  n = 2
  ref = H_element
FEATURE [App::DocumentObjectGroupPython] O_element103  label="O_element : 057"  # scripted group (container) (typed FeaturePython)
  n = 1
  ref = O_element
FEATURE [App::DocumentObjectGroupPython] G4_WATER  # scripted group (container) (typed FeaturePython)
  Dunit = g/cm3
  Dvalue = 1
  Group = -> [H_element110,O_element103]
  conduct = 2
  density = 1
  expand = 3
  formula = G4_WATER
  name = G4_WATER
  specific = 4
FEATURE [App::DocumentObjectGroupPython] H_element111  label="H_element : 060"  # scripted group (container) (typed FeaturePython)
  n = 2
  ref = H_element
FEATURE [App::DocumentObjectGroupPython] O_element104  label="O_element : 058"  # scripted group (container) (typed FeaturePython)
  n = 1
  ref = O_element
FEATURE [App::DocumentObjectGroupPython] G4_WATER_VAPOR  # scripted group (container) (typed FeaturePython)
  Dunit = g/cm3
  Dvalue = 0.000756182
  Group = -> [H_element111,O_element104]
  conduct = 2
  density = 1
  expand = 3
  formula = G4_WATER_VAPOR
  name = G4_WATER_VAPOR
  specific = 4
FEATURE [App::DocumentObjectGroupPython] C_element122  label="C_element : 068"  # scripted group (container) (typed FeaturePython)
  n = 8
  ref = C_element
FEATURE [App::DocumentObjectGroupPython] H_element112  label="H_element : 061"  # scripted group (container) (typed FeaturePython)
  n = 10
  ref = H_element
FEATURE [App::DocumentObjectGroupPython] G4_XYLENE  # scripted group (container) (typed FeaturePython)
  Dunit = g/cm3
  Dvalue = 0.87
  Group = -> [C_element122,H_element112]
  conduct = 2
  density = 1
  expand = 3
  formula = G4_XYLENE
  name = G4_XYLENE
  specific = 4
FEATURE [App::DocumentObjectGroupPython] C_element123  label="C_element : 069"  # scripted group (container) (typed FeaturePython)
  n = 1
  ref = C_element
FEATURE [App::DocumentObjectGroupPython] G4_GRAPHITE  # scripted group (container) (typed FeaturePython)
  Dunit = g/cm3
  Dvalue = 2.21
  Group = -> [C_element123]
  conduct = 2
  density = 1
  expand = 3
  formula = G4_GRAPHITE
  name = G4_GRAPHITE
  specific = 4
FEATURE [App::DocumentObjectGroupPython] NIST  # scripted group (container) (typed FeaturePython)
  Group = -> [G4_A_150_TISSUE,G4_ACETONE,G4_ACETYLENE,G4_ADENINE,G4_ADIPOSE_TISSUE_ICRP,G4_AIR,G4_ALANINE,G4_ALUMINUM_OXIDE,G4_AMBER,G4_AMMONIA,G4_ANILINE,G4_ANTHRACENE,G4_B_100_BONE,G4_BAKELITE,G4_BARIUM_FLUORIDE,G4_BARIUM_SULFATE,G4_BENZENE,G4_BERYLLIUM_OXIDE,G4_BGO,G4_BLOOD_ICRP,G4_BONE_COMPACT_ICRU,G4_BONE_CORTICAL_ICRP,G4_BORON_CARBIDE,G4_BORON_OXIDE,G4_BRAIN_ICRP,G4_BUTANE,G4_N_BUTYL_ALCOHOL,G4_C_552,+152 more]
FEATURE [App::DocumentObjectGroupPython] H_element113  label="H_element : 062"  # scripted group (container) (typed FeaturePython)
  n = 1
  ref = H_element
FEATURE [App::DocumentObjectGroupPython] G4_H  # scripted group (container) (typed FeaturePython)
  Dunit = g/cm3
  Dvalue = 8.3748e-05
  Group = -> [H_element113]
  conduct = 2
  density = 1
  expand = 3
  formula = H
  name = G4_H
  specific = 4
FEATURE [App::DocumentObjectGroupPython] He_element001  label="He_element : 1"  # scripted group (container) (typed FeaturePython)
  n = 1
  ref = He_element
FEATURE [App::DocumentObjectGroupPython] G4_He  # scripted group (container) (typed FeaturePython)
  Dunit = g/cm3
  Dvalue = 0.000166322
  Group = -> [He_element001]
  conduct = 2
  density = 1
  expand = 3
  formula = He
  name = G4_He
  specific = 4
FEATURE [App::DocumentObjectGroupPython] Li_element008  label="Li_element : 008"  # scripted group (container) (typed FeaturePython)
  n = 1
  ref = Li_element
FEATURE [App::DocumentObjectGroupPython] G4_Li  # scripted group (container) (typed FeaturePython)
  Dunit = g/cm3
  Dvalue = 0.534
  Group = -> [Li_element008]
  conduct = 2
  density = 1
  expand = 3
  formula = Li
  name = G4_Li
  specific = 4
FEATURE [App::DocumentObjectGroupPython] Be_element002  label="Be_element : 002"  # scripted group (container) (typed FeaturePython)
  n = 1
  ref = Be_element
FEATURE [App::DocumentObjectGroupPython] G4_Be  # scripted group (container) (typed FeaturePython)
  Dunit = g/cm3
  Dvalue = 1.848
  Group = -> [Be_element002]
  conduct = 2
  density = 1
  expand = 3
  formula = Be
  name = G4_Be
  specific = 4
FEATURE [App::DocumentObjectGroupPython] B_element007  label="B_element : 007"  # scripted group (container) (typed FeaturePython)
  n = 1
  ref = B_element
FEATURE [App::DocumentObjectGroupPython] G4_B  # scripted group (container) (typed FeaturePython)
  Dunit = g/cm3
  Dvalue = 2.37
  Group = -> [B_element007]
  conduct = 2
  density = 1
  expand = 3
  formula = B
  name = G4_B
  specific = 4
FEATURE [App::DocumentObjectGroupPython] C_element124  label="C_element : 070"  # scripted group (container) (typed FeaturePython)
  n = 1
  ref = C_element
FEATURE [App::DocumentObjectGroupPython] G4_C  # scripted group (container) (typed FeaturePython)
  Dunit = g/cm3
  Dvalue = 2
  Group = -> [C_element124]
  conduct = 2
  density = 1
  expand = 3
  formula = C
  name = G4_C
  specific = 4
FEATURE [App::DocumentObjectGroupPython] N_element048  label="N_element : 021"  # scripted group (container) (typed FeaturePython)
  n = 1
  ref = N_element
FEATURE [App::DocumentObjectGroupPython] G4_N  # scripted group (container) (typed FeaturePython)
  Dunit = g/cm3
  Dvalue = 0.0011652
  Group = -> [N_element048]
  conduct = 2
  density = 1
  expand = 3
  formula = N
  name = G4_N
  specific = 4
FEATURE [App::DocumentObjectGroupPython] O_element105  label="O_element : 059"  # scripted group (container) (typed FeaturePython)
  n = 1
  ref = O_element
FEATURE [App::DocumentObjectGroupPython] G4_O  # scripted group (container) (typed FeaturePython)
  Dunit = g/cm3
  Dvalue = 0.00133151
  Group = -> [O_element105]
  conduct = 2
  density = 1
  expand = 3
  formula = O
  name = G4_O
  specific = 4
FEATURE [App::DocumentObjectGroupPython] F_element019  label="F_element : 008"  # scripted group (container) (typed FeaturePython)
  n = 1
  ref = F_element
FEATURE [App::DocumentObjectGroupPython] G4_F  # scripted group (container) (typed FeaturePython)
  Dunit = g/cm3
  Dvalue = 0.00158029
  Group = -> [F_element019]
  conduct = 2
  density = 1
  expand = 3
  formula = F
  name = G4_F
  specific = 4
FEATURE [App::DocumentObjectGroupPython] Ne_element001  label="Ne_element : 1"  # scripted group (container) (typed FeaturePython)
  n = 1
  ref = Ne_element
FEATURE [App::DocumentObjectGroupPython] G4_Ne  # scripted group (container) (typed FeaturePython)
  Dunit = g/cm3
  Dvalue = 0.000838505
  Group = -> [Ne_element001]
  conduct = 2
  density = 1
  expand = 3
  formula = Ne
  name = G4_Ne
  specific = 4
FEATURE [App::DocumentObjectGroupPython] Na_element020  label="Na_element : 005"  # scripted group (container) (typed FeaturePython)
  n = 1
  ref = Na_element
FEATURE [App::DocumentObjectGroupPython] G4_Na  # scripted group (container) (typed FeaturePython)
  Dunit = g/cm3
  Dvalue = 0.971
  Group = -> [Na_element020]
  conduct = 2
  density = 1
  expand = 3
  formula = Na
  name = G4_Na
  specific = 4
FEATURE [App::DocumentObjectGroupPython] Mg_element011  label="Mg_element : 005"  # scripted group (container) (typed FeaturePython)
  n = 1
  ref = Mg_element
FEATURE [App::DocumentObjectGroupPython] G4_Mg  # scripted group (container) (typed FeaturePython)
  Dunit = g/cm3
  Dvalue = 1.74
  Group = -> [Mg_element011]
  conduct = 2
  density = 1
  expand = 3
  formula = Mg
  name = G4_Mg
  specific = 4
FEATURE [App::DocumentObjectGroupPython] Al_element004  label="Al_element : 1"  # scripted group (container) (typed FeaturePython)
  n = 1
  ref = Al_element
FEATURE [App::DocumentObjectGroupPython] G4_Al  # scripted group (container) (typed FeaturePython)
  Dunit = g/cm3
  Dvalue = 2.699
  Group = -> [Al_element004]
  conduct = 2
  density = 1
  expand = 3
  formula = Al
  name = G4_Al
  specific = 4
FEATURE [App::DocumentObjectGroupPython] Si_element007  label="Si_element : 002"  # scripted group (container) (typed FeaturePython)
  n = 1
  ref = Si_element
FEATURE [App::DocumentObjectGroupPython] G4_Si  # scripted group (container) (typed FeaturePython)
  Dunit = g/cm3
  Dvalue = 2.33
  Group = -> [Si_element007]
  conduct = 2
  density = 1
  expand = 3
  formula = Si
  name = G4_Si
  specific = 4
FEATURE [App::DocumentObjectGroupPython] P_element013  label="P_element : 002"  # scripted group (container) (typed FeaturePython)
  n = 1
  ref = P_element
FEATURE [App::DocumentObjectGroupPython] G4_P  # scripted group (container) (typed FeaturePython)
  Dunit = g/cm3
  Dvalue = 2.2
  Group = -> [P_element013]
  conduct = 2
  density = 1
  expand = 3
  formula = P
  name = G4_P
  specific = 4
FEATURE [App::DocumentObjectGroupPython] S_element023  label="S_element : 007"  # scripted group (container) (typed FeaturePython)
  n = 1
  ref = S_element
FEATURE [App::DocumentObjectGroupPython] G4_S  # scripted group (container) (typed FeaturePython)
  Dunit = g/cm3
  Dvalue = 2
  Group = -> [S_element023]
  conduct = 2
  density = 1
  expand = 3
  formula = S
  name = G4_S
  specific = 4
FEATURE [App::DocumentObjectGroupPython] Cl_element029  label="Cl_element : 015"  # scripted group (container) (typed FeaturePython)
  n = 1
  ref = Cl_element
FEATURE [App::DocumentObjectGroupPython] G4_Cl  # scripted group (container) (typed FeaturePython)
  Dunit = g/cm3
  Dvalue = 0.00299473
  Group = -> [Cl_element029]
  conduct = 2
  density = 1
  expand = 3
  formula = Cl
  name = G4_Cl
  specific = 4
FEATURE [App::DocumentObjectGroupPython] Ar_element002  label="Ar_element : 1"  # scripted group (container) (typed FeaturePython)
  n = 1
  ref = Ar_element
FEATURE [App::DocumentObjectGroupPython] G4_Ar  # scripted group (container) (typed FeaturePython)
  Dunit = g/cm3
  Dvalue = 0.00166201
  Group = -> [Ar_element002]
  conduct = 2
  density = 1
  expand = 3
  formula = Ar
  name = G4_Ar
  specific = 4
FEATURE [App::DocumentObjectGroupPython] K_element013  label="K_element : 003"  # scripted group (container) (typed FeaturePython)
  n = 1
  ref = K_element
FEATURE [App::DocumentObjectGroupPython] G4_K  # scripted group (container) (typed FeaturePython)
  Dunit = g/cm3
  Dvalue = 0.862
  Group = -> [K_element013]
  conduct = 2
  density = 1
  expand = 3
  formula = K
  name = G4_K
  specific = 4
FEATURE [App::DocumentObjectGroupPython] Ca_element014  label="Ca_element : 007"  # scripted group (container) (typed FeaturePython)
  n = 1
  ref = Ca_element
FEATURE [App::DocumentObjectGroupPython] G4_Ca  # scripted group (container) (typed FeaturePython)
  Dunit = g/cm3
  Dvalue = 1.55
  Group = -> [Ca_element014]
  conduct = 2
  density = 1
  expand = 3
  formula = Ca
  name = G4_Ca
  specific = 4
FEATURE [App::DocumentObjectGroupPython] Sc_element001  label="Sc_element : 1"  # scripted group (container) (typed FeaturePython)
  n = 1
  ref = Sc_element
FEATURE [App::DocumentObjectGroupPython] G4_Sc  # scripted group (container) (typed FeaturePython)
  Dunit = g/cm3
  Dvalue = 2.989
  Group = -> [Sc_element001]
  conduct = 2
  density = 1
  expand = 3
  formula = Sc
  name = G4_Sc
  specific = 4
FEATURE [App::DocumentObjectGroupPython] Ti_element004  label="Ti_element : 002"  # scripted group (container) (typed FeaturePython)
  n = 1
  ref = Ti_element
FEATURE [App::DocumentObjectGroupPython] G4_Ti  # scripted group (container) (typed FeaturePython)
  Dunit = g/cm3
  Dvalue = 4.54
  Group = -> [Ti_element004]
  conduct = 2
  density = 1
  expand = 3
  formula = Ti
  name = G4_Ti
  specific = 4
FEATURE [App::DocumentObjectGroupPython] V_element001  label="V_element : 1"  # scripted group (container) (typed FeaturePython)
  n = 1
  ref = V_element
FEATURE [App::DocumentObjectGroupPython] G4_V  # scripted group (container) (typed FeaturePython)
  Dunit = g/cm3
  Dvalue = 6.11
  Group = -> [V_element001]
  conduct = 2
  density = 1
  expand = 3
  formula = V
  name = G4_V
  specific = 4
FEATURE [App::DocumentObjectGroupPython] Cr_element001  label="Cr_element : 1"  # scripted group (container) (typed FeaturePython)
  n = 1
  ref = Cr_element
FEATURE [App::DocumentObjectGroupPython] G4_Cr  # scripted group (container) (typed FeaturePython)
  Dunit = g/cm3
  Dvalue = 7.18
  Group = -> [Cr_element001]
  conduct = 2
  density = 1
  expand = 3
  formula = Cr
  name = G4_Cr
  specific = 4
FEATURE [App::DocumentObjectGroupPython] Mn_element001  label="Mn_element : 1"  # scripted group (container) (typed FeaturePython)
  n = 1
  ref = Mn_element
FEATURE [App::DocumentObjectGroupPython] G4_Mn  # scripted group (container) (typed FeaturePython)
  Dunit = g/cm3
  Dvalue = 7.44
  Group = -> [Mn_element001]
  conduct = 2
  density = 1
  expand = 3
  formula = Mn
  name = G4_Mn
  specific = 4
FEATURE [App::DocumentObjectGroupPython] Fe_element007  label="Fe_element : 004"  # scripted group (container) (typed FeaturePython)
  n = 1
  ref = Fe_element
FEATURE [App::DocumentObjectGroupPython] G4_Fe  # scripted group (container) (typed FeaturePython)
  Dunit = g/cm3
  Dvalue = 7.874
  Group = -> [Fe_element007]
  conduct = 2
  density = 1
  expand = 3
  formula = Fe
  name = G4_Fe
  specific = 4
FEATURE [App::DocumentObjectGroupPython] Co_element001  label="Co_element : 1"  # scripted group (container) (typed FeaturePython)
  n = 1
  ref = Co_element
FEATURE [App::DocumentObjectGroupPython] G4_Co  # scripted group (container) (typed FeaturePython)
  Dunit = g/cm3
  Dvalue = 8.9
  Group = -> [Co_element001]
  conduct = 2
  density = 1
  expand = 3
  formula = Co
  name = G4_Co
  specific = 4
FEATURE [App::DocumentObjectGroupPython] Ni_element001  label="Ni_element : 1"  # scripted group (container) (typed FeaturePython)
  n = 1
  ref = Ni_element
FEATURE [App::DocumentObjectGroupPython] G4_Ni  # scripted group (container) (typed FeaturePython)
  Dunit = g/cm3
  Dvalue = 8.902
  Group = -> [Ni_element001]
  conduct = 2
  density = 1
  expand = 3
  formula = Ni
  name = G4_Ni
  specific = 4
FEATURE [App::DocumentObjectGroupPython] Cu_element001  label="Cu_element : 1"  # scripted group (container) (typed FeaturePython)
  n = 1
  ref = Cu_element
FEATURE [App::DocumentObjectGroupPython] G4_Cu  # scripted group (container) (typed FeaturePython)
  Dunit = g/cm3
  Dvalue = 8.96
  Group = -> [Cu_element001]
  conduct = 2
  density = 1
  expand = 3
  formula = Cu
  name = G4_Cu
  specific = 4
FEATURE [App::DocumentObjectGroupPython] Zn_element001  label="Zn_element : 1"  # scripted group (container) (typed FeaturePython)
  n = 1
  ref = Zn_element
FEATURE [App::DocumentObjectGroupPython] G4_Zn  # scripted group (container) (typed FeaturePython)
  Dunit = g/cm3
  Dvalue = 7.133
  Group = -> [Zn_element001]
  conduct = 2
  density = 1
  expand = 3
  formula = Zn
  name = G4_Zn
  specific = 4
FEATURE [App::DocumentObjectGroupPython] Ga_element002  label="Ga_element : 002"  # scripted group (container) (typed FeaturePython)
  n = 1
  ref = Ga_element
FEATURE [App::DocumentObjectGroupPython] G4_Ga  # scripted group (container) (typed FeaturePython)
  Dunit = g/cm3
  Dvalue = 5.904
  Group = -> [Ga_element002]
  conduct = 2
  density = 1
  expand = 3
  formula = Ga
  name = G4_Ga
  specific = 4
FEATURE [App::DocumentObjectGroupPython] Ge_element002  label="Ge_element : 1"  # scripted group (container) (typed FeaturePython)
  n = 1
  ref = Ge_element
FEATURE [App::DocumentObjectGroupPython] G4_Ge  # scripted group (container) (typed FeaturePython)
  Dunit = g/cm3
  Dvalue = 5.323
  Group = -> [Ge_element002]
  conduct = 2
  density = 1
  expand = 3
  formula = Ge
  name = G4_Ge
  specific = 4
FEATURE [App::DocumentObjectGroupPython] As_element003  label="As_element : 002"  # scripted group (container) (typed FeaturePython)
  n = 1
  ref = As_element
FEATURE [App::DocumentObjectGroupPython] G4_As  # scripted group (container) (typed FeaturePython)
  Dunit = g/cm3
  Dvalue = 5.73
  Group = -> [As_element003]
  conduct = 2
  density = 1
  expand = 3
  formula = As
  name = G4_As
  specific = 4
FEATURE [App::DocumentObjectGroupPython] Se_element001  label="Se_element : 1"  # scripted group (container) (typed FeaturePython)
  n = 1
  ref = Se_element
FEATURE [App::DocumentObjectGroupPython] G4_Se  # scripted group (container) (typed FeaturePython)
  Dunit = g/cm3
  Dvalue = 4.5
  Group = -> [Se_element001]
  conduct = 2
  density = 1
  expand = 3
  formula = Se
  name = G4_Se
  specific = 4
FEATURE [App::DocumentObjectGroupPython] Br_element007  label="Br_element : 004"  # scripted group (container) (typed FeaturePython)
  n = 1
  ref = Br_element
FEATURE [App::DocumentObjectGroupPython] G4_Br  # scripted group (container) (typed FeaturePython)
  Dunit = g/cm3
  Dvalue = 0.0070721
  Group = -> [Br_element007]
  conduct = 2
  density = 1
  expand = 3
  formula = Br
  name = G4_Br
  specific = 4
FEATURE [App::DocumentObjectGroupPython] Kr_element001  label="Kr_element : 1"  # scripted group (container) (typed FeaturePython)
  n = 1
  ref = Kr_element
FEATURE [App::DocumentObjectGroupPython] G4_Kr  # scripted group (container) (typed FeaturePython)
  Dunit = g/cm3
  Dvalue = 0.00347832
  Group = -> [Kr_element001]
  conduct = 2
  density = 1
  expand = 3
  formula = Kr
  name = G4_Kr
  specific = 4
FEATURE [App::DocumentObjectGroupPython] Rb_element001  label="Rb_element : 1"  # scripted group (container) (typed FeaturePython)
  n = 1
  ref = Rb_element
FEATURE [App::DocumentObjectGroupPython] G4_Rb  # scripted group (container) (typed FeaturePython)
  Dunit = g/cm3
  Dvalue = 1.532
  Group = -> [Rb_element001]
  conduct = 2
  density = 1
  expand = 3
  formula = Rb
  name = G4_Rb
  specific = 4
FEATURE [App::DocumentObjectGroupPython] Sr_element001  label="Sr_element : 1"  # scripted group (container) (typed FeaturePython)
  n = 1
  ref = Sr_element
FEATURE [App::DocumentObjectGroupPython] G4_Sr  # scripted group (container) (typed FeaturePython)
  Dunit = g/cm3
  Dvalue = 2.54
  Group = -> [Sr_element001]
  conduct = 2
  density = 1
  expand = 3
  formula = Sr
  name = G4_Sr
  specific = 4
FEATURE [App::DocumentObjectGroupPython] Y_element001  label="Y_element : 1"  # scripted group (container) (typed FeaturePython)
  n = 1
  ref = Y_element
FEATURE [App::DocumentObjectGroupPython] G4_Y  # scripted group (container) (typed FeaturePython)
  Dunit = g/cm3
  Dvalue = 4.469
  Group = -> [Y_element001]
  conduct = 2
  density = 1
  expand = 3
  formula = Y
  name = G4_Y
  specific = 4
FEATURE [App::DocumentObjectGroupPython] Zr_element001  label="Zr_element : 1"  # scripted group (container) (typed FeaturePython)
  n = 1
  ref = Zr_element
FEATURE [App::DocumentObjectGroupPython] G4_Zr  # scripted group (container) (typed FeaturePython)
  Dunit = g/cm3
  Dvalue = 6.506
  Group = -> [Zr_element001]
  conduct = 2
  density = 1
  expand = 3
  formula = Zr
  name = G4_Zr
  specific = 4
FEATURE [App::DocumentObjectGroupPython] Nb_element001  label="Nb_element : 1"  # scripted group (container) (typed FeaturePython)
  n = 1
  ref = Nb_element
FEATURE [App::DocumentObjectGroupPython] G4_Nb  # scripted group (container) (typed FeaturePython)
  Dunit = g/cm3
  Dvalue = 8.57
  Group = -> [Nb_element001]
  conduct = 2
  density = 1
  expand = 3
  formula = Nb
  name = G4_Nb
  specific = 4
FEATURE [App::DocumentObjectGroupPython] Mo_element001  label="Mo_element : 1"  # scripted group (container) (typed FeaturePython)
  n = 1
  ref = Mo_element
FEATURE [App::DocumentObjectGroupPython] G4_Mo  # scripted group (container) (typed FeaturePython)
  Dunit = g/cm3
  Dvalue = 10.22
  Group = -> [Mo_element001]
  conduct = 2
  density = 1
  expand = 3
  formula = Mo
  name = G4_Mo
  specific = 4
FEATURE [App::DocumentObjectGroupPython] Tc_element001  label="Tc_element : 1"  # scripted group (container) (typed FeaturePython)
  n = 1
  ref = Tc_element
FEATURE [App::DocumentObjectGroupPython] G4_Tc  # scripted group (container) (typed FeaturePython)
  Dunit = g/cm3
  Dvalue = 11.5
  Group = -> [Tc_element001]
  conduct = 2
  density = 1
  expand = 3
  formula = Tc
  name = G4_Tc
  specific = 4
FEATURE [App::DocumentObjectGroupPython] Ru_element001  label="Ru_element : 1"  # scripted group (container) (typed FeaturePython)
  n = 1
  ref = Ru_element
FEATURE [App::DocumentObjectGroupPython] G4_Ru  # scripted group (container) (typed FeaturePython)
  Dunit = g/cm3
  Dvalue = 12.41
  Group = -> [Ru_element001]
  conduct = 2
  density = 1
  expand = 3
  formula = Ru
  name = G4_Ru
  specific = 4
FEATURE [App::DocumentObjectGroupPython] Rh_element001  label="Rh_element : 1"  # scripted group (container) (typed FeaturePython)
  n = 1
  ref = Rh_element
FEATURE [App::DocumentObjectGroupPython] G4_Rh  # scripted group (container) (typed FeaturePython)
  Dunit = g/cm3
  Dvalue = 12.41
  Group = -> [Rh_element001]
  conduct = 2
  density = 1
  expand = 3
  formula = Rh
  name = G4_Rh
  specific = 4
FEATURE [App::DocumentObjectGroupPython] Pd_element001  label="Pd_element : 1"  # scripted group (container) (typed FeaturePython)
  n = 1
  ref = Pd_element
FEATURE [App::DocumentObjectGroupPython] G4_Pd  # scripted group (container) (typed FeaturePython)
  Dunit = g/cm3
  Dvalue = 12.02
  Group = -> [Pd_element001]
  conduct = 2
  density = 1
  expand = 3
  formula = Pd
  name = G4_Pd
  specific = 4
FEATURE [App::DocumentObjectGroupPython] Ag_element006  label="Ag_element : 004"  # scripted group (container) (typed FeaturePython)
  n = 1
  ref = Ag_element
FEATURE [App::DocumentObjectGroupPython] G4_Ag  # scripted group (container) (typed FeaturePython)
  Dunit = g/cm3
  Dvalue = 10.5
  Group = -> [Ag_element006]
  conduct = 2
  density = 1
  expand = 3
  formula = Ag
  name = G4_Ag
  specific = 4
FEATURE [App::DocumentObjectGroupPython] Cd_element003  label="Cd_element : 003"  # scripted group (container) (typed FeaturePython)
  n = 1
  ref = Cd_element
FEATURE [App::DocumentObjectGroupPython] G4_Cd  # scripted group (container) (typed FeaturePython)
  Dunit = g/cm3
  Dvalue = 8.65
  Group = -> [Cd_element003]
  conduct = 2
  density = 1
  expand = 3
  formula = Cd
  name = G4_Cd
  specific = 4
FEATURE [App::DocumentObjectGroupPython] In_element001  label="In_element : 1"  # scripted group (container) (typed FeaturePython)
  n = 1
  ref = In_element
FEATURE [App::DocumentObjectGroupPython] G4_In  # scripted group (container) (typed FeaturePython)
  Dunit = g/cm3
  Dvalue = 7.31
  Group = -> [In_element001]
  conduct = 2
  density = 1
  expand = 3
  formula = In
  name = G4_In
  specific = 4
FEATURE [App::DocumentObjectGroupPython] Sn_element001  label="Sn_element : 1"  # scripted group (container) (typed FeaturePython)
  n = 1
  ref = Sn_element
FEATURE [App::DocumentObjectGroupPython] G4_Sn  # scripted group (container) (typed FeaturePython)
  Dunit = g/cm3
  Dvalue = 7.31
  Group = -> [Sn_element001]
  conduct = 2
  density = 1
  expand = 3
  formula = Sn
  name = G4_Sn
  specific = 4
FEATURE [App::DocumentObjectGroupPython] Sb_element001  label="Sb_element : 1"  # scripted group (container) (typed FeaturePython)
  n = 1
  ref = Sb_element
FEATURE [App::DocumentObjectGroupPython] G4_Sb  # scripted group (container) (typed FeaturePython)
  Dunit = g/cm3
  Dvalue = 6.691
  Group = -> [Sb_element001]
  conduct = 2
  density = 1
  expand = 3
  formula = Sb
  name = G4_Sb
  specific = 4
FEATURE [App::DocumentObjectGroupPython] Te_element002  label="Te_element : 002"  # scripted group (container) (typed FeaturePython)
  n = 1
  ref = Te_element
FEATURE [App::DocumentObjectGroupPython] G4_Te  # scripted group (container) (typed FeaturePython)
  Dunit = g/cm3
  Dvalue = 6.24
  Group = -> [Te_element002]
  conduct = 2
  density = 1
  expand = 3
  formula = Te
  name = G4_Te
  specific = 4
FEATURE [App::DocumentObjectGroupPython] I_element010  label="I_element : 006"  # scripted group (container) (typed FeaturePython)
  n = 1
  ref = I_element
FEATURE [App::DocumentObjectGroupPython] G4_I  # scripted group (container) (typed FeaturePython)
  Dunit = g/cm3
  Dvalue = 4.93
  Group = -> [I_element010]
  conduct = 2
  density = 1
  expand = 3
  formula = I
  name = G4_I
  specific = 4
FEATURE [App::DocumentObjectGroupPython] Xe_element001  label="Xe_element : 1"  # scripted group (container) (typed FeaturePython)
  n = 1
  ref = Xe_element
FEATURE [App::DocumentObjectGroupPython] G4_Xe  # scripted group (container) (typed FeaturePython)
  Dunit = g/cm3
  Dvalue = 0.00548536
  Group = -> [Xe_element001]
  conduct = 2
  density = 1
  expand = 3
  formula = Xe
  name = G4_Xe
  specific = 4
FEATURE [App::DocumentObjectGroupPython] Cs_element003  label="Cs_element : 003"  # scripted group (container) (typed FeaturePython)
  n = 1
  ref = Cs_element
FEATURE [App::DocumentObjectGroupPython] G4_Cs  # scripted group (container) (typed FeaturePython)
  Dunit = g/cm3
  Dvalue = 1.873
  Group = -> [Cs_element003]
  conduct = 2
  density = 1
  expand = 3
  formula = Cs
  name = G4_Cs
  specific = 4
FEATURE [App::DocumentObjectGroupPython] Ba_element003  label="Ba_element : 003"  # scripted group (container) (typed FeaturePython)
  n = 1
  ref = Ba_element
FEATURE [App::DocumentObjectGroupPython] G4_Ba  # scripted group (container) (typed FeaturePython)
  Dunit = g/cm3
  Dvalue = 3.5
  Group = -> [Ba_element003]
  conduct = 2
  density = 1
  expand = 3
  formula = Ba
  name = G4_Ba
  specific = 4
FEATURE [App::DocumentObjectGroupPython] La_element003  label="La_element : 003"  # scripted group (container) (typed FeaturePython)
  n = 1
  ref = La_element
FEATURE [App::DocumentObjectGroupPython] G4_La  # scripted group (container) (typed FeaturePython)
  Dunit = g/cm3
  Dvalue = 6.154
  Group = -> [La_element003]
  conduct = 2
  density = 1
  expand = 3
  formula = La
  name = G4_La
  specific = 4
FEATURE [App::DocumentObjectGroupPython] Ce_element002  label="Ce_element : 1"  # scripted group (container) (typed FeaturePython)
  n = 1
  ref = Ce_element
FEATURE [App::DocumentObjectGroupPython] G4_Ce  # scripted group (container) (typed FeaturePython)
  Dunit = g/cm3
  Dvalue = 6.657
  Group = -> [Ce_element002]
  conduct = 2
  density = 1
  expand = 3
  formula = Ce
  name = G4_Ce
  specific = 4
FEATURE [App::DocumentObjectGroupPython] Pr_element001  label="Pr_element : 1"  # scripted group (container) (typed FeaturePython)
  n = 1
  ref = Pr_element
FEATURE [App::DocumentObjectGroupPython] G4_Pr  # scripted group (container) (typed FeaturePython)
  Dunit = g/cm3
  Dvalue = 6.71
  Group = -> [Pr_element001]
  conduct = 2
  density = 1
  expand = 3
  formula = Pr
  name = G4_Pr
  specific = 4
FEATURE [App::DocumentObjectGroupPython] Nd_element001  label="Nd_element : 1"  # scripted group (container) (typed FeaturePython)
  n = 1
  ref = Nd_element
FEATURE [App::DocumentObjectGroupPython] G4_Nd  # scripted group (container) (typed FeaturePython)
  Dunit = g/cm3
  Dvalue = 6.9
  Group = -> [Nd_element001]
  conduct = 2
  density = 1
  expand = 3
  formula = Nd
  name = G4_Nd
  specific = 4
FEATURE [App::DocumentObjectGroupPython] Pm_element001  label="Pm_element : 1"  # scripted group (container) (typed FeaturePython)
  n = 1
  ref = Pm_element
FEATURE [App::DocumentObjectGroupPython] G4_Pm  # scripted group (container) (typed FeaturePython)
  Dunit = g/cm3
  Dvalue = 7.22
  Group = -> [Pm_element001]
  conduct = 2
  density = 1
  expand = 3
  formula = Pm
  name = G4_Pm
  specific = 4
FEATURE [App::DocumentObjectGroupPython] Sm_element001  label="Sm_element : 1"  # scripted group (container) (typed FeaturePython)
  n = 1
  ref = Sm_element
FEATURE [App::DocumentObjectGroupPython] G4_Sm  # scripted group (container) (typed FeaturePython)
  Dunit = g/cm3
  Dvalue = 7.46
  Group = -> [Sm_element001]
  conduct = 2
  density = 1
  expand = 3
  formula = Sm
  name = G4_Sm
  specific = 4
FEATURE [App::DocumentObjectGroupPython] Eu_element001  label="Eu_element : 1"  # scripted group (container) (typed FeaturePython)
  n = 1
  ref = Eu_element
FEATURE [App::DocumentObjectGroupPython] G4_Eu  # scripted group (container) (typed FeaturePython)
  Dunit = g/cm3
  Dvalue = 5.243
  Group = -> [Eu_element001]
  conduct = 2
  density = 1
  expand = 3
  formula = Eu
  name = G4_Eu
  specific = 4
FEATURE [App::DocumentObjectGroupPython] Gd_element002  label="Gd_element : 1"  # scripted group (container) (typed FeaturePython)
  n = 1
  ref = Gd_element
FEATURE [App::DocumentObjectGroupPython] G4_Gd  # scripted group (container) (typed FeaturePython)
  Dunit = g/cm3
  Dvalue = 7.9004
  Group = -> [Gd_element002]
  conduct = 2
  density = 1
  expand = 3
  formula = Gd
  name = G4_Gd
  specific = 4
FEATURE [App::DocumentObjectGroupPython] Tb_element001  label="Tb_element : 1"  # scripted group (container) (typed FeaturePython)
  n = 1
  ref = Tb_element
FEATURE [App::DocumentObjectGroupPython] G4_Tb  # scripted group (container) (typed FeaturePython)
  Dunit = g/cm3
  Dvalue = 8.229
  Group = -> [Tb_element001]
  conduct = 2
  density = 1
  expand = 3
  formula = Tb
  name = G4_Tb
  specific = 4
FEATURE [App::DocumentObjectGroupPython] Dy_element001  label="Dy_element : 1"  # scripted group (container) (typed FeaturePython)
  n = 1
  ref = Dy_element
FEATURE [App::DocumentObjectGroupPython] G4_Dy  # scripted group (container) (typed FeaturePython)
  Dunit = g/cm3
  Dvalue = 8.55
  Group = -> [Dy_element001]
  conduct = 2
  density = 1
  expand = 3
  formula = Dy
  name = G4_Dy
  specific = 4
FEATURE [App::DocumentObjectGroupPython] Ho_element001  label="Ho_element : 1"  # scripted group (container) (typed FeaturePython)
  n = 1
  ref = Ho_element
FEATURE [App::DocumentObjectGroupPython] G4_Ho  # scripted group (container) (typed FeaturePython)
  Dunit = g/cm3
  Dvalue = 8.795
  Group = -> [Ho_element001]
  conduct = 2
  density = 1
  expand = 3
  formula = Ho
  name = G4_Ho
  specific = 4
FEATURE [App::DocumentObjectGroupPython] Er_element001  label="Er_element : 1"  # scripted group (container) (typed FeaturePython)
  n = 1
  ref = Er_element
FEATURE [App::DocumentObjectGroupPython] G4_Er  # scripted group (container) (typed FeaturePython)
  Dunit = g/cm3
  Dvalue = 9.066
  Group = -> [Er_element001]
  conduct = 2
  density = 1
  expand = 3
  formula = Er
  name = G4_Er
  specific = 4
FEATURE [App::DocumentObjectGroupPython] Tm_element001  label="Tm_element : 1"  # scripted group (container) (typed FeaturePython)
  n = 1
  ref = Tm_element
FEATURE [App::DocumentObjectGroupPython] G4_Tm  # scripted group (container) (typed FeaturePython)
  Dunit = g/cm3
  Dvalue = 9.321
  Group = -> [Tm_element001]
  conduct = 2
  density = 1
  expand = 3
  formula = Tm
  name = G4_Tm
  specific = 4
FEATURE [App::DocumentObjectGroupPython] Yb_element001  label="Yb_element : 1"  # scripted group (container) (typed FeaturePython)
  n = 1
  ref = Yb_element
FEATURE [App::DocumentObjectGroupPython] G4_Yb  # scripted group (container) (typed FeaturePython)
  Dunit = g/cm3
  Dvalue = 6.73
  Group = -> [Yb_element001]
  conduct = 2
  density = 1
  expand = 3
  formula = Yb
  name = G4_Yb
  specific = 4
FEATURE [App::DocumentObjectGroupPython] Lu_element001  label="Lu_element : 1"  # scripted group (container) (typed FeaturePython)
  n = 1
  ref = Lu_element
FEATURE [App::DocumentObjectGroupPython] G4_Lu  # scripted group (container) (typed FeaturePython)
  Dunit = g/cm3
  Dvalue = 9.84
  Group = -> [Lu_element001]
  conduct = 2
  density = 1
  expand = 3
  formula = Lu
  name = G4_Lu
  specific = 4
FEATURE [App::DocumentObjectGroupPython] Hf_element001  label="Hf_element : 1"  # scripted group (container) (typed FeaturePython)
  n = 1
  ref = Hf_element
FEATURE [App::DocumentObjectGroupPython] G4_Hf  # scripted group (container) (typed FeaturePython)
  Dunit = g/cm3
  Dvalue = 13.31
  Group = -> [Hf_element001]
  conduct = 2
  density = 1
  expand = 3
  formula = Hf
  name = G4_Hf
  specific = 4
FEATURE [App::DocumentObjectGroupPython] Ta_element001  label="Ta_element : 1"  # scripted group (container) (typed FeaturePython)
  n = 1
  ref = Ta_element
FEATURE [App::DocumentObjectGroupPython] G4_Ta  # scripted group (container) (typed FeaturePython)
  Dunit = g/cm3
  Dvalue = 16.654
  Group = -> [Ta_element001]
  conduct = 2
  density = 1
  expand = 3
  formula = Ta
  name = G4_Ta
  specific = 4
FEATURE [App::DocumentObjectGroupPython] W_element004  label="W_element : 004"  # scripted group (container) (typed FeaturePython)
  n = 1
  ref = W_element
FEATURE [App::DocumentObjectGroupPython] G4_W  # scripted group (container) (typed FeaturePython)
  Dunit = g/cm3
  Dvalue = 19.3
  Group = -> [W_element004]
  conduct = 2
  density = 1
  expand = 3
  formula = W
  name = G4_W
  specific = 4
FEATURE [App::DocumentObjectGroupPython] Re_element001  label="Re_element : 1"  # scripted group (container) (typed FeaturePython)
  n = 1
  ref = Re_element
FEATURE [App::DocumentObjectGroupPython] G4_Re  # scripted group (container) (typed FeaturePython)
  Dunit = g/cm3
  Dvalue = 21.02
  Group = -> [Re_element001]
  conduct = 2
  density = 1
  expand = 3
  formula = Re
  name = G4_Re
  specific = 4
FEATURE [App::DocumentObjectGroupPython] Os_element001  label="Os_element : 1"  # scripted group (container) (typed FeaturePython)
  n = 1
  ref = Os_element
FEATURE [App::DocumentObjectGroupPython] G4_Os  # scripted group (container) (typed FeaturePython)
  Dunit = g/cm3
  Dvalue = 22.57
  Group = -> [Os_element001]
  conduct = 2
  density = 1
  expand = 3
  formula = Os
  name = G4_Os
  specific = 4
FEATURE [App::DocumentObjectGroupPython] Ir_element001  label="Ir_element : 1"  # scripted group (container) (typed FeaturePython)
  n = 1
  ref = Ir_element
FEATURE [App::DocumentObjectGroupPython] G4_Ir  # scripted group (container) (typed FeaturePython)
  Dunit = g/cm3
  Dvalue = 22.42
  Group = -> [Ir_element001]
  conduct = 2
  density = 1
  expand = 3
  formula = Ir
  name = G4_Ir
  specific = 4
FEATURE [App::DocumentObjectGroupPython] Pt_element001  label="Pt_element : 1"  # scripted group (container) (typed FeaturePython)
  n = 1
  ref = Pt_element
FEATURE [App::DocumentObjectGroupPython] G4_Pt  # scripted group (container) (typed FeaturePython)
  Dunit = g/cm3
  Dvalue = 21.45
  Group = -> [Pt_element001]
  conduct = 2
  density = 1
  expand = 3
  formula = Pt
  name = G4_Pt
  specific = 4
FEATURE [App::DocumentObjectGroupPython] Au_element001  label="Au_element : 1"  # scripted group (container) (typed FeaturePython)
  n = 1
  ref = Au_element
FEATURE [App::DocumentObjectGroupPython] G4_Au  # scripted group (container) (typed FeaturePython)
  Dunit = g/cm3
  Dvalue = 19.32
  Group = -> [Au_element001]
  conduct = 2
  density = 1
  expand = 3
  formula = Au
  name = G4_Au
  specific = 4
FEATURE [App::DocumentObjectGroupPython] Hg_element002  label="Hg_element : 002"  # scripted group (container) (typed FeaturePython)
  n = 1
  ref = Hg_element
FEATURE [App::DocumentObjectGroupPython] G4_Hg  # scripted group (container) (typed FeaturePython)
  Dunit = g/cm3
  Dvalue = 13.546
  Group = -> [Hg_element002]
  conduct = 2
  density = 1
  expand = 3
  formula = Hg
  name = G4_Hg
  specific = 4
FEATURE [App::DocumentObjectGroupPython] Tl_element002  label="Tl_element : 002"  # scripted group (container) (typed FeaturePython)
  n = 1
  ref = Tl_element
FEATURE [App::DocumentObjectGroupPython] G4_Tl  # scripted group (container) (typed FeaturePython)
  Dunit = g/cm3
  Dvalue = 11.72
  Group = -> [Tl_element002]
  conduct = 2
  density = 1
  expand = 3
  formula = Tl
  name = G4_Tl
  specific = 4
FEATURE [App::DocumentObjectGroupPython] Pb_element003  label="Pb_element : 1"  # scripted group (container) (typed FeaturePython)
  n = 1
  ref = Pb_element
FEATURE [App::DocumentObjectGroupPython] G4_Pb  # scripted group (container) (typed FeaturePython)
  Dunit = g/cm3
  Dvalue = 11.35
  Group = -> [Pb_element003]
  conduct = 2
  density = 1
  expand = 3
  formula = Pb
  name = G4_Pb
  specific = 4
FEATURE [App::DocumentObjectGroupPython] Bi_element002  label="Bi_element : 1"  # scripted group (container) (typed FeaturePython)
  n = 1
  ref = Bi_element
FEATURE [App::DocumentObjectGroupPython] G4_Bi  # scripted group (container) (typed FeaturePython)
  Dunit = g/cm3
  Dvalue = 9.747
  Group = -> [Bi_element002]
  conduct = 2
  density = 1
  expand = 3
  formula = Bi
  name = G4_Bi
  specific = 4
FEATURE [App::DocumentObjectGroupPython] Po_element001  label="Po_element : 1"  # scripted group (container) (typed FeaturePython)
  n = 1
  ref = Po_element
FEATURE [App::DocumentObjectGroupPython] G4_Po  # scripted group (container) (typed FeaturePython)
  Dunit = g/cm3
  Dvalue = 9.32
  Group = -> [Po_element001]
  conduct = 2
  density = 1
  expand = 3
  formula = Po
  name = G4_Po
  specific = 4
FEATURE [App::DocumentObjectGroupPython] At_element001  label="At_element : 1"  # scripted group (container) (typed FeaturePython)
  n = 1
  ref = At_element
FEATURE [App::DocumentObjectGroupPython] G4_At  # scripted group (container) (typed FeaturePython)
  Dunit = g/cm3
  Dvalue = 9.32
  Group = -> [At_element001]
  conduct = 2
  density = 1
  expand = 3
  formula = At
  name = G4_At
  specific = 4
FEATURE [App::DocumentObjectGroupPython] Rn_element001  label="Rn_element : 1"  # scripted group (container) (typed FeaturePython)
  n = 1
  ref = Rn_element
FEATURE [App::DocumentObjectGroupPython] G4_Rn  # scripted group (container) (typed FeaturePython)
  Dunit = g/cm3
  Dvalue = 0.00900662
  Group = -> [Rn_element001]
  conduct = 2
  density = 1
  expand = 3
  formula = Rn
  name = G4_Rn
  specific = 4
FEATURE [App::DocumentObjectGroupPython] Fr_element001  label="Fr_element : 1"  # scripted group (container) (typed FeaturePython)
  n = 1
  ref = Fr_element
FEATURE [App::DocumentObjectGroupPython] G4_Fr  # scripted group (container) (typed FeaturePython)
  Dunit = g/cm3
  Dvalue = 1
  Group = -> [Fr_element001]
  conduct = 2
  density = 1
  expand = 3
  formula = Fr
  name = G4_Fr
  specific = 4
FEATURE [App::DocumentObjectGroupPython] Ra_element001  label="Ra_element : 1"  # scripted group (container) (typed FeaturePython)
  n = 1
  ref = Ra_element
FEATURE [App::DocumentObjectGroupPython] G4_Ra  # scripted group (container) (typed FeaturePython)
  Dunit = g/cm3
  Dvalue = 5
  Group = -> [Ra_element001]
  conduct = 2
  density = 1
  expand = 3
  formula = Ra
  name = G4_Ra
  specific = 4
FEATURE [App::DocumentObjectGroupPython] Ac_element001  label="Ac_element : 1"  # scripted group (container) (typed FeaturePython)
  n = 1
  ref = Ac_element
FEATURE [App::DocumentObjectGroupPython] G4_Ac  # scripted group (container) (typed FeaturePython)
  Dunit = g/cm3
  Dvalue = 10.07
  Group = -> [Ac_element001]
  conduct = 2
  density = 1
  expand = 3
  formula = Ac
  name = G4_Ac
  specific = 4
FEATURE [App::DocumentObjectGroupPython] Th_element001  label="Th_element : 1"  # scripted group (container) (typed FeaturePython)
  n = 1
  ref = Th_element
FEATURE [App::DocumentObjectGroupPython] G4_Th  # scripted group (container) (typed FeaturePython)
  Dunit = g/cm3
  Dvalue = 11.72
  Group = -> [Th_element001]
  conduct = 2
  density = 1
  expand = 3
  formula = Th
  name = G4_Th
  specific = 4
FEATURE [App::DocumentObjectGroupPython] Pa_element001  label="Pa_element : 1"  # scripted group (container) (typed FeaturePython)
  n = 1
  ref = Pa_element
FEATURE [App::DocumentObjectGroupPython] G4_Pa  # scripted group (container) (typed FeaturePython)
  Dunit = g/cm3
  Dvalue = 15.37
  Group = -> [Pa_element001]
  conduct = 2
  density = 1
  expand = 3
  formula = Pa
  name = G4_Pa
  specific = 4
FEATURE [App::DocumentObjectGroupPython] U_element004  label="U_element : 004"  # scripted group (container) (typed FeaturePython)
  n = 1
  ref = U_element
FEATURE [App::DocumentObjectGroupPython] G4_U  # scripted group (container) (typed FeaturePython)
  Dunit = g/cm3
  Dvalue = 18.95
  Group = -> [U_element004]
  conduct = 2
  density = 1
  expand = 3
  formula = U
  name = G4_U
  specific = 4
FEATURE [App::DocumentObjectGroupPython] Np_element001  label="Np_element : 1"  # scripted group (container) (typed FeaturePython)
  n = 1
  ref = Np_element
FEATURE [App::DocumentObjectGroupPython] G4_Np  # scripted group (container) (typed FeaturePython)
  Dunit = g/cm3
  Dvalue = 20.25
  Group = -> [Np_element001]
  conduct = 2
  density = 1
  expand = 3
  formula = Np
  name = G4_Np
  specific = 4
FEATURE [App::DocumentObjectGroupPython] Pu_element002  label="Pu_element : 002"  # scripted group (container) (typed FeaturePython)
  n = 1
  ref = Pu_element
FEATURE [App::DocumentObjectGroupPython] G4_Pu  # scripted group (container) (typed FeaturePython)
  Dunit = g/cm3
  Dvalue = 19.84
  Group = -> [Pu_element002]
  conduct = 2
  density = 1
  expand = 3
  formula = Pu
  name = G4_Pu
  specific = 4
FEATURE [App::DocumentObjectGroupPython] Am_element001  label="Am_element : 1"  # scripted group (container) (typed FeaturePython)
  n = 1
  ref = Am_element
FEATURE [App::DocumentObjectGroupPython] G4_Am  # scripted group (container) (typed FeaturePython)
  Dunit = g/cm3
  Dvalue = 13.67
  Group = -> [Am_element001]
  conduct = 2
  density = 1
  expand = 3
  formula = Am
  name = G4_Am
  specific = 4
FEATURE [App::DocumentObjectGroupPython] Cm_element001  label="Cm_element : 1"  # scripted group (container) (typed FeaturePython)
  n = 1
  ref = Cm_element
FEATURE [App::DocumentObjectGroupPython] G4_Cm  # scripted group (container) (typed FeaturePython)
  Dunit = g/cm3
  Dvalue = 13.51
  Group = -> [Cm_element001]
  conduct = 2
  density = 1
  expand = 3
  formula = Cm
  name = G4_Cm
  specific = 4
FEATURE [App::DocumentObjectGroupPython] Bk_element001  label="Bk_element : 1"  # scripted group (container) (typed FeaturePython)
  n = 1
  ref = Bk_element
FEATURE [App::DocumentObjectGroupPython] G4_Bk  # scripted group (container) (typed FeaturePython)
  Dunit = g/cm3
  Dvalue = 14
  Group = -> [Bk_element001]
  conduct = 2
  density = 1
  expand = 3
  formula = Bk
  name = G4_Bk
  specific = 4
FEATURE [App::DocumentObjectGroupPython] Cf_element001  label="Cf_element : 1"  # scripted group (container) (typed FeaturePython)
  n = 1
  ref = Cf_element
FEATURE [App::DocumentObjectGroupPython] G4_Cf  # scripted group (container) (typed FeaturePython)
  Dunit = g/cm3
  Dvalue = 10
  Group = -> [Cf_element001]
  conduct = 2
  density = 1
  expand = 3
  formula = Cf
  name = G4_Cf
  specific = 4
FEATURE [App::DocumentObjectGroupPython] Element  # scripted group (container) (typed FeaturePython)
  Group = -> [G4_H,G4_He,G4_Li,G4_Be,G4_B,G4_C,G4_N,G4_O,G4_F,G4_Ne,G4_Na,G4_Mg,G4_Al,G4_Si,G4_P,G4_S,G4_Cl,G4_Ar,G4_K,G4_Ca,G4_Sc,G4_Ti,G4_V,G4_Cr,G4_Mn,G4_Fe,G4_Co,G4_Ni,G4_Cu,G4_Zn,G4_Ga,G4_Ge,G4_As,G4_Se,G4_Br,G4_Kr,G4_Rb,G4_Sr,G4_Y,G4_Zr,G4_Nb,G4_Mo,G4_Tc,G4_Ru,G4_Rh,G4_Pd,G4_Ag,G4_Cd,G4_In,G4_Sn,G4_Sb,G4_Te,G4_I,G4_Xe,G4_Cs,G4_Ba,G4_La,G4_Ce,G4_Pr,G4_Nd,G4_Pm,G4_Sm,G4_Eu,G4_Gd,G4_Tb,G4_Dy,G4_Ho,G4_Er,+30 more]
FEATURE [App::DocumentObjectGroupPython] H_element114  label="H_element : 063"  # scripted group (container) (typed FeaturePython)
  n = 2
  ref = H_element
FEATURE [App::DocumentObjectGroupPython] G4_lH2  # scripted group (container) (typed FeaturePython)
  Dunit = g/cm3
  Dvalue = 0.0708
  Group = -> [H_element114]
  conduct = 2
  density = 1
  expand = 3
  formula = G4_lH2
  name = G4_lH2
  specific = 4
FEATURE [App::DocumentObjectGroupPython] N_element049  label="N_element : 022"  # scripted group (container) (typed FeaturePython)
  n = 2
  ref = N_element
FEATURE [App::DocumentObjectGroupPython] G4_lN2  # scripted group (container) (typed FeaturePython)
  Dunit = g/cm3
  Dvalue = 0.807
  Group = -> [N_element049]
  conduct = 2
  density = 1
  expand = 3
  formula = G4_lN2
  name = G4_lN2
  specific = 4
FEATURE [App::DocumentObjectGroupPython] O_element106  label="O_element : 060"  # scripted group (container) (typed FeaturePython)
  n = 2
  ref = O_element
FEATURE [App::DocumentObjectGroupPython] G4_lO2  # scripted group (container) (typed FeaturePython)
  Dunit = g/cm3
  Dvalue = 1.141
  Group = -> [O_element106]
  conduct = 2
  density = 1
  expand = 3
  formula = G4_lO2
  name = G4_lO2
  specific = 4
FEATURE [App::DocumentObjectGroupPython] Ar_element003  label="Ar_element : 002"  # scripted group (container) (typed FeaturePython)
  n = 1
  ref = Ar_element
FEATURE [App::DocumentObjectGroupPython] G4_lAr  # scripted group (container) (typed FeaturePython)
  Dunit = g/cm3
  Dvalue = 1.396
  Group = -> [Ar_element003]
  conduct = 2
  density = 1
  expand = 3
  formula = G4_lAr
  name = G4_lAr
  specific = 4
FEATURE [App::DocumentObjectGroupPython] Br_element008  label="Br_element : 005"  # scripted group (container) (typed FeaturePython)
  n = 1
  ref = Br_element
FEATURE [App::DocumentObjectGroupPython] G4_lBr  # scripted group (container) (typed FeaturePython)
  Dunit = g/cm3
  Dvalue = 3.1028
  Group = -> [Br_element008]
  conduct = 2
  density = 1
  expand = 3
  formula = G4_lBr
  name = G4_lBr
  specific = 4
FEATURE [App::DocumentObjectGroupPython] Kr_element002  label="Kr_element : 002"  # scripted group (container) (typed FeaturePython)
  n = 1
  ref = Kr_element
FEATURE [App::DocumentObjectGroupPython] G4_lKr  # scripted group (container) (typed FeaturePython)
  Dunit = g/cm3
  Dvalue = 2.418
  Group = -> [Kr_element002]
  conduct = 2
  density = 1
  expand = 3
  formula = G4_lKr
  name = G4_lKr
  specific = 4
FEATURE [App::DocumentObjectGroupPython] Xe_element002  label="Xe_element : 002"  # scripted group (container) (typed FeaturePython)
  n = 1
  ref = Xe_element
FEATURE [App::DocumentObjectGroupPython] G4_lXe  # scripted group (container) (typed FeaturePython)
  Dunit = g/cm3
  Dvalue = 2.953
  Group = -> [Xe_element002]
  conduct = 2
  density = 1
  expand = 3
  formula = G4_lXe
  name = G4_lXe
  specific = 4
FEATURE [App::DocumentObjectGroupPython] O_element107  label="O_element : 061"  # scripted group (container) (typed FeaturePython)
  n = 4
  ref = O_element
FEATURE [App::DocumentObjectGroupPython] Pb_element004  label="Pb_element : 002"  # scripted group (container) (typed FeaturePython)
  n = 1
  ref = Pb_element
FEATURE [App::DocumentObjectGroupPython] W_element005  label="W_element : 005"  # scripted group (container) (typed FeaturePython)
  n = 1
  ref = W_element
FEATURE [App::DocumentObjectGroupPython] G4_PbWO4  # scripted group (container) (typed FeaturePython)
  Dunit = g/cm3
  Dvalue = 8.28
  Group = -> [O_element107,Pb_element004,W_element005]
  conduct = 2
  density = 1
  expand = 3
  formula = G4_PbWO4
  name = G4_PbWO4
  specific = 4
FEATURE [App::DocumentObjectGroupPython] H_element115  label="H_element : 064"  # scripted group (container) (typed FeaturePython)
  n = 1
  ref = H_element
FEATURE [App::DocumentObjectGroupPython] G4_Galactic  # scripted group (container) (typed FeaturePython)
  Dunit = g/cm3
  Dvalue = 0
  Group = -> [H_element115]
  conduct = 2
  density = 1
  expand = 3
  formula = G4_Galactic
  name = G4_Galactic
  specific = 4
FEATURE [App::DocumentObjectGroupPython] C_element125  label="C_element : 071"  # scripted group (container) (typed FeaturePython)
  n = 1
  ref = C_element
FEATURE [App::DocumentObjectGroupPython] G4_GRAPHITE_POROUS  # scripted group (container) (typed FeaturePython)
  Dunit = g/cm3
  Dvalue = 1.7
  Group = -> [C_element125]
  conduct = 2
  density = 1
  expand = 3
  formula = G4_GRAPHITE_POROUS
  name = G4_GRAPHITE_POROUS
  specific = 4
FEATURE [App::DocumentObjectGroupPython] H_element116  label="H_element : 0.150"  # scripted group (container) (typed FeaturePython)
  n = 0.080538
FEATURE [App::DocumentObjectGroupPython] C_element126  label="C_element : 0.600"  # scripted group (container) (typed FeaturePython)
  n = 0.599848
FEATURE [App::DocumentObjectGroupPython] O_element108  label="O_element : 0.320"  # scripted group (container) (typed FeaturePython)
  n = 0.319614
FEATURE [App::DocumentObjectGroupPython] G4_LUCITE  # scripted group (container) (typed FeaturePython)
  Dunit = g/cm3
  Dvalue = 1.19
  Group = -> [H_element116,C_element126,O_element108]
  conduct = 2
  density = 1
  expand = 3
  formula = G4_LUCITE
  name = G4_LUCITE
  specific = 4
FEATURE [App::DocumentObjectGroupPython] Cu_element002  label="Cu_element : 62"  # scripted group (container) (typed FeaturePython)
  n = 62
  ref = Cu_element
FEATURE [App::DocumentObjectGroupPython] Zn_element002  label="Zn_element : 35"  # scripted group (container) (typed FeaturePython)
  n = 35
  ref = Zn_element
FEATURE [App::DocumentObjectGroupPython] Pb_element005  label="Pb_element : 3"  # scripted group (container) (typed FeaturePython)
  n = 3
  ref = Pb_element
FEATURE [App::DocumentObjectGroupPython] G4_BRASS  # scripted group (container) (typed FeaturePython)
  Dunit = g/cm3
  Dvalue = 8.52
  Group = -> [Cu_element002,Zn_element002,Pb_element005]
  conduct = 2
  density = 1
  expand = 3
  formula = G4_BRASS
  name = G4_BRASS
  specific = 4
FEATURE [App::DocumentObjectGroupPython] Cu_element003  label="Cu_element : 89"  # scripted group (container) (typed FeaturePython)
  n = 89
  ref = Cu_element
FEATURE [App::DocumentObjectGroupPython] Zn_element003  label="Zn_element : 9"  # scripted group (container) (typed FeaturePython)
  n = 9
  ref = Zn_element
FEATURE [App::DocumentObjectGroupPython] Pb_element006  label="Pb_element : 2"  # scripted group (container) (typed FeaturePython)
  n = 2
  ref = Pb_element
FEATURE [App::DocumentObjectGroupPython] G4_BRONZE  # scripted group (container) (typed FeaturePython)
  Dunit = g/cm3
  Dvalue = 8.82
  Group = -> [Cu_element003,Zn_element003,Pb_element006]
  conduct = 2
  density = 1
  expand = 3
  formula = G4_BRONZE
  name = G4_BRONZE
  specific = 4
FEATURE [App::DocumentObjectGroupPython] Fe_element008  label="Fe_element : 74"  # scripted group (container) (typed FeaturePython)
  n = 74
  ref = Fe_element
FEATURE [App::DocumentObjectGroupPython] Cr_element002  label="Cr_element : 18"  # scripted group (container) (typed FeaturePython)
  n = 18
  ref = Cr_element
FEATURE [App::DocumentObjectGroupPython] Ni_element002  label="Ni_element : 8"  # scripted group (container) (typed FeaturePython)
  n = 8
  ref = Ni_element
FEATURE [App::DocumentObjectGroupPython] G4_STAINLESS_STEEL  label="G4_STAINLESS-STEEL"  # scripted group (container) (typed FeaturePython)
  Dunit = g/cm3
  Dvalue = 8
  Group = -> [Fe_element008,Cr_element002,Ni_element002]
  conduct = 2
  density = 1
  expand = 3
  formula = G4_STAINLESS-STEEL
  name = G4_STAINLESS-STEEL
  specific = 4
FEATURE [App::DocumentObjectGroupPython] H_element117  label="H_element : 065"  # scripted group (container) (typed FeaturePython)
  n = 18
  ref = H_element
FEATURE [App::DocumentObjectGroupPython] C_element127  label="C_element : 072"  # scripted group (container) (typed FeaturePython)
  n = 12
  ref = C_element
FEATURE [App::DocumentObjectGroupPython] O_element109  label="O_element : 062"  # scripted group (container) (typed FeaturePython)
  n = 7
  ref = O_element
FEATURE [App::DocumentObjectGroupPython] G4_CR39  # scripted group (container) (typed FeaturePython)
  Dunit = g/cm3
  Dvalue = 1.32
  Group = -> [H_element117,C_element127,O_element109]
  conduct = 2
  density = 1
  expand = 3
  formula = G4_CR39
  name = G4_CR39
  specific = 4
FEATURE [App::DocumentObjectGroupPython] H_element118  label="H_element : 38"  # scripted group (container) (typed FeaturePython)
  n = 38
  ref = H_element
FEATURE [App::DocumentObjectGroupPython] C_element128  label="C_element : 073"  # scripted group (container) (typed FeaturePython)
  n = 18
  ref = C_element
FEATURE [App::DocumentObjectGroupPython] O_element110  label="O_element : 063"  # scripted group (container) (typed FeaturePython)
  n = 1
  ref = O_element
FEATURE [App::DocumentObjectGroupPython] G4_OCTADECANOL  # scripted group (container) (typed FeaturePython)
  Dunit = g/cm3
  Dvalue = 0.812
  Group = -> [H_element118,C_element128,O_element110]
  conduct = 2
  density = 1
  expand = 3
  formula = G4_OCTADECANOL
  name = G4_OCTADECANOL
  specific = 4
FEATURE [App::DocumentObjectGroupPython] HEP  # scripted group (container) (typed FeaturePython)
  Group = -> [G4_lH2,G4_lN2,G4_lO2,G4_lAr,G4_lBr,G4_lKr,G4_lXe,G4_PbWO4,G4_Galactic,G4_GRAPHITE_POROUS,G4_LUCITE,G4_BRASS,G4_BRONZE,G4_STAINLESS_STEEL,G4_CR39,G4_OCTADECANOL]
FEATURE [App::DocumentObjectGroupPython] C_element129  label="C_element : 074"  # scripted group (container) (typed FeaturePython)
  n = 14
  ref = C_element
FEATURE [App::DocumentObjectGroupPython] H_element119  label="H_element : 066"  # scripted group (container) (typed FeaturePython)
  n = 10
  ref = H_element
FEATURE [App::DocumentObjectGroupPython] O_element111  label="O_element : 064"  # scripted group (container) (typed FeaturePython)
  n = 2
  ref = O_element
FEATURE [App::DocumentObjectGroupPython] N_element050  label="N_element : 023"  # scripted group (container) (typed FeaturePython)
  n = 2
  ref = N_element
FEATURE [App::DocumentObjectGroupPython] G4_KEVLAR  # scripted group (container) (typed FeaturePython)
  Dunit = g/cm3
  Dvalue = 1.44
  Group = -> [C_element129,H_element119,O_element111,N_element050]
  conduct = 2
  density = 1
  expand = 3
  formula = G4_KEVLAR
  name = G4_KEVLAR
  specific = 4
FEATURE [App::DocumentObjectGroupPython] C_element130  label="C_element : 075"  # scripted group (container) (typed FeaturePython)
  n = 10
  ref = C_element
FEATURE [App::DocumentObjectGroupPython] H_element120  label="H_element : 067"  # scripted group (container) (typed FeaturePython)
  n = 8
  ref = H_element
FEATURE [App::DocumentObjectGroupPython] O_element112  label="O_element : 065"  # scripted group (container) (typed FeaturePython)
  n = 4
  ref = O_element
FEATURE [App::DocumentObjectGroupPython] G4_DACRON  # scripted group (container) (typed FeaturePython)
  Dunit = g/cm3
  Dvalue = 1.4
  Group = -> [C_element130,H_element120,O_element112]
  conduct = 2
  density = 1
  expand = 3
  formula = G4_DACRON
  name = G4_DACRON
  specific = 4
FEATURE [App::DocumentObjectGroupPython] C_element131  label="C_element : 076"  # scripted group (container) (typed FeaturePython)
  n = 4
  ref = C_element
FEATURE [App::DocumentObjectGroupPython] H_element121  label="H_element : 068"  # scripted group (container) (typed FeaturePython)
  n = 5
  ref = H_element
FEATURE [App::DocumentObjectGroupPython] Cl_element030  label="Cl_element : 016"  # scripted group (container) (typed FeaturePython)
  n = 1
  ref = Cl_element
FEATURE [App::DocumentObjectGroupPython] G4_NEOPRENE  # scripted group (container) (typed FeaturePython)
  Dunit = g/cm3
  Dvalue = 1.23
  Group = -> [C_element131,H_element121,Cl_element030]
  conduct = 2
  density = 1
  expand = 3
  formula = G4_NEOPRENE
  name = G4_NEOPRENE
  specific = 4
FEATURE [App::DocumentObjectGroupPython] Space  # scripted group (container) (typed FeaturePython)
  Group = -> [G4_KEVLAR,G4_DACRON,G4_NEOPRENE]
FEATURE [App::DocumentObjectGroupPython] H_element122  label="H_element : 069"  # scripted group (container) (typed FeaturePython)
  n = 5
  ref = H_element
FEATURE [App::DocumentObjectGroupPython] C_element132  label="C_element : 077"  # scripted group (container) (typed FeaturePython)
  n = 4
  ref = C_element
FEATURE [App::DocumentObjectGroupPython] N_element051  label="N_element : 3"  # scripted group (container) (typed FeaturePython)
  n = 3
  ref = N_element
FEATURE [App::DocumentObjectGroupPython] O_element113  label="O_element : 066"  # scripted group (container) (typed FeaturePython)
  n = 1
  ref = O_element
FEATURE [App::DocumentObjectGroupPython] G4_CYTOSINE  # scripted group (container) (typed FeaturePython)
  Dunit = g/cm3
  Dvalue = 1.55
  Group = -> [H_element122,C_element132,N_element051,O_element113]
  conduct = 2
  density = 1
  expand = 3
  formula = G4_CYTOSINE
  name = G4_CYTOSINE
  specific = 4
FEATURE [App::DocumentObjectGroupPython] H_element123  label="H_element : 070"  # scripted group (container) (typed FeaturePython)
  n = 6
  ref = H_element
FEATURE [App::DocumentObjectGroupPython] C_element133  label="C_element : 078"  # scripted group (container) (typed FeaturePython)
  n = 5
  ref = C_element
FEATURE [App::DocumentObjectGroupPython] N_element052  label="N_element : 024"  # scripted group (container) (typed FeaturePython)
  n = 2
  ref = N_element
FEATURE [App::DocumentObjectGroupPython] O_element114  label="O_element : 067"  # scripted group (container) (typed FeaturePython)
  n = 2
  ref = O_element
FEATURE [App::DocumentObjectGroupPython] G4_THYMINE  # scripted group (container) (typed FeaturePython)
  Dunit = g/cm3
  Dvalue = 1.23
  Group = -> [H_element123,C_element133,N_element052,O_element114]
  conduct = 2
  density = 1
  expand = 3
  formula = G4_THYMINE
  name = G4_THYMINE
  specific = 4
FEATURE [App::DocumentObjectGroupPython] H_element124  label="H_element : 071"  # scripted group (container) (typed FeaturePython)
  n = 4
  ref = H_element
FEATURE [App::DocumentObjectGroupPython] C_element134  label="C_element : 079"  # scripted group (container) (typed FeaturePython)
  n = 4
  ref = C_element
FEATURE [App::DocumentObjectGroupPython] N_element053  label="N_element : 025"  # scripted group (container) (typed FeaturePython)
  n = 2
  ref = N_element
FEATURE [App::DocumentObjectGroupPython] O_element115  label="O_element : 068"  # scripted group (container) (typed FeaturePython)
  n = 2
  ref = O_element
FEATURE [App::DocumentObjectGroupPython] G4_URACIL  # scripted group (container) (typed FeaturePython)
  Dunit = g/cm3
  Dvalue = 1.32
  Group = -> [H_element124,C_element134,N_element053,O_element115]
  conduct = 2
  density = 1
  expand = 3
  formula = G4_URACIL
  name = G4_URACIL
  specific = 4
FEATURE [App::DocumentObjectGroupPython] H_element125  label="H_element : 072"  # scripted group (container) (typed FeaturePython)
  n = 4
  ref = H_element
FEATURE [App::DocumentObjectGroupPython] C_element135  label="C_element : 080"  # scripted group (container) (typed FeaturePython)
  n = 5
  ref = C_element
FEATURE [App::DocumentObjectGroupPython] N_element054  label="N_element : 026"  # scripted group (container) (typed FeaturePython)
  n = 5
  ref = N_element
FEATURE [App::DocumentObjectGroupPython] G4_DNA_ADENINE  # scripted group (container) (typed FeaturePython)
  Dunit = g/cm3
  Dvalue = 1
  Group = -> [H_element125,C_element135,N_element054]
  conduct = 2
  density = 1
  expand = 3
  formula = G4_DNA_ADENINE
  name = G4_DNA_ADENINE
  specific = 4
FEATURE [App::DocumentObjectGroupPython] H_element126  label="H_element : 073"  # scripted group (container) (typed FeaturePython)
  n = 4
  ref = H_element
FEATURE [App::DocumentObjectGroupPython] C_element136  label="C_element : 081"  # scripted group (container) (typed FeaturePython)
  n = 5
  ref = C_element
FEATURE [App::DocumentObjectGroupPython] N_element055  label="N_element : 027"  # scripted group (container) (typed FeaturePython)
  n = 5
  ref = N_element
FEATURE [App::DocumentObjectGroupPython] O_element116  label="O_element : 069"  # scripted group (container) (typed FeaturePython)
  n = 1
  ref = O_element
FEATURE [App::DocumentObjectGroupPython] G4_DNA_GUANINE  # scripted group (container) (typed FeaturePython)
  Dunit = g/cm3
  Dvalue = 1
  Group = -> [H_element126,C_element136,N_element055,O_element116]
  conduct = 2
  density = 1
  expand = 3
  formula = G4_DNA_GUANINE
  name = G4_DNA_GUANINE
  specific = 4
FEATURE [App::DocumentObjectGroupPython] H_element127  label="H_element : 074"  # scripted group (container) (typed FeaturePython)
  n = 4
  ref = H_element
FEATURE [App::DocumentObjectGroupPython] C_element137  label="C_element : 082"  # scripted group (container) (typed FeaturePython)
  n = 4
  ref = C_element
FEATURE [App::DocumentObjectGroupPython] N_element056  label="N_element : 028"  # scripted group (container) (typed FeaturePython)
  n = 3
  ref = N_element
FEATURE [App::DocumentObjectGroupPython] O_element117  label="O_element : 070"  # scripted group (container) (typed FeaturePython)
  n = 1
  ref = O_element
FEATURE [App::DocumentObjectGroupPython] G4_DNA_CYTOSINE  # scripted group (container) (typed FeaturePython)
  Dunit = g/cm3
  Dvalue = 1
  Group = -> [H_element127,C_element137,N_element056,O_element117]
  conduct = 2
  density = 1
  expand = 3
  formula = G4_DNA_CYTOSINE
  name = G4_DNA_CYTOSINE
  specific = 4
FEATURE [App::DocumentObjectGroupPython] H_element128  label="H_element : 075"  # scripted group (container) (typed FeaturePython)
  n = 5
  ref = H_element
FEATURE [App::DocumentObjectGroupPython] C_element138  label="C_element : 083"  # scripted group (container) (typed FeaturePython)
  n = 5
  ref = C_element
FEATURE [App::DocumentObjectGroupPython] N_element057  label="N_element : 029"  # scripted group (container) (typed FeaturePython)
  n = 2
  ref = N_element
FEATURE [App::DocumentObjectGroupPython] O_element118  label="O_element : 071"  # scripted group (container) (typed FeaturePython)
  n = 2
  ref = O_element
FEATURE [App::DocumentObjectGroupPython] G4_DNA_THYMINE  # scripted group (container) (typed FeaturePython)
  Dunit = g/cm3
  Dvalue = 1
  Group = -> [H_element128,C_element138,N_element057,O_element118]
  conduct = 2
  density = 1
  expand = 3
  formula = G4_DNA_THYMINE
  name = G4_DNA_THYMINE
  specific = 4
FEATURE [App::DocumentObjectGroupPython] H_element129  label="H_element : 076"  # scripted group (container) (typed FeaturePython)
  n = 3
  ref = H_element
FEATURE [App::DocumentObjectGroupPython] C_element139  label="C_element : 084"  # scripted group (container) (typed FeaturePython)
  n = 4
  ref = C_element
FEATURE [App::DocumentObjectGroupPython] N_element058  label="N_element : 030"  # scripted group (container) (typed FeaturePython)
  n = 2
  ref = N_element
FEATURE [App::DocumentObjectGroupPython] O_element119  label="O_element : 072"  # scripted group (container) (typed FeaturePython)
  n = 2
  ref = O_element
FEATURE [App::DocumentObjectGroupPython] G4_DNA_URACIL  # scripted group (container) (typed FeaturePython)
  Dunit = g/cm3
  Dvalue = 1
  Group = -> [H_element129,C_element139,N_element058,O_element119]
  conduct = 2
  density = 1
  expand = 3
  formula = G4_DNA_URACIL
  name = G4_DNA_URACIL
  specific = 4
FEATURE [App::DocumentObjectGroupPython] H_element130  label="H_element : 077"  # scripted group (container) (typed FeaturePython)
  n = 10
  ref = H_element
FEATURE [App::DocumentObjectGroupPython] C_element140  label="C_element : 085"  # scripted group (container) (typed FeaturePython)
  n = 10
  ref = C_element
FEATURE [App::DocumentObjectGroupPython] N_element059  label="N_element : 031"  # scripted group (container) (typed FeaturePython)
  n = 5
  ref = N_element
FEATURE [App::DocumentObjectGroupPython] O_element120  label="O_element : 073"  # scripted group (container) (typed FeaturePython)
  n = 4
  ref = O_element
FEATURE [App::DocumentObjectGroupPython] G4_DNA_ADENOSINE  # scripted group (container) (typed FeaturePython)
  Dunit = g/cm3
  Dvalue = 1
  Group = -> [H_element130,C_element140,N_element059,O_element120]
  conduct = 2
  density = 1
  expand = 3
  formula = G4_DNA_ADENOSINE
  name = G4_DNA_ADENOSINE
  specific = 4
FEATURE [App::DocumentObjectGroupPython] H_element131  label="H_element : 078"  # scripted group (container) (typed FeaturePython)
  n = 10
  ref = H_element
FEATURE [App::DocumentObjectGroupPython] C_element141  label="C_element : 086"  # scripted group (container) (typed FeaturePython)
  n = 10
  ref = C_element
FEATURE [App::DocumentObjectGroupPython] N_element060  label="N_element : 032"  # scripted group (container) (typed FeaturePython)
  n = 5
  ref = N_element
FEATURE [App::DocumentObjectGroupPython] O_element121  label="O_element : 074"  # scripted group (container) (typed FeaturePython)
  n = 5
  ref = O_element
FEATURE [App::DocumentObjectGroupPython] G4_DNA_GUANOSINE  # scripted group (container) (typed FeaturePython)
  Dunit = g/cm3
  Dvalue = 1
  Group = -> [H_element131,C_element141,N_element060,O_element121]
  conduct = 2
  density = 1
  expand = 3
  formula = G4_DNA_GUANOSINE
  name = G4_DNA_GUANOSINE
  specific = 4
FEATURE [App::DocumentObjectGroupPython] H_element132  label="H_element : 079"  # scripted group (container) (typed FeaturePython)
  n = 10
  ref = H_element
FEATURE [App::DocumentObjectGroupPython] C_element142  label="C_element : 087"  # scripted group (container) (typed FeaturePython)
  n = 9
  ref = C_element
FEATURE [App::DocumentObjectGroupPython] N_element061  label="N_element : 033"  # scripted group (container) (typed FeaturePython)
  n = 3
  ref = N_element
FEATURE [App::DocumentObjectGroupPython] O_element122  label="O_element : 075"  # scripted group (container) (typed FeaturePython)
  n = 5
  ref = O_element
FEATURE [App::DocumentObjectGroupPython] G4_DNA_CYTIDINE  # scripted group (container) (typed FeaturePython)
  Dunit = g/cm3
  Dvalue = 1
  Group = -> [H_element132,C_element142,N_element061,O_element122]
  conduct = 2
  density = 1
  expand = 3
  formula = G4_DNA_CYTIDINE
  name = G4_DNA_CYTIDINE
  specific = 4
FEATURE [App::DocumentObjectGroupPython] H_element133  label="H_element : 080"  # scripted group (container) (typed FeaturePython)
  n = 9
  ref = H_element
FEATURE [App::DocumentObjectGroupPython] C_element143  label="C_element : 088"  # scripted group (container) (typed FeaturePython)
  n = 9
  ref = C_element
FEATURE [App::DocumentObjectGroupPython] N_element062  label="N_element : 034"  # scripted group (container) (typed FeaturePython)
  n = 2
  ref = N_element
FEATURE [App::DocumentObjectGroupPython] O_element123  label="O_element : 076"  # scripted group (container) (typed FeaturePython)
  n = 6
  ref = O_element
FEATURE [App::DocumentObjectGroupPython] G4_DNA_URIDINE  # scripted group (container) (typed FeaturePython)
  Dunit = g/cm3
  Dvalue = 1
  Group = -> [H_element133,C_element143,N_element062,O_element123]
  conduct = 2
  density = 1
  expand = 3
  formula = G4_DNA_URIDINE
  name = G4_DNA_URIDINE
  specific = 4
FEATURE [App::DocumentObjectGroupPython] H_element134  label="H_element : 081"  # scripted group (container) (typed FeaturePython)
  n = 11
  ref = H_element
FEATURE [App::DocumentObjectGroupPython] C_element144  label="C_element : 089"  # scripted group (container) (typed FeaturePython)
  n = 10
  ref = C_element
FEATURE [App::DocumentObjectGroupPython] N_element063  label="N_element : 035"  # scripted group (container) (typed FeaturePython)
  n = 2
  ref = N_element
FEATURE [App::DocumentObjectGroupPython] O_element124  label="O_element : 077"  # scripted group (container) (typed FeaturePython)
  n = 6
  ref = O_element
FEATURE [App::DocumentObjectGroupPython] G4_DNA_METHYLURIDINE  # scripted group (container) (typed FeaturePython)
  Dunit = g/cm3
  Dvalue = 1
  Group = -> [H_element134,C_element144,N_element063,O_element124]
  conduct = 2
  density = 1
  expand = 3
  formula = G4_DNA_METHYLURIDINE
  name = G4_DNA_METHYLURIDINE
  specific = 4
FEATURE [App::DocumentObjectGroupPython] P_element014  label="P_element : 003"  # scripted group (container) (typed FeaturePython)
  n = 1
  ref = P_element
FEATURE [App::DocumentObjectGroupPython] O_element125  label="O_element : 078"  # scripted group (container) (typed FeaturePython)
  n = 3
  ref = O_element
FEATURE [App::DocumentObjectGroupPython] G4_DNA_MONOPHOSPHATE  # scripted group (container) (typed FeaturePython)
  Dunit = g/cm3
  Dvalue = 1
  Group = -> [P_element014,O_element125]
  conduct = 2
  density = 1
  expand = 3
  formula = G4_DNA_MONOPHOSPHATE
  name = G4_DNA_MONOPHOSPHATE
  specific = 4
FEATURE [App::DocumentObjectGroupPython] H_element135  label="H_element : 082"  # scripted group (container) (typed FeaturePython)
  n = 10
  ref = H_element
FEATURE [App::DocumentObjectGroupPython] C_element145  label="C_element : 090"  # scripted group (container) (typed FeaturePython)
  n = 10
  ref = C_element
FEATURE [App::DocumentObjectGroupPython] N_element064  label="N_element : 036"  # scripted group (container) (typed FeaturePython)
  n = 5
  ref = N_element
FEATURE [App::DocumentObjectGroupPython] O_element126  label="O_element : 079"  # scripted group (container) (typed FeaturePython)
  n = 7
  ref = O_element
FEATURE [App::DocumentObjectGroupPython] P_element015  label="P_element : 004"  # scripted group (container) (typed FeaturePython)
  n = 1
  ref = P_element
FEATURE [App::DocumentObjectGroupPython] G4_DNA_A  # scripted group (container) (typed FeaturePython)
  Dunit = g/cm3
  Dvalue = 1
  Group = -> [H_element135,C_element145,N_element064,O_element126,P_element015]
  conduct = 2
  density = 1
  expand = 3
  formula = G4_DNA_A
  name = G4_DNA_A
  specific = 4
FEATURE [App::DocumentObjectGroupPython] H_element136  label="H_element : 083"  # scripted group (container) (typed FeaturePython)
  n = 10
  ref = H_element
FEATURE [App::DocumentObjectGroupPython] C_element146  label="C_element : 091"  # scripted group (container) (typed FeaturePython)
  n = 10
  ref = C_element
FEATURE [App::DocumentObjectGroupPython] N_element065  label="N_element : 037"  # scripted group (container) (typed FeaturePython)
  n = 5
  ref = N_element
FEATURE [App::DocumentObjectGroupPython] O_element127  label="O_element : 8"  # scripted group (container) (typed FeaturePython)
  n = 8
  ref = O_element
FEATURE [App::DocumentObjectGroupPython] P_element016  label="P_element : 005"  # scripted group (container) (typed FeaturePython)
  n = 1
  ref = P_element
FEATURE [App::DocumentObjectGroupPython] G4_DNA_G  # scripted group (container) (typed FeaturePython)
  Dunit = g/cm3
  Dvalue = 1
  Group = -> [H_element136,C_element146,N_element065,O_element127,P_element016]
  conduct = 2
  density = 1
  expand = 3
  formula = G4_DNA_G
  name = G4_DNA_G
  specific = 4
FEATURE [App::DocumentObjectGroupPython] H_element137  label="H_element : 084"  # scripted group (container) (typed FeaturePython)
  n = 10
  ref = H_element
FEATURE [App::DocumentObjectGroupPython] C_element147  label="C_element : 092"  # scripted group (container) (typed FeaturePython)
  n = 9
  ref = C_element
FEATURE [App::DocumentObjectGroupPython] N_element066  label="N_element : 038"  # scripted group (container) (typed FeaturePython)
  n = 3
  ref = N_element
FEATURE [App::DocumentObjectGroupPython] O_element128  label="O_element : 080"  # scripted group (container) (typed FeaturePython)
  n = 8
  ref = O_element
FEATURE [App::DocumentObjectGroupPython] P_element017  label="P_element : 006"  # scripted group (container) (typed FeaturePython)
  n = 1
  ref = P_element
FEATURE [App::DocumentObjectGroupPython] G4_DNA_C  # scripted group (container) (typed FeaturePython)
  Dunit = g/cm3
  Dvalue = 1
  Group = -> [H_element137,C_element147,N_element066,O_element128,P_element017]
  conduct = 2
  density = 1
  expand = 3
  formula = G4_DNA_C
  name = G4_DNA_C
  specific = 4
FEATURE [App::DocumentObjectGroupPython] H_element138  label="H_element : 085"  # scripted group (container) (typed FeaturePython)
  n = 9
  ref = H_element
FEATURE [App::DocumentObjectGroupPython] C_element148  label="C_element : 093"  # scripted group (container) (typed FeaturePython)
  n = 9
  ref = C_element
FEATURE [App::DocumentObjectGroupPython] N_element067  label="N_element : 039"  # scripted group (container) (typed FeaturePython)
  n = 2
  ref = N_element
FEATURE [App::DocumentObjectGroupPython] O_element129  label="O_element : 9"  # scripted group (container) (typed FeaturePython)
  n = 9
  ref = O_element
FEATURE [App::DocumentObjectGroupPython] P_element018  label="P_element : 007"  # scripted group (container) (typed FeaturePython)
  n = 1
  ref = P_element
FEATURE [App::DocumentObjectGroupPython] G4_DNA_U  # scripted group (container) (typed FeaturePython)
  Dunit = g/cm3
  Dvalue = 1
  Group = -> [H_element138,C_element148,N_element067,O_element129,P_element018]
  conduct = 2
  density = 1
  expand = 3
  formula = G4_DNA_U
  name = G4_DNA_U
  specific = 4
FEATURE [App::DocumentObjectGroupPython] H_element139  label="H_element : 086"  # scripted group (container) (typed FeaturePython)
  n = 11
  ref = H_element
FEATURE [App::DocumentObjectGroupPython] C_element149  label="C_element : 094"  # scripted group (container) (typed FeaturePython)
  n = 10
  ref = C_element
FEATURE [App::DocumentObjectGroupPython] N_element068  label="N_element : 040"  # scripted group (container) (typed FeaturePython)
  n = 2
  ref = N_element
FEATURE [App::DocumentObjectGroupPython] O_element130  label="O_element : 081"  # scripted group (container) (typed FeaturePython)
  n = 9
  ref = O_element
FEATURE [App::DocumentObjectGroupPython] P_element019  label="P_element : 008"  # scripted group (container) (typed FeaturePython)
  n = 1
  ref = P_element
FEATURE [App::DocumentObjectGroupPython] G4_DNA_MU  # scripted group (container) (typed FeaturePython)
  Dunit = g/cm3
  Dvalue = 1
  Group = -> [H_element139,C_element149,N_element068,O_element130,P_element019]
  conduct = 2
  density = 1
  expand = 3
  formula = G4_DNA_MU
  name = G4_DNA_MU
  specific = 4
FEATURE [App::DocumentObjectGroupPython] BioChemical  # scripted group (container) (typed FeaturePython)
  Group = -> [G4_CYTOSINE,G4_THYMINE,G4_URACIL,G4_DNA_ADENINE,G4_DNA_GUANINE,G4_DNA_CYTOSINE,G4_DNA_THYMINE,G4_DNA_URACIL,G4_DNA_ADENOSINE,G4_DNA_GUANOSINE,G4_DNA_CYTIDINE,G4_DNA_URIDINE,G4_DNA_METHYLURIDINE,G4_DNA_MONOPHOSPHATE,G4_DNA_A,G4_DNA_G,G4_DNA_C,G4_DNA_U,G4_DNA_MU]
FEATURE [App::DocumentObjectGroupPython] G4Materials  # scripted group (container) (typed FeaturePython)
  Group = -> [NIST,Element,HEP,Space,BioChemical]
  version = 1
FEATURE [App::DocumentObjectGroupPython] Geant4  # scripted group (container) (typed FeaturePython)
  Group = -> [G4Isotopes,G4Elements,G4Materials]
FEATURE [App::DocumentObjectGroupPython] Materials  # scripted group (container) (typed FeaturePython)
  Group = -> [Geant4]
FEATURE [Part::FeaturePython] GDMLBox_WorldBox  # WARN: FeaturePython — macro-defined, semantics opaque (R4)
  lunit = 2
  material = 5
  x = 100
  y = 100
  z = 100
FEATURE [Part::FeaturePython] GDMLBox_Box  # WARN: FeaturePython — macro-defined, semantics opaque (R4)
  Placement = pos=(30,0,0) rot=(0,0,1;0rad)
  lunit = 2
  material = 0
  x = 10
  y = 10
  z = 10
FEATURE [App::Part] LV_Box
  Group = -> [GDMLBox_Box]
  Origin = -> Origin001
FEATURE [Part::FeaturePython] GDMLTorus  # WARN: FeaturePython — macro-defined, semantics opaque (R4)
  Placement = pos=(16,0,0) rot=(0,0,1;0rad)
  aunit = deg
  deltaphi = 360
  lunit = 2
  material = 0
  rmax = 2
  rmin = 0
  rtor = 5
  startphi = 0
FEATURE [App::Part] LV_Torus
  Group = -> [GDMLTorus]
  Origin = -> Origin002
  Placement = pos=(39,0,16) rot=(0,1,0;1.5708rad)
  SkinSurface = 0
FEATURE [App::Part] Part
  Group = -> [LV_Box,LV_Torus]
  Origin = -> Origin003
FEATURE [Part::FeaturePython] Array  # Draft array (typed FeaturePython)
  AlwaysSyncPlacement = false
  Angle = 180
  ArrayType = 1
  Axis = (0,0,1)
  Base = -> Part
  Center = (0,0,0)
  Count = 5
  ExpandArray = false
  Fuse = false
  IntervalAxis = (0,0,0)
  IntervalX = (50,0,0)
  IntervalY = (0,50,0)
  IntervalZ = (0,0,50)
  NumberCircles = 3
  NumberPolar = 5
  NumberX = 2
  NumberY = 2
  NumberZ = 1
  PlacementList = 5 placements: [(0,0,0),(0,0,0),(0,0,0),(0,0,0),(0,0,0)]
  RadialDistance = 50
  ScaleList = (5) [(1,1,1),(1,1,1),(1,1,1),(1,1,1),(1,1,1)]
  Symmetry = 1
  TangentialDistance = 25
FEATURE [App::Part] Part001
  Group = -> [Part,Array]
  Origin = -> Origin004
FEATURE [App::Part] worldVOL
  Group = -> [GDMLBox_WorldBox,Part001]
  Origin = -> Origin
